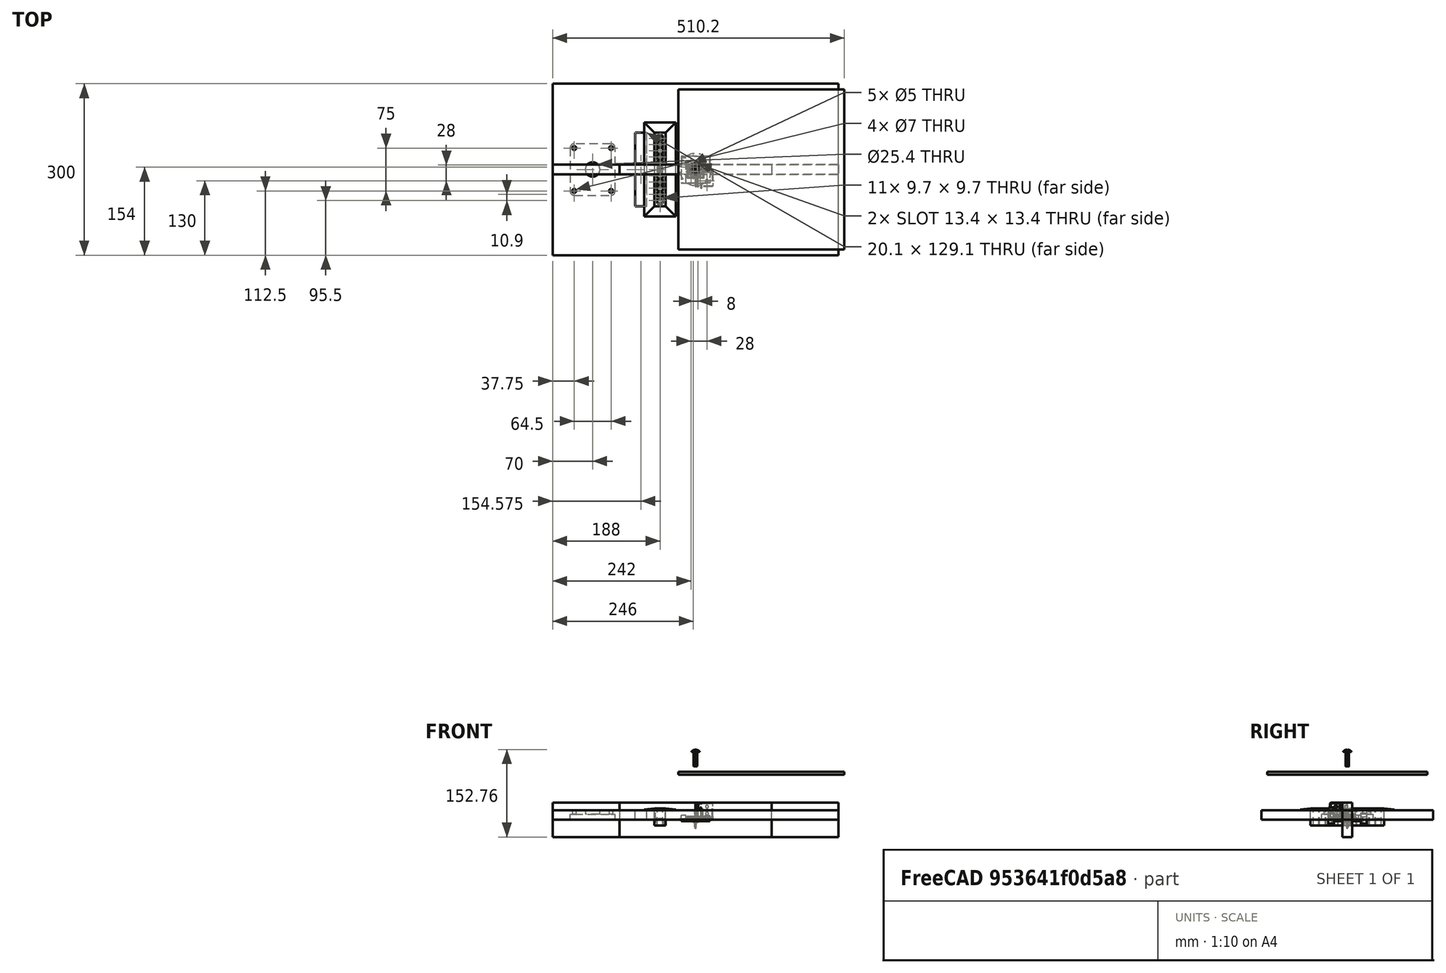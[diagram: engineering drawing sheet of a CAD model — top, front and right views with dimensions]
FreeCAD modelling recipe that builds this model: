
FCSTD DOCUMENT  (FreeCAD 1.0R39109 (Git))
Label: BoxV2
License: All rights reserved
LicenseURL: https://en.wikipedia.org/wiki/All_rights_reserved
objects: TechDraw::DrawViewDimension×86, App::Link×72, Part::Feature×47, App::DocumentObjectGroupPython×30, TechDraw::DrawProjGroupItem×23, Sketcher::SketchObject×22, TechDraw::DrawViewBalloon×18, PartDesign::Pad×15, PartDesign::Body×14, App::FeaturePython×9, TechDraw::DrawSVGTemplate×8, TechDraw::DrawPage×8, TechDraw::DrawProjGroup×7, Spreadsheet::Sheet×5, PartDesign::Pocket×5, TechDraw::DrawViewAnnotation×4, Part::FeaturePython×4, App::DocumentObjectGroup×4, PartDesign::LinearPattern×3, PartDesign::Mirrored×3, +15 more types
note: 352 computed .brp shape members not serialized (recipe doc carries the construction recipe); baked Part::Feature solids carry a one-line shape summary decoded from their .brp
EXTERNAL_REF file=../../V1/Projects/Box.FCStd obj=Body002

FEATURE [Sketcher::SketchObject] Sketch
  ArcFitTolerance = 1e-06
  AttachmentSupport = -> [XY_Plane]
  FullyConstrained = true
  MakeInternals = false
  MapMode = 5
  sketch-geometry (4):
    g0: LineSegment StartX=0 StartY=0 StartZ=0 EndX=30 EndY=0 EndZ=0
    g1: LineSegment StartX=30 StartY=0 StartZ=0 EndX=30 EndY=-30 EndZ=0
    g2: LineSegment StartX=30 StartY=-30 StartZ=0 EndX=0 EndY=-30 EndZ=0
    g3: LineSegment StartX=0 StartY=-30 StartZ=0 EndX=0 EndY=0 EndZ=0
  constraints (11):
    c: Coincident(g0,g1)
    c: Coincident(g1,g2)
    c: Coincident(g2,g3)
    c: Coincident(g3,g0)
    c: Horizontal(g0)
    c: Horizontal(g2)
    c: Vertical(g1)
    c: Vertical(g3)
    c: Distance(g1,g3) = 30
    c: Coincident(g0,g-1)
    c: DistanceY(g1,g1) = 30
FEATURE [PartDesign::Pad] Pad
  Direction = (0,0,1)
  Length = 30
  Length2 = 10
  Profile = -> Sketch
  ReferenceAxis = -> Sketch [N_Axis]
  Refine = true
  Suppressed = false
  Type = 0
FEATURE [PartDesign::Thickness] Thickness
  Base = -> Pad [Face2,Face3,Face6]
  BaseFeature = -> Pad
  Intersection = false
  Join = 0
  Mode = 0
  Refine = true
  Reversed = true
  SupportTransform = false
  Suppressed = false
  Value = 4
FEATURE [Spreadsheet::Sheet] Spreadsheet  label="LHProperties"
  cells = A1='screw_diameter; B1(screw_diameter)=5; D1='clearance; E1(clearance)=0.2; A2='bracket_dim; B2(bracket_dim)=30; A3='led_amount; B3(led_amount)=11; A4='led_dim; B4(led_dim)=9.7; A5='led_array_spacing; B5(led_array_spacing)=1.2; A6='led_array_housing_spacing; B6(led_array_housing_spacing)=5; A7='led_housing_base_length; B7(led_housing_base_length)==led_amount * led_dim + (led_amount - 1) * led_array_spacing + 2 * led_array_housing_spacing; C7='calculated; A8='led_housing_base_width; B8(led_housing_base_width)==2 * led_array_housing_spacing + led_dim; C8='calculated; A9='thickness_box_cover; B9(thickness_box_cover)==<<BXProperties>>.box_cover_thickness; C9='calculated; A10='led_housing_latch_offset_ratio; B10(led_housing_latch_offset_ratio)=4.5; A11='led_housing_latch_center_offset; B11(led_housing_latch_center_offset)==led_housing_base_length / led_housing_latch_offset_ratio; C11='calculated; A12='led_housing_latch_width; B12(led_housing_latch_width)=8; A13='led_housing_latch_thickness; B13(led_housing_latch_thickness)=1.2; A14='led_housing_height; B14(led_housing_height)==thickness_box_cover + 10 + cover_height; C14='calculated; A15='thickness_housing_shelf; B15(thickness_housing_shelf)=1.2; A16='led_housing_shelf_protrusion; B16(led_housing_shelf_protrusion)==(housing_hole_width - led_housing_base_width) / 2 - clearance / 2; C16='calculated; A17='housing_hole_width; B17(housing_hole_width)=21; A18='latch_length; B18(latch_length)=22; A19='cover_width; B19(cover_width)=55; A20='cover_height; B20(cover_height)=3
FEATURE [Sketcher::SketchObject] Sketch001
  ArcFitTolerance = 1e-06
  AttachmentOffset = pos=(0,2,0) rot=(0,0,1;0rad)
  AttachmentSupport = -> [YZ_Plane]
  FullyConstrained = true
  MakeInternals = false
  MapMode = 5
  Placement = pos=(0,0,2) rot=(0.57735,0.57735,0.57735;2.0944rad)
  expr: Constraints[1] = <<LHProperties>>.screw_diameter
  sketch-geometry (8):
    g0: Circle CenterX=-20 CenterY=21 CenterZ=0 NormalX=0 NormalY=0 NormalZ=1 AngleXU=0 Radius=2.5
    g1: Circle CenterX=-20 CenterY=9 CenterZ=0 NormalX=0 NormalY=0 NormalZ=1 AngleXU=0 Radius=2.5
    g2: LineSegment [constr] StartX=0 StartY=0 StartZ=0 EndX=0 EndY=30 EndZ=0
    g3: LineSegment [constr] StartX=0 StartY=30 StartZ=0 EndX=-30 EndY=30 EndZ=0
    g4: LineSegment [constr] StartX=-30 StartY=30 StartZ=0 EndX=-30 EndY=0 EndZ=0
    g5: LineSegment [constr] StartX=-30 StartY=0 StartZ=0 EndX=0 EndY=0 EndZ=0
    g6: LineSegment [constr] StartX=-20 StartY=21 StartZ=0 EndX=-20 EndY=30 EndZ=0
    g7: LineSegment [constr] StartX=-20 StartY=9 StartZ=0 EndX=-20 EndY=0 EndZ=0
  constraints (23):
    c: Equal(g1,g0)
    c: Diameter(g0) = 5
    c: Vertical(g0,g1)
    c: DistanceX(g1) = -20
    c: Coincident(g2,g3)
    c: Coincident(g3,g4)
    c: Coincident(g4,g5)
    c: Coincident(g5,g2)
    c: Vertical(g2)
    c: Vertical(g4)
    c: Horizontal(g3)
    c: Horizontal(g5)
    c: Coincident(g2,g-1)
    c: DistanceX(g3,g3) = 30
    c: DistanceY(g4,g4) = 30
    c: Coincident(g6,g0)
    c: PointOnObject(g6,g3)
    c: Vertical(g6)
    c: Coincident(g7,g1)
    c: PointOnObject(g7,g5)
    c: Vertical(g7)
    c: Equal(g7,g6)
    c: DistanceY(g1,g0) = 12
FEATURE [PartDesign::Pocket] Pocket
  BaseFeature = -> Thickness
  Direction = (-1,0,0)
  Length = 10
  Length2 = 5
  Midplane = true
  Profile = -> Sketch001
  ReferenceAxis = -> Sketch001 [N_Axis]
  Refine = true
  Suppressed = false
  Type = 0
FEATURE [PartDesign::PolarPattern] PolarPattern
  Angle = 90
  Axis = -> Sketch001 [V_Axis]
  BaseFeature = -> Pocket
  Mode = 0
  Occurrences = 2
  Offset = 120
  Originals = -> [Pocket]
  Refine = true
  Suppressed = false
  TransformMode = 0
FEATURE [PartDesign::SubtractiveCylinder] Cylinder
  Angle = 360
  AttacherType = Attacher::AttachEngine3D
  AttachmentOffset = pos=(20,-20,0) rot=(0,0,1;0rad)
  AttachmentSupport = -> [XY_Plane]
  BaseFeature = -> PolarPattern
  FirstAngle = 0
  Height = 10
  MapMode = 5
  Placement = pos=(20,-20,0) rot=(0,0,1;0rad)
  Radius = 2.5
  Refine = true
  SecondAngle = 0
  Suppressed = false
  expr: Radius = <<LHProperties>>.screw_diameter / 2
FEATURE [PartDesign::Chamfer] Chamfer
  Angle = 45
  Base = -> Cylinder [Edge35]
  BaseFeature = -> Cylinder
  ChamferType = 0
  FlipDirection = false
  Placement = pos=(20,-20,0) rot=(0,0,1;0rad)
  Refine = true
  Size = 8
  Size2 = 1
  SupportTransform = false
  Suppressed = false
  UseAllEdges = false
FEATURE [PartDesign::Chamfer] Chamfer001
  Angle = 45
  Base = -> Chamfer [Edge1,Edge2,Edge3,Edge4,Edge6,Edge8,Edge9,Edge10,Edge13,Edge14,Edge15,Edge16,Edge19,Edge20,Edge23,Edge24,Edge27,Edge30,Edge34,Edge35,Edge37,Edge38,Edge39]
  BaseFeature = -> Chamfer
  ChamferType = 0
  FlipDirection = false
  Placement = pos=(20,-20,0) rot=(0,0,1;0rad)
  Refine = true
  Size = 1
  Size2 = 1
  SupportTransform = false
  Suppressed = false
  UseAllEdges = false
FEATURE [PartDesign::Body] Body  label="Bracket"
  AllowCompound = false
  Group = -> [Sketch,Pad,Thickness,Sketch001,Pocket,PolarPattern,Cylinder,Chamfer,Chamfer001]
  Origin = -> Origin
  Tip = -> Chamfer001
FEATURE [Sketcher::SketchObject] Sketch002
  ArcFitTolerance = 1e-06
  AttachmentSupport = -> [XY_Plane002]
  FullyConstrained = true
  MakeInternals = false
  MapMode = 5
  expr: Constraints[10] = <<LHProperties>>.led_housing_base_length
  expr: Constraints[9] = <<LHProperties>>.led_housing_base_width
  sketch-geometry (6):
    g0: LineSegment StartX=-9.85 StartY=64.35 StartZ=0 EndX=-9.85 EndY=-64.35 EndZ=0
    g1: LineSegment StartX=-9.85 StartY=-64.35 StartZ=0 EndX=9.85 EndY=-64.35 EndZ=0
    g2: LineSegment StartX=9.85 StartY=-64.35 StartZ=0 EndX=9.85 EndY=64.35 EndZ=0
    g3: LineSegment StartX=9.85 StartY=64.35 StartZ=0 EndX=-9.85 EndY=64.35 EndZ=0
    g4: GeomPoint [constr] X=0 Y=0 Z=0
    g5: GeomPoint [constr] X=0 Y=0 Z=0
  constraints (13):
    c: Coincident(g0,g1)
    c: Coincident(g1,g2)
    c: Coincident(g2,g3)
    c: Coincident(g3,g0)
    c: Vertical(g0)
    c: Vertical(g2)
    c: Horizontal(g1)
    c: Horizontal(g3)
    c: Symmetric(g2,g0,g-1)
    c: DistanceX(g3,g3) = 19.7
    c: DistanceY(g2,g2) = 128.7
    c: Coincident(g4,g-1)
    c: Coincident(g5,g4)
FEATURE [PartDesign::Pad] Pad001
  Direction = (0,0,1)
  Length = 30
  Length2 = 10
  Profile = -> Sketch002
  ReferenceAxis = -> Sketch002 [N_Axis]
  Refine = true
  Suppressed = false
  Type = 0
  expr: Length = <<LHProperties>>.led_housing_height
FEATURE [PartDesign::SubtractiveBox] Box
  AttacherType = Attacher::AttachEngine3D
  AttachmentOffset = pos=(-4.85,49.65,0) rot=(0,0,1;0rad)
  AttachmentSupport = -> [XY_Plane002]
  BaseFeature = -> Pad001
  Height = 30
  Length = 9.7
  MapMode = 5
  Placement = pos=(-4.85,49.65,0) rot=(0,0,1;0rad)
  Refine = true
  Suppressed = false
  Width = 9.7
  expr: .AttachmentOffset.Base.x = -<<LHProperties>>.led_dim / 2
  expr: .AttachmentOffset.Base.y = -<<LHProperties>>.led_dim + <<LHProperties>>.led_housing_base_length / 2 - <<LHProperties>>.led_array_housing_spacing
  expr: Length = <<LHProperties>>.led_dim
  expr: Width = <<LHProperties>>.led_dim
FEATURE [PartDesign::LinearPattern] LinearPattern
  BaseFeature = -> Box
  Direction = -> Y_Axis002
  Length = 109
  Mode = 1
  Occurrences = 11
  Offset = 10.9
  Originals = -> [Box]
  Placement = pos=(-4.85,49.65,0) rot=(0,0,1;0rad)
  Refine = true
  Reversed = true
  Suppressed = false
  TransformMode = 0
  expr: Occurrences = <<LHProperties>>.led_amount
  expr: Offset = <<LHProperties>>.led_array_spacing + <<LHProperties>>.led_dim
FEATURE [Sketcher::SketchObject] Sketch003
  ArcFitTolerance = 1e-06
  AttachmentOffset = pos=(0,0,28.6) rot=(0,0,1;0rad)
  AttachmentSupport = -> [XZ_Plane002]
  ExternalGeometry = -> [LinearPattern]
  FullyConstrained = true
  MakeInternals = false
  MapMode = 5
  Placement = pos=(0,-28.6,6.4e-15) rot=(1,0,0;1.5708rad)
  expr: .AttachmentOffset.Base.z = <<LHProperties>>.led_housing_latch_center_offset
  expr: Constraints[13] = <<LHProperties>>.led_array_spacing
  expr: Constraints[14] = <<LHProperties>>.led_housing_latch_thickness + <<LHProperties>>.clearance
  expr: Constraints[17] = <<LHProperties>>.latch_length
  sketch-geometry (6):
    g0: LineSegment StartX=9.85 StartY=0 StartZ=0 EndX=9.85 EndY=22 EndZ=0
    g1: LineSegment StartX=9.85 StartY=22 StartZ=0 EndX=8.45 EndY=22 EndZ=0
    g2: LineSegment StartX=8.45 StartY=22 StartZ=0 EndX=8.45 EndY=15 EndZ=0
    g3: LineSegment StartX=8.45 StartY=15 StartZ=0 EndX=6.05 EndY=3 EndZ=0
    g4: LineSegment StartX=6.05 StartY=3 StartZ=0 EndX=6.05 EndY=0 EndZ=0
    g5: LineSegment StartX=6.05 StartY=0 StartZ=0 EndX=9.85 EndY=0 EndZ=0
  constraints (18):
    c: PointOnObject(g0,g-1)
    c: Vertical(g0)
    c: PointOnObject(g0,g-4)
    c: Coincident(g1,g0)
    c: Horizontal(g1)
    c: Coincident(g1,g2)
    c: Vertical(g2)
    c: Coincident(g2,g3)
    c: Coincident(g3,g4)
    c: Vertical(g4)
    c: Coincident(g4,g5)
    c: Coincident(g5,g0)
    c: Horizontal(g5)
    c: DistanceX(g-3,g4) = 1.2
    c: DistanceX(g1,g1) = 1.4
    c: DistanceY(g2,g-4) = 15
    c: DistanceY(g4,g3) = 3
    c: DistanceY(g0,g0) = 22
FEATURE [PartDesign::Pocket] Pocket001
  BaseFeature = -> LinearPattern
  Direction = (0,1,-2e-16)
  Length = 10
  Length2 = 5
  Midplane = true
  Placement = pos=(-4.85,49.65,0) rot=(0,0,1;0rad)
  Profile = -> Sketch003
  ReferenceAxis = -> Sketch003 [N_Axis]
  Refine = true
  Suppressed = false
  Type = 0
  expr: Length = <<LHProperties>>.led_housing_latch_width + 2
FEATURE [PartDesign::Mirrored] Mirrored
  MirrorPlane = -> Sketch003 [V_Axis]
  Placement = pos=(-4.85,49.65,0) rot=(0,0,1;0rad)
  Refine = true
  Suppressed = false
  TransformMode = 0
FEATURE [PartDesign::LinearPattern] LinearPattern001
  Direction = -> Sketch003 [N_Axis]
  Length = 57.2
  Mode = 1
  Occurrences = 2
  Offset = 57.2
  Placement = pos=(-4.85,49.65,0) rot=(0,0,1;0rad)
  Refine = true
  Reversed = true
  Suppressed = false
  TransformMode = 0
  expr: Offset = <<LHProperties>>.led_housing_latch_center_offset * 2
FEATURE [PartDesign::MultiTransform] MultiTransform
  BaseFeature = -> Pocket001
  Originals = -> [Pocket001]
  Placement = pos=(-4.85,49.65,0) rot=(0,0,1;0rad)
  Refine = true
  Suppressed = false
  TransformMode = 0
  Transformations = -> [Mirrored,LinearPattern001]
FEATURE [Sketcher::SketchObject] Sketch004
  ArcFitTolerance = 1e-06
  AttachmentSupport = -> [XZ_Plane003]
  FullyConstrained = true
  MakeInternals = false
  MapMode = 5
  Placement = pos=(0,0,0) rot=(1,0,0;1.5708rad)
  expr: Constraints[10] = <<LHProperties>>.latch_length - <<LHProperties>>.clearance
  expr: Constraints[13] = <<LHProperties>>.led_housing_height
  expr: Constraints[14] = <<LHProperties>>.thickness_box_cover + <<LHProperties>>.clearance + <<LHProperties>>.cover_height
  expr: Constraints[8] = <<LHProperties>>.led_housing_latch_thickness
  sketch-geometry (15):
    g0: LineSegment StartX=0.5 StartY=0 StartZ=0 EndX=1 EndY=0 EndZ=0
    g1: LineSegment StartX=1.49592 StartY=0.43623 StartZ=0 EndX=2.62751 EndY=9.23623 EndZ=0
    g2: LineSegment StartX=2.13159 StartY=9.8 StartZ=0 EndX=1.2 EndY=9.8 EndZ=0
    g3: LineSegment StartX=1.2 StartY=9.8 StartZ=0 EndX=1.2 EndY=21.8 EndZ=0
    g4: LineSegment StartX=1.2 StartY=21.8 StartZ=0 EndX=0.5 EndY=21.8 EndZ=0
    g5: LineSegment StartX=0 StartY=21.3 StartZ=0 EndX=0 EndY=0.5 EndZ=0
    g6: LineSegment [constr] StartX=0 StartY=0 StartZ=0 EndX=0 EndY=30 EndZ=0
    g7: ArcOfCircle CenterX=2.13159 CenterY=9.3 CenterZ=0 NormalX=0 NormalY=0 NormalZ=1 AngleXU=0 Radius=0.5 StartAngle=6.1553 EndAngle=7.85398
    g8: GeomPoint [constr] X=2.7 Y=9.8 Z=0
    g9: ArcOfCircle CenterX=1 CenterY=0.5 CenterZ=0 NormalX=0 NormalY=0 NormalZ=1 AngleXU=0 Radius=0.5 StartAngle=4.71239 EndAngle=6.1553
    g10: GeomPoint [constr] X=1.43982 Y=0 Z=0
    g11: ArcOfCircle CenterX=0.5 CenterY=0.5 CenterZ=0 NormalX=0 NormalY=0 NormalZ=1 AngleXU=0 Radius=0.5 StartAngle=3.14159 EndAngle=4.71239
    g12: GeomPoint [constr] X=0 Y=0 Z=0
    g13: ArcOfCircle CenterX=0.5 CenterY=21.3 CenterZ=0 NormalX=0 NormalY=0 NormalZ=1 AngleXU=0 Radius=0.5 StartAngle=1.5708 EndAngle=3.14159
    g14: GeomPoint [constr] X=0 Y=21.8 Z=0
  constraints (36):
    c: Coincident(g-1,g12)
    c: PointOnObject(g10,g-1)
    c: Horizontal(g2)
    c: Coincident(g2,g3)
    c: Vertical(g3)
    c: Coincident(g3,g4)
    c: PointOnObject(g14,g-2)
    c: Horizontal(g4)
    c: DistanceX(g14,g4) = 1.2
    c: DistanceX(g2,g8) = 1.5
    c: DistanceY(g12,g14) = 21.8
    c: Coincident(g6,g12)
    c: PointOnObject(g6,g-2)
    c: DistanceY(g6,g6) = 30
    c: DistanceY(g2,g6) = 20.2
    c: PointOnObject(g8,g1)
    c: PointOnObject(g8,g2)
    c: Tangent(g1,g7) = -1.5708
    c: Tangent(g2,g7) = -1.5708
    c: PointOnObject(g10,g0)
    c: PointOnObject(g10,g1)
    c: Tangent(g0,g9) = -1.5708
    c: Tangent(g1,g9) = -1.5708
    c: PointOnObject(g12,g0)
    c: PointOnObject(g12,g5)
    c: Tangent(g0,g11) = -1.5708
    c: Tangent(g5,g11) = -1.5708
    c: Equal(g7,g9)
    c: Radius(g7) = 0.5
    c: Radius(g11) = 0.5
    c: DistanceX(g0,g0) = 0.5
    c: PointOnObject(g14,g4)
    c: PointOnObject(g14,g5)
    c: Tangent(g4,g13) = -1.5708
    c: Tangent(g5,g13) = -1.5708
    c: Equal(g13,g7)
FEATURE [PartDesign::Pad] Pad002
  Direction = (0,-1,2e-16)
  Length = 8
  Length2 = 10
  Midplane = true
  Placement = pos=(0,0,0) rot=(1,0,0;1.5708rad)
  Profile = -> Sketch004
  ReferenceAxis = -> Sketch004 [N_Axis]
  Refine = true
  Suppressed = false
  Type = 0
  expr: Length = <<LHProperties>>.led_housing_latch_width
FEATURE [PartDesign::Body] Body002  label="Latch"
  AllowCompound = false
  Group = -> [Sketch004,Pad002]
  Origin = -> Origin003
  Placement = pos=(8.6,-28.5,0) rot=(0,0,1;0rad)
  Tip = -> Pad002
FEATURE [Sketcher::SketchObject] Sketch005
  ArcFitTolerance = 1e-06
  AttachmentSupport = -> [XZ_Plane002]
  FullyConstrained = true
  MakeInternals = false
  MapMode = 5
  Placement = pos=(0,0,0) rot=(1,0,0;1.5708rad)
  expr: Constraints[15] = <<LHProperties>>.cover_width / 2
  expr: Constraints[16] = <<LHProperties>>.cover_height
  expr: Constraints[2] = <<LHProperties>>.led_housing_height
  expr: Constraints[5] = <<LHProperties>>.led_housing_base_width / 2
  sketch-geometry (6):
    g0: LineSegment [constr] StartX=0 StartY=0 StartZ=0 EndX=0 EndY=30 EndZ=0
    g1: LineSegment [constr] StartX=0 StartY=30 StartZ=0 EndX=9.85 EndY=30 EndZ=0
    g2: LineSegment StartX=9.85 StartY=30 StartZ=0 EndX=27.5 EndY=28 EndZ=0
    g3: LineSegment StartX=27.5 StartY=28 StartZ=0 EndX=27.5 EndY=27 EndZ=0
    g4: LineSegment StartX=27.5 StartY=27 StartZ=0 EndX=9.85 EndY=27 EndZ=0
    g5: LineSegment StartX=9.85 StartY=27 StartZ=0 EndX=9.85 EndY=30 EndZ=0
  constraints (17):
    c: Coincident(g0,g-1)
    c: PointOnObject(g0,g-2)
    c: DistanceY(g0,g0) = 30
    c: Coincident(g1,g0)
    c: Horizontal(g1)
    c: DistanceX(g1,g1) = 9.85
    c: Coincident(g2,g1)
    c: Coincident(g3,g2)
    c: Coincident(g4,g3)
    c: Horizontal(g4)
    c: Vertical(g4,g1)
    c: Coincident(g5,g4)
    c: Coincident(g5,g1)
    c: Vertical(g3)
    c: DistanceY(g3,g3) = 1
    c: DistanceX(g0,g2) = 27.5
    c: DistanceY(g4,g0) = 3
FEATURE [PartDesign::AdditivePipe] AdditivePipe
  AuxilleryCurvelinear = true
  AuxillerySpineTangent = false
  BaseFeature = -> MultiTransform
  Binormal = (0,0,0)
  Mode = 0
  Placement = pos=(-4.85,49.65,0) rot=(0,0,1;0rad)
  Profile = -> Sketch005
  Refine = true
  Spine = -> MultiTransform [Edge95,Edge93,Edge11,Edge94]
  SpineTangent = false
  Suppressed = false
  Transformation = 0
  Transition = 1
FEATURE [PartDesign::Body] Body001  label="LED_Housing"
  AllowCompound = false
  Group = -> [Sketch002,Pad001,Box,LinearPattern,Sketch003,Pocket001,MultiTransform,Mirrored,LinearPattern001,Sketch005,AdditivePipe]
  Origin = -> Origin002
  Placement = pos=(-62,0,-10) rot=(0,0,1;0rad)
  Tip = -> AdditivePipe
FEATURE [Sketcher::SketchObject] Sketch006
  ArcFitTolerance = 1e-06
  AttachmentSupport = -> [XY_Plane004]
  FullyConstrained = true
  MakeInternals = false
  MapMode = 5
  expr: Constraints[17] = <<BXProperties>>.box_width
  expr: Constraints[18] = <<BXProperties>>.box_length
  expr: Constraints[27] = <<BXProperties>>.foam_edge_margin
  expr: Constraints[28] = <<BXProperties>>.foam_edge_margin
  expr: Constraints[29] = <<BXProperties>>.foam_width
  expr: Constraints[32] = <<LHProperties>>.led_housing_base_width + <<LHProperties>>.clearance * 2
  expr: Constraints[33] = <<LHProperties>>.led_housing_base_length + <<LHProperties>>.clearance * 2
  expr: Constraints[46] = <<BXProperties>>.joystick_true_width
  expr: Constraints[47] = <<BXProperties>>.joystick_true_length
  expr: Constraints[55] = <<BXProperties>>.joystick_bolt_hole
  sketch-geometry (29):
    g0: LineSegment StartX=-250 StartY=150 StartZ=0 EndX=-250 EndY=-150 EndZ=0
    g1: LineSegment StartX=-250 StartY=-150 StartZ=0 EndX=250 EndY=-150 EndZ=0
    g2: LineSegment StartX=250 StartY=-150 StartZ=0 EndX=250 EndY=150 EndZ=0
    g3: LineSegment StartX=250 StartY=150 StartZ=0 EndX=-250 EndY=150 EndZ=0
    g4: LineSegment StartX=-105.475 StartY=64.55 StartZ=0 EndX=-105.475 EndY=-64.55 EndZ=0
    g5: LineSegment StartX=-105.475 StartY=-64.55 StartZ=0 EndX=-85.375 EndY=-64.55 EndZ=0
    g6: LineSegment StartX=-85.375 StartY=-64.55 StartZ=0 EndX=-85.375 EndY=64.55 EndZ=0
    g7: LineSegment StartX=-85.375 StartY=64.55 StartZ=0 EndX=-105.475 EndY=64.55 EndZ=0
    g8: LineSegment [constr] StartX=-50 StartY=-140 StartZ=0 EndX=240 EndY=-140 EndZ=0
    g9: LineSegment [constr] StartX=240 StartY=-140 StartZ=0 EndX=240 EndY=140 EndZ=0
    g10: LineSegment [constr] StartX=240 StartY=140 StartZ=0 EndX=-50 EndY=140 EndZ=0
    g11: LineSegment [constr] StartX=-50 StartY=140 StartZ=0 EndX=-50 EndY=-140 EndZ=0
    g12: LineSegment [constr] StartX=-85.375 StartY=6.1e-15 StartZ=0 EndX=-50 EndY=-3e-15 EndZ=0
    g13: LineSegment [constr] StartX=-219.15 StartY=45.15 StartZ=0 EndX=-219.15 EndY=-45.15 EndZ=0
    g14: LineSegment [constr] StartX=-219.15 StartY=-45.15 StartZ=0 EndX=-140.85 EndY=-45.15 EndZ=0
    g15: LineSegment [constr] StartX=-140.85 StartY=-45.15 StartZ=0 EndX=-140.85 EndY=45.15 EndZ=0
    g16: LineSegment [constr] StartX=-140.85 StartY=45.15 StartZ=0 EndX=-219.15 EndY=45.15 EndZ=0
    g17: GeomPoint [constr] X=-180 Y=0 Z=0
    g18: LineSegment [constr] StartX=-140.85 StartY=-6.3e-15 StartZ=0 EndX=-105.475 EndY=-6.2e-15 EndZ=0
    g19: Circle CenterX=-180 CenterY=0 CenterZ=0 NormalX=0 NormalY=0 NormalZ=1 AngleXU=0 Radius=12.7
    g20: Circle CenterX=-212.25 CenterY=37.5 CenterZ=0 NormalX=0 NormalY=0 NormalZ=1 AngleXU=0 Radius=3.5
    g21: Circle CenterX=-147.75 CenterY=37.5 CenterZ=0 NormalX=0 NormalY=0 NormalZ=1 AngleXU=0 Radius=3.5
    g22: Circle CenterX=-147.75 CenterY=-37.5 CenterZ=0 NormalX=0 NormalY=0 NormalZ=1 AngleXU=0 Radius=3.5
    g23: Circle CenterX=-212.25 CenterY=-37.5 CenterZ=0 NormalX=0 NormalY=0 NormalZ=1 AngleXU=0 Radius=3.5
    g24: LineSegment [constr] StartX=-212.25 StartY=37.5 StartZ=0 EndX=-212.25 EndY=-37.5 EndZ=0
    g25: LineSegment [constr] StartX=-212.25 StartY=-37.5 StartZ=0 EndX=-147.75 EndY=-37.5 EndZ=0
    g26: LineSegment [constr] StartX=-147.75 StartY=-37.5 StartZ=0 EndX=-147.75 EndY=37.5 EndZ=0
    g27: LineSegment [constr] StartX=-147.75 StartY=37.5 StartZ=0 EndX=-212.25 EndY=37.5 EndZ=0
    g28: LineSegment [constr] StartX=-180 StartY=37.5 StartZ=0 EndX=-180 EndY=-37.5 EndZ=0
  constraints (73):
    c: Coincident(g0,g1)
    c: Coincident(g1,g2)
    c: Coincident(g2,g3)
    c: Coincident(g3,g0)
    c: Vertical(g0)
    c: Vertical(g2)
    c: Horizontal(g1)
    c: Horizontal(g3)
    c: Symmetric(g1,g0,g-1)
    c: Coincident(g4,g5)
    c: Coincident(g5,g6)
    c: Coincident(g6,g7)
    c: Coincident(g7,g4)
    c: Vertical(g4)
    c: Horizontal(g5)
    c: Horizontal(g7)
    c: Symmetric(g6,g5,g-1)
    c: DistanceX(g3,g3) = 500
    c: DistanceY(g2,g2) = 300
    c: Coincident(g8,g9)
    c: Coincident(g9,g10)
    c: Coincident(g10,g11)
    c: Coincident(g11,g8)
    c: Horizontal(g8)
    c: Horizontal(g10)
    c: Vertical(g11)
    c: Symmetric(g9,g8,g-1)
    c: DistanceX(g9,g2) = 10
    c: DistanceY(g9,g2) = 10
    c: DistanceX(g10,g10) = 290
    c: Symmetric(g6,g6,g12)
    c: Symmetric(g11,g11,g12)
    c: DistanceX(g7,g7) = 20.1
    c: DistanceY(g6,g6) = 129.1
    c: Coincident(g13,g14)
    c: Coincident(g14,g15)
    c: Coincident(g15,g16)
    c: Coincident(g16,g13)
    c: Vertical(g13)
    c: Vertical(g15)
    c: Horizontal(g14)
    c: Horizontal(g16)
    c: Symmetric(g13,g14,g17)
    c: Symmetric(g15,g15,g18)
    c: Symmetric(g4,g4,g18)
    c: Equal(g18,g12)
    c: DistanceX(g16,g16) = 78.3
    c: DistanceY(g15,g15) = 90.3
    c: DistanceX(g0,g17) = 70
    c: PointOnObject(g17,g-1)
    c: Coincident(g19,g17)
    c: Diameter(g19) = 25.4
    c: Equal(g23,g22)
    c: Equal(g22,g21)
    c: Equal(g21,g20)
    c: Diameter(g20) = 7
    c: Coincident(g24,g25)
    c: Coincident(g25,g26)
    c: Coincident(g26,g27)
    c: Coincident(g27,g24)
    c: Vertical(g26)
    c: Coincident(g24,g20)
    c: Coincident(g25,g22)
    c: Coincident(g24,g23)
    c: Coincident(g21,g26)
    c: Horizontal(g27)
    c: Horizontal(g25)
    c: DistanceX(g21,g15) = 6.9
    c: DistanceY(g21,g15) = 7.65
    c: Symmetric(g20,g23,g-1)
    c: Symmetric(g27,g27,g28)
    c: Symmetric(g25,g25,g28)
    c: PointOnObject(g17,g28)
FEATURE [Spreadsheet::Sheet] Spreadsheet001  label="BXProperties"
  cells = A1='box_width; B1(box_width)=500; A2='box_length; B2(box_length)=300; A3='box_cover_thickness; B3(box_cover_thickness)=17; A4='wall_thickness; B4(wall_thickness)=17; A5='joystick_hole_width; B5(joystick_hole_width)=70; A6='joystick_hole_length; B6(joystick_hole_length)=60; A7='joystick_edge_ratio; B7(joystick_edge_ratio)=0.07; A8='joystick_edge_margin; B8(joystick_edge_margin)==box_width * joystick_edge_ratio; C8='calculated; A9='foam_edge_margin; B9(foam_edge_margin)=10; A10='foam_box_ratio; B10(foam_box_ratio)=0.58; A11='foam_width; B11(foam_width)==box_width * foam_box_ratio; C11='calculated; A12='foam_length; B12(foam_length)==box_length - foam_edge_margin * 2; C12='calculated; A13='joystick_true_width; B13(joystick_true_width)=78.3; A14='joystick_true_length; B14(joystick_true_length)=90.3; A15='wall_height; B15(wall_height)=60; A16='joystick_hole; B16(joystick_hole)=25.4; A17='joystick_fillet_radius; B17(joystick_fillet_radius)=7; A18='joystick_bolt_hole; B18(joystick_bolt_hole)=7
FEATURE [PartDesign::Pad] Pad003
  Direction = (0,0,1)
  Length = 17
  Length2 = 10
  Profile = -> Sketch006
  ReferenceAxis = -> Sketch006 [N_Axis]
  Refine = true
  Suppressed = false
  Type = 0
  expr: Length = <<BXProperties>>.box_cover_thickness
FEATURE [Sketcher::SketchObject] Sketch007
  ArcFitTolerance = 1e-06
  AttachmentSupport = -> [XZ_Plane005]
  FullyConstrained = true
  MakeInternals = false
  MapMode = 5
  Placement = pos=(0,0,0) rot=(1,0,0;1.5708rad)
  expr: Constraints[10] = <<BXProperties>>.box_width
  expr: Constraints[11] = <<BXProperties>>.wall_height
  sketch-geometry (5):
    g0: LineSegment StartX=-250 StartY=-30 StartZ=0 EndX=250 EndY=-30 EndZ=0
    g1: LineSegment StartX=250 StartY=-30 StartZ=0 EndX=250 EndY=30 EndZ=0
    g2: LineSegment StartX=250 StartY=30 StartZ=0 EndX=-250 EndY=30 EndZ=0
    g3: LineSegment StartX=-250 StartY=30 StartZ=0 EndX=-250 EndY=-30 EndZ=0
    g4: GeomPoint [constr] X=0 Y=0 Z=0
  constraints (12):
    c: Coincident(g0,g1)
    c: Coincident(g1,g2)
    c: Coincident(g2,g3)
    c: Coincident(g3,g0)
    c: Horizontal(g0)
    c: Horizontal(g2)
    c: Vertical(g1)
    c: Vertical(g3)
    c: Symmetric(g2,g0,g4)
    c: Coincident(g4,g-1)
    c: DistanceX(g2,g2) = 500
    c: DistanceY(g1,g1) = 60
FEATURE [PartDesign::Pad] Pad004
  Direction = (0,-1,2e-16)
  Length = 17
  Length2 = 10
  Midplane = true
  Placement = pos=(0,0,0) rot=(1,0,0;1.5708rad)
  Profile = -> Sketch007
  ReferenceAxis = -> Sketch007 [N_Axis]
  Refine = true
  Suppressed = false
  Type = 0
  expr: Length = <<BXProperties>>.wall_thickness
FEATURE [PartDesign::Body] Body004  label="Wall_Long"
  AllowCompound = false
  Group = -> [Sketch007,Pad004]
  Origin = -> Origin005
  Tip = -> Pad004
FEATURE [Sketcher::SketchObject] Sketch008
  ArcFitTolerance = 1e-06
  AttachmentSupport = -> [XZ_Plane006]
  FullyConstrained = true
  MakeInternals = false
  MapMode = 5
  Placement = pos=(0,0,0) rot=(1,0,0;1.5708rad)
  expr: Constraints[10] = <<BXProperties>>.box_length - <<BXProperties>>.wall_thickness * 2
  expr: Constraints[11] = <<BXProperties>>.wall_height
  sketch-geometry (5):
    g0: LineSegment StartX=-133 StartY=-30 StartZ=0 EndX=133 EndY=-30 EndZ=0
    g1: LineSegment StartX=133 StartY=-30 StartZ=0 EndX=133 EndY=30 EndZ=0
    g2: LineSegment StartX=133 StartY=30 StartZ=0 EndX=-133 EndY=30 EndZ=0
    g3: LineSegment StartX=-133 StartY=30 StartZ=0 EndX=-133 EndY=-30 EndZ=0
    g4: GeomPoint [constr] X=0 Y=0 Z=0
  constraints (12):
    c: Coincident(g0,g1)
    c: Coincident(g1,g2)
    c: Coincident(g2,g3)
    c: Coincident(g3,g0)
    c: Horizontal(g0)
    c: Horizontal(g2)
    c: Vertical(g1)
    c: Vertical(g3)
    c: Symmetric(g2,g0,g4)
    c: Coincident(g4,g-1)
    c: DistanceX(g2,g2) = 266
    c: DistanceY(g1,g1) = 60
FEATURE [PartDesign::Pad] Pad005
  Direction = (0,-1,2e-16)
  Length = 17
  Length2 = 10
  Midplane = true
  Placement = pos=(0,0,0) rot=(1,0,0;1.5708rad)
  Profile = -> Sketch008
  ReferenceAxis = -> Sketch008 [N_Axis]
  Refine = true
  Suppressed = false
  Type = 0
  expr: Length = <<BXProperties>>.wall_thickness
FEATURE [PartDesign::Body] Body005  label="Wall_Short"
  AllowCompound = false
  Group = -> [Sketch008,Pad005]
  Origin = -> Origin006
  Tip = -> Pad005
FEATURE [TechDraw::DrawSVGTemplate] Template
  EditableTexts = AuthorName=Alex Anastasakis,CheckDate=2024-11-29,CreationDate=2024-11-26,DrawingNumber=3,FC-Scale=1 : 4,FC-Title=Cover,SheetNumber=1 / 1,+2 more (map truncated)
  Height = 297
  Orientation = 1
  Template = <userpath>/AppData/Local/Programs/FreeCAD 1.0/data/Mod/TechDraw/Templates/A3_Landscape_TD.svg
  Width = 420
FEATURE [Sketcher::SketchObject] Sketch009
  ArcFitTolerance = 1e-06
  AttachmentSupport = -> [XY_Plane004]
  FullyConstrained = true
  MakeInternals = false
  MapMode = 5
  expr: Constraints[17] = Sketch006.Constraints[17]
  expr: Constraints[18] = Sketch006.Constraints[18]
  expr: Constraints[27] = Sketch006.Constraints[27]
  expr: Constraints[28] = Sketch006.Constraints[28]
  expr: Constraints[29] = Sketch006.Constraints[29]
  expr: Constraints[32] = Sketch006.Constraints[32]
  expr: Constraints[33] = Sketch006.Constraints[33]
  expr: Constraints[44] = Sketch006.Constraints[46]
  expr: Constraints[45] = Sketch006.Constraints[47]
  expr: Constraints[46] = Sketch006.Constraints[48]
  expr: Constraints[49] = <<BXProperties>>.joystick_hole
  expr: Constraints[69] = <<BXProperties>>.joystick_fillet_radius
  sketch-geometry (29):
    g0: LineSegment [constr] StartX=-250 StartY=150 StartZ=0 EndX=-250 EndY=-150 EndZ=0
    g1: LineSegment [constr] StartX=-250 StartY=-150 StartZ=0 EndX=250 EndY=-150 EndZ=0
    g2: LineSegment [constr] StartX=250 StartY=-150 StartZ=0 EndX=250 EndY=150 EndZ=0
    g3: LineSegment [constr] StartX=250 StartY=150 StartZ=0 EndX=-250 EndY=150 EndZ=0
    g4: LineSegment [constr] StartX=-105.475 StartY=64.55 StartZ=0 EndX=-105.475 EndY=-64.55 EndZ=0
    g5: LineSegment [constr] StartX=-105.475 StartY=-64.55 StartZ=0 EndX=-85.375 EndY=-64.55 EndZ=0
    g6: LineSegment [constr] StartX=-85.375 StartY=-64.55 StartZ=0 EndX=-85.375 EndY=64.55 EndZ=0
    g7: LineSegment [constr] StartX=-85.375 StartY=64.55 StartZ=0 EndX=-105.475 EndY=64.55 EndZ=0
    g8: LineSegment [constr] StartX=-50 StartY=-140 StartZ=0 EndX=240 EndY=-140 EndZ=0
    g9: LineSegment [constr] StartX=240 StartY=-140 StartZ=0 EndX=240 EndY=140 EndZ=0
    g10: LineSegment [constr] StartX=240 StartY=140 StartZ=0 EndX=-50 EndY=140 EndZ=0
    g11: LineSegment [constr] StartX=-50 StartY=140 StartZ=0 EndX=-50 EndY=-140 EndZ=0
    g12: LineSegment [constr] StartX=-85.375 StartY=1.2e-15 StartZ=0 EndX=-50 EndY=-1.22e-14 EndZ=0
    g13: LineSegment StartX=-219.15 StartY=38.15 StartZ=0 EndX=-219.15 EndY=-38.15 EndZ=0
    g14: LineSegment StartX=-212.15 StartY=-45.15 StartZ=0 EndX=-147.85 EndY=-45.15 EndZ=0
    g15: LineSegment StartX=-140.85 StartY=-38.15 StartZ=0 EndX=-140.85 EndY=38.15 EndZ=0
    g16: LineSegment StartX=-147.85 StartY=45.15 StartZ=0 EndX=-212.15 EndY=45.15 EndZ=0
    g17: GeomPoint [constr] X=-180 Y=0 Z=0
    g18: LineSegment [constr] StartX=-219.15 StartY=45.15 StartZ=0 EndX=-140.85 EndY=-45.15 EndZ=0
    g19: LineSegment [constr] StartX=-140.85 StartY=-4.6e-15 StartZ=0 EndX=-105.475 EndY=5e-16 EndZ=0
    g20: Circle [constr] CenterX=-180 CenterY=0 CenterZ=0 NormalX=0 NormalY=0 NormalZ=1 AngleXU=0 Radius=12.7
    g21: ArcOfCircle CenterX=-147.85 CenterY=38.15 CenterZ=0 NormalX=0 NormalY=0 NormalZ=1 AngleXU=0 Radius=7 StartAngle=0 EndAngle=1.5708
    g22: GeomPoint [constr] X=-140.85 Y=45.15 Z=0
    g23: ArcOfCircle CenterX=-212.15 CenterY=38.15 CenterZ=0 NormalX=0 NormalY=0 NormalZ=1 AngleXU=0 Radius=7 StartAngle=1.5708 EndAngle=3.14159
    g24: GeomPoint [constr] X=-219.15 Y=45.15 Z=0
    g25: ArcOfCircle CenterX=-212.15 CenterY=-38.15 CenterZ=0 NormalX=0 NormalY=0 NormalZ=1 AngleXU=0 Radius=7 StartAngle=3.14159 EndAngle=4.71239
    g26: GeomPoint [constr] X=-219.15 Y=-45.15 Z=0
    g27: ArcOfCircle CenterX=-147.85 CenterY=-38.15 CenterZ=0 NormalX=0 NormalY=0 NormalZ=1 AngleXU=0 Radius=7 StartAngle=4.71239 EndAngle=6.28319
    g28: GeomPoint [constr] X=-140.85 Y=-45.15 Z=0
  constraints (70):
    c: Coincident(g0,g1)
    c: Coincident(g1,g2)
    c: Coincident(g2,g3)
    c: Coincident(g3,g0)
    c: Vertical(g0)
    c: Vertical(g2)
    c: Horizontal(g1)
    c: Horizontal(g3)
    c: Symmetric(g1,g0,g-1)
    c: Coincident(g4,g5)
    c: Coincident(g5,g6)
    c: Coincident(g6,g7)
    c: Coincident(g7,g4)
    c: Vertical(g4)
    c: Horizontal(g5)
    c: Horizontal(g7)
    c: Symmetric(g6,g5,g-1)
    c: DistanceX(g3,g3) = 500
    c: DistanceY(g2,g2) = 300
    c: Coincident(g8,g9)
    c: Coincident(g9,g10)
    c: Coincident(g10,g11)
    c: Coincident(g11,g8)
    c: Horizontal(g8)
    c: Horizontal(g10)
    c: Vertical(g11)
    c: Symmetric(g9,g8,g-1)
    c: DistanceX(g9,g2) = 10
    c: DistanceY(g9,g2) = 10
    c: DistanceX(g10,g10) = 290
    c: Symmetric(g6,g6,g12)
    c: Symmetric(g11,g11,g12)
    c: DistanceX(g7,g7) = 20.1
    c: DistanceY(g6,g6) = 129.1
    c: Vertical(g13)
    c: Vertical(g15)
    c: Horizontal(g14)
    c: Horizontal(g16)
    c: Coincident(g18,g24)
    c: Coincident(g18,g28)
    c: Symmetric(g18,g18,g17)
    c: Symmetric(g28,g22,g19)
    c: Symmetric(g4,g4,g19)
    c: Equal(g19,g12)
    c: DistanceX(g24,g22) = 78.3
    c: DistanceY(g28,g22) = 90.3
    c: DistanceX(g0,g17) = 70
    c: PointOnObject(g17,g-1)
    c: Coincident(g20,g17)
    c: Diameter(g20) = 25.4
    c: PointOnObject(g22,g15)
    c: PointOnObject(g22,g16)
    c: Tangent(g15,g21) = -1.5708
    c: Tangent(g16,g21) = -1.5708
    c: PointOnObject(g24,g16)
    c: PointOnObject(g24,g13)
    c: Tangent(g16,g23) = -1.5708
    c: Tangent(g13,g23) = -1.5708
    c: PointOnObject(g26,g14)
    c: PointOnObject(g26,g13)
    c: Tangent(g14,g25) = -1.5708
    c: Tangent(g13,g25) = -1.5708
    c: PointOnObject(g28,g14)
    c: PointOnObject(g28,g15)
    c: Tangent(g14,g27) = -1.5708
    c: Tangent(g15,g27) = -1.5708
    c: Equal(g27,g25)
    c: Equal(g27,g21)
    c: Equal(g21,g23)
    c: Radius(g27) = 7
FEATURE [PartDesign::Pocket] Pocket002
  BaseFeature = -> Pad003
  Direction = (0,0,-1)
  Length = 10
  Length2 = 5
  Profile = -> Sketch009
  ReferenceAxis = -> Sketch009 [N_Axis]
  Refine = true
  Reversed = true
  Suppressed = false
  Type = 0
FEATURE [PartDesign::Body] Body003  label="Box_Cover"
  AllowCompound = false
  Group = -> [Sketch006,Pad003,Sketch009,Pocket002]
  Origin = -> Origin004
  Tip = -> Pocket002
FEATURE [TechDraw::DrawProjGroupItem] View  label="Front"
  CoarseView = false
  Direction = (0,-1,0)
  Focus = 100
  HardHidden = true
  IsoCount = 0
  IsoHidden = false
  IsoVisible = false
  LockPosition = true
  Perspective = false
  Rotation = 0
  RotationVector = (1,0,0)
  Scale = 0.25
  ScaleType = 2
  ScrubCount = 1
  SeamHidden = false
  SeamVisible = false
  SmoothHidden = false
  SmoothVisible = true
  Source = -> [Body003]
  Type = 0
  X = 0
  XDirection = (1,0,0)
  Y = 0
FEATURE [TechDraw::DrawProjGroupItem] ProjItem001  label="FrontTopRight"
  CoarseView = false
  Direction = (0.57735,-0.57735,0.57735)
  Focus = 100
  HardHidden = false
  IsoCount = 0
  IsoHidden = false
  IsoVisible = false
  LockPosition = false
  Perspective = false
  Rotation = 0
  RotationVector = (1,0,0)
  ScaleType = 2
  ScrubCount = 1
  SeamHidden = false
  SeamVisible = false
  SmoothHidden = false
  SmoothVisible = true
  Source = -> [Body003]
  Type = 7
  X = 171.843
  XDirection = (0.707107,0.707107,0)
  Y = -22.4367
FEATURE [TechDraw::DrawViewDimension] Dimension002
  AngleOverride = false
  Arbitrary = false
  ArbitraryTolerances = false
  BoxCorners = (2) [(-50,-2.125,0),(50,2.125,0)]
  EqualTolerance = true
  ExtensionAngle = 0
  FormatSpec = %.2w
  FormatSpecOverTolerance = %+.2w
  FormatSpecUnderTolerance = %+.2w
  Inverted = false
  LineAngle = 0
  LockPosition = false
  MeasureType = 1
  OverTolerance = 0
  References2D = -> [View]
  Rotation = 0
  Scale = 0.25
  ScaleType = 0
  TheoreticalExact = false
  Type = 2
  UnderTolerance = 0
  X = -76.3815
  Y = -6.4878
FEATURE [Sketcher::SketchObject] Sketch010
  ArcFitTolerance = 1e-06
  AttachmentSupport = -> [XY_Plane008]
  FullyConstrained = true
  MakeInternals = false
  MapMode = 5
  expr: Constraints[10] = <<BXProperties>>.foam_width
  expr: Constraints[11] = <<BXProperties>>.foam_length
  sketch-geometry (5):
    g0: LineSegment StartX=-145 StartY=-140 StartZ=0 EndX=145 EndY=-140 EndZ=0
    g1: LineSegment StartX=145 StartY=-140 StartZ=0 EndX=145 EndY=140 EndZ=0
    g2: LineSegment StartX=145 StartY=140 StartZ=0 EndX=-145 EndY=140 EndZ=0
    g3: LineSegment StartX=-145 StartY=140 StartZ=0 EndX=-145 EndY=-140 EndZ=0
    g4: GeomPoint [constr] X=0 Y=0 Z=0
  constraints (12):
    c: Coincident(g0,g1)
    c: Coincident(g1,g2)
    c: Coincident(g2,g3)
    c: Coincident(g3,g0)
    c: Horizontal(g0)
    c: Horizontal(g2)
    c: Vertical(g1)
    c: Vertical(g3)
    c: Symmetric(g2,g0,g4)
    c: Coincident(g4,g-1)
    c: DistanceX(g2,g2) = 290
    c: DistanceY(g1,g1) = 280
FEATURE [PartDesign::Pad] Pad006
  Direction = (0,0,1)
  Length = 5
  Length2 = 10
  Profile = -> Sketch010
  ReferenceAxis = -> Sketch010 [N_Axis]
  Refine = true
  Suppressed = false
  Type = 0
FEATURE [PartDesign::Body] Body006  label="Foam_Pad"
  AllowCompound = false
  Group = -> [Sketch010,Pad006]
  Origin = -> Origin008
  Placement = pos=(115.2,0,79) rot=(0,0,1;0rad)
  Tip = -> Pad006
FEATURE [Sketcher::SketchObject] Sketch027
  ArcFitTolerance = 1e-06
  AttachmentSupport = -> [XY_Plane015]
  FullyConstrained = true
  MakeInternals = false
  MapMode = 5
  expr: Constraints[11] = <<CMProperties>>.cm_size
  sketch-geometry (5):
    g0: LineSegment StartX=-15 StartY=-15 StartZ=0 EndX=15 EndY=-15 EndZ=0
    g1: LineSegment StartX=15 StartY=-15 StartZ=0 EndX=15 EndY=15 EndZ=0
    g2: LineSegment StartX=15 StartY=15 StartZ=0 EndX=-15 EndY=15 EndZ=0
    g3: LineSegment StartX=-15 StartY=15 StartZ=0 EndX=-15 EndY=-15 EndZ=0
    g4: GeomPoint [constr] X=-1e-16 Y=0 Z=0
  constraints (12):
    c: Coincident(g0,g1)
    c: Coincident(g1,g2)
    c: Coincident(g2,g3)
    c: Coincident(g3,g0)
    c: Horizontal(g0)
    c: Horizontal(g2)
    c: Vertical(g1)
    c: Vertical(g3)
    c: Symmetric(g2,g0,g4)
    c: Coincident(g4,g-1)
    c: Equal(g2,g1)
    c: DistanceX(g2,g2) = 30
FEATURE [Spreadsheet::Sheet] Spreadsheet003  label="CMProperties"
  cells = A1='cm_size; B1(cm_size)=30; A2='cm_base_height; B2(cm_base_height)=1.2; A3='cm_height; B3(cm_height)==cm_track_size; A4='border_thickness; B4(border_thickness)=1.6; A5='cover_thickness; B5(cover_thickness)=1.2; A6='cm_cover_size; B6(cm_cover_size)==cm_size - border_thickness * 2 - 0.2 * 2; C6='calculated; A7='cm_track_size; B7(cm_track_size)=3.5
FEATURE [PartDesign::Pad] Pad013
  Direction = (0,0,1)
  Length = 4.7
  Length2 = 10
  Profile = -> Sketch027
  ReferenceAxis = -> Sketch027 [N_Axis]
  Refine = true
  Suppressed = false
  Type = 0
  expr: Length = <<CMProperties>>.cm_height + <<CMProperties>>.cm_base_height
FEATURE [Sketcher::SketchObject] Sketch028
  ArcFitTolerance = 1e-06
  AttachmentOffset = pos=(0,0,1.2) rot=(0,0,1;0rad)
  AttachmentSupport = -> [XY_Plane015]
  FullyConstrained = true
  MakeInternals = false
  MapMode = 5
  Placement = pos=(0,0,1.2) rot=(0,0,1;0rad)
  expr: .AttachmentOffset.Base.z = <<CMProperties>>.cm_base_height
  expr: Constraints[10] = <<CMProperties>>.cm_size / 2
  expr: Constraints[34] = <<CMProperties>>.cm_track_size
  expr: Constraints[9] = <<CMProperties>>.cm_size / 2
  sketch-geometry (19):
    g0: ArcOfCircle [constr] CenterX=-6 CenterY=6.01432 CenterZ=0 NormalX=0 NormalY=0 NormalZ=1 AngleXU=0 Radius=6.01432 StartAngle=4.71239 EndAngle=6.21417
    g1: ArcOfCircle [constr] CenterX=5.2375 CenterY=5.2375 CenterZ=0 NormalX=0 NormalY=0 NormalZ=1 AngleXU=0 Radius=5.25 StartAngle=4.78141 EndAngle=9.35576
    g2: LineSegment [constr] StartX=-6 StartY=0 StartZ=0 EndX=-15 EndY=0 EndZ=0
    g3: ArcOfCircle [constr] CenterX=6.01432 CenterY=-6 CenterZ=0 NormalX=0 NormalY=0 NormalZ=1 AngleXU=0 Radius=6.01432 StartAngle=1.63981 EndAngle=3.14159
    g4: LineSegment [constr] StartX=0 StartY=-6 StartZ=0 EndX=0 EndY=-15 EndZ=0
    g5: ArcOfCircle [constr] CenterX=-15 CenterY=0 CenterZ=0 NormalX=0 NormalY=0 NormalZ=-1 AngleXU=-3.14159 Radius=1.75 StartAngle=1.5708 EndAngle=4.71239
    g6: LineSegment StartX=-6 StartY=1.75 StartZ=0 EndX=-15 EndY=1.75 EndZ=0
    g7: ArcOfCircle CenterX=-6 CenterY=6.01432 CenterZ=0 NormalX=0 NormalY=0 NormalZ=1 AngleXU=0 Radius=4.26432 StartAngle=4.71239 EndAngle=6.21417
    g8: ArcOfCircle CenterX=5.2375 CenterY=5.2375 CenterZ=0 NormalX=0 NormalY=0 NormalZ=1 AngleXU=0 Radius=7 StartAngle=4.78141 EndAngle=9.35576
    g9: ArcOfCircle CenterX=6.01432 CenterY=-6 CenterZ=0 NormalX=0 NormalY=0 NormalZ=1 AngleXU=0 Radius=4.26432 StartAngle=1.63981 EndAngle=3.14159
    g10: LineSegment StartX=1.75 StartY=-6 StartZ=0 EndX=1.75 EndY=-15 EndZ=0
    g11: ArcOfCircle [constr] CenterX=0 CenterY=-15 CenterZ=0 NormalX=0 NormalY=0 NormalZ=-1 AngleXU=1.5708 Radius=1.75 StartAngle=1.5708 EndAngle=4.71239
    g12: LineSegment StartX=-1.75 StartY=-6 StartZ=0 EndX=-1.75 EndY=-15 EndZ=0
    g13: ArcOfCircle CenterX=6.01432 CenterY=-6 CenterZ=0 NormalX=0 NormalY=0 NormalZ=1 AngleXU=0 Radius=7.76432 StartAngle=1.63981 EndAngle=3.14159
    g14: ArcOfCircle CenterX=5.2375 CenterY=5.2375 CenterZ=0 NormalX=0 NormalY=0 NormalZ=1 AngleXU=0 Radius=3.5 StartAngle=4.78141 EndAngle=9.35576
    g15: ArcOfCircle CenterX=-6 CenterY=6.01432 CenterZ=0 NormalX=0 NormalY=0 NormalZ=1 AngleXU=0 Radius=7.76432 StartAngle=4.71239 EndAngle=6.21417
    g16: LineSegment StartX=-6 StartY=-1.75 StartZ=0 EndX=-15 EndY=-1.75 EndZ=0
    g17: LineSegment StartX=1.75 StartY=-15 StartZ=0 EndX=-1.75 EndY=-15 EndZ=0
    g18: LineSegment StartX=-15 StartY=1.75 StartZ=0 EndX=-15 EndY=-1.75 EndZ=0
  constraints (43):
    c: PointOnObject(g0,g-1)
    c: PointOnObject(g0,g-2)
    c: Tangent(g1,g0) = 1.5708
    c: PointOnObject(g2,g-1)
    c: Tangent(g2,g0) = 1.5708
    c: Vertical(g4)
    c: Tangent(g4,g3) = -1.5708
    c: Tangent(g3,g1) = 1.5708
    c: Vertical(g3,g-1)
    c: DistanceY(g4,g-1) = 15
    c: DistanceX(g2,g-1) = 15
    c: Tangent(g5,g6) = -1.5708
    c: Tangent(g5,g16) = 1.5708
    c: Tangent(g6,g7) = 1.5708
    c: Tangent(g7,g8) = 1.5708
    c: Tangent(g8,g9) = 1.5708
    c: Tangent(g9,g10) = -1.5708
    c: Tangent(g10,g11) = 1.5708
    c: Tangent(g11,g12) = -1.5708
    c: Tangent(g12,g13) = -1.5708
    c: Tangent(g13,g14) = 1.5708
    c: Tangent(g14,g15) = 1.5708
    c: Tangent(g15,g16) = 1.5708
    c: Coincident(g5,g2)
    c: Coincident(g1,g14)
    c: Coincident(g8,g1)
    c: Coincident(g0,g7)
    c: Coincident(g0,g15)
    c: Coincident(g3,g9)
    c: Coincident(g3,g13)
    c: Coincident(g11,g4)
    c: Horizontal(g10,g4)
    c: Horizontal(g11,g4)
    c: Vertical(g5,g2)
    c: DistanceY(g5,g5) = 3.5
    c: Equal(g6,g10)
    c: DistanceX(g0,g3) = 6
    c: Equal(g13,g15)
    c: Radius(g8) = 7
    c: Coincident(g17,g10)
    c: Coincident(g17,g11)
    c: Coincident(g18,g5)
    c: Coincident(g18,g5)
FEATURE [PartDesign::Pocket] Pocket011
  BaseFeature = -> Pad013
  Direction = (0,0,-1)
  Length = 5
  Length2 = 5
  Profile = -> Sketch028
  ReferenceAxis = -> Sketch028 [N_Axis]
  Refine = true
  Reversed = true
  Suppressed = false
  Type = 1
FEATURE [Sketcher::SketchObject] Sketch029
  ArcFitTolerance = 1e-06
  AttachmentOffset = pos=(0,0,4.7) rot=(0,0,1;0rad)
  AttachmentSupport = -> [XY_Plane015]
  FullyConstrained = true
  MakeInternals = false
  MapMode = 5
  Placement = pos=(0,0,4.7) rot=(0,0,1;0rad)
  expr: .AttachmentOffset.Base.z = <<CMProperties>>.cm_base_height + <<CMProperties>>.cm_height
  expr: Constraints[11] = Sketch027.Constraints[11]
  expr: Constraints[31] = Sketch028.Constraints[9]
  expr: Constraints[32] = Sketch028.Constraints[10]
  expr: Constraints[55] = <<CMProperties>>.cm_track_size
  sketch-geometry (41):
    g0: LineSegment [constr] StartX=-15 StartY=-15 StartZ=0 EndX=15 EndY=-15 EndZ=0
    g1: LineSegment [constr] StartX=15 StartY=-15 StartZ=0 EndX=15 EndY=15 EndZ=0
    g2: LineSegment [constr] StartX=15 StartY=15 StartZ=0 EndX=-15 EndY=15 EndZ=0
    g3: LineSegment [constr] StartX=-15 StartY=15 StartZ=0 EndX=-15 EndY=-15 EndZ=0
    g4: GeomPoint [constr] X=0 Y=0 Z=0
    g5: LineSegment StartX=15 StartY=-15 StartZ=0 EndX=15 EndY=15 EndZ=0
    g6: LineSegment StartX=15 StartY=15 StartZ=0 EndX=-15 EndY=15 EndZ=0
    g7: LineSegment StartX=13.4 StartY=-13.4 StartZ=0 EndX=13.4 EndY=13.4 EndZ=0
    g8: LineSegment StartX=13.4 StartY=13.4 StartZ=0 EndX=-13.4 EndY=13.4 EndZ=0
    g9: GeomPoint [constr] X=0 Y=0 Z=0
    g10: ArcOfCircle [constr] CenterX=-8 CenterY=8.06933 CenterZ=0 NormalX=0 NormalY=0 NormalZ=1 AngleXU=0 Radius=8.06933 StartAngle=4.71239 EndAngle=6.15201
    g11: ArcOfCircle [constr] CenterX=6.1963 CenterY=6.1963 CenterZ=0 NormalX=0 NormalY=0 NormalZ=1 AngleXU=0 Radius=6.25 StartAngle=4.84357 EndAngle=9.2936
    g12: LineSegment [constr] StartX=-8 StartY=0 StartZ=0 EndX=-15 EndY=0 EndZ=0
    g13: ArcOfCircle [constr] CenterX=8.06933 CenterY=-8 CenterZ=0 NormalX=0 NormalY=0 NormalZ=1 AngleXU=0 Radius=8.06933 StartAngle=1.70198 EndAngle=3.14159
    g14: LineSegment [constr] StartX=0 StartY=-8 StartZ=0 EndX=0 EndY=-15 EndZ=0
    g15: ArcOfCircle [constr] CenterX=-15 CenterY=0 CenterZ=0 NormalX=0 NormalY=0 NormalZ=-1 AngleXU=-3.14159 Radius=1.75 StartAngle=1.5708 EndAngle=4.71239
    g16: LineSegment [constr] StartX=-8 StartY=1.75 StartZ=0 EndX=-15 EndY=1.75 EndZ=0
    g17: ArcOfCircle [constr] CenterX=-8 CenterY=8.06933 CenterZ=0 NormalX=0 NormalY=0 NormalZ=1 AngleXU=0 Radius=6.31933 StartAngle=4.71239 EndAngle=6.15201
    g18: ArcOfCircle [constr] CenterX=6.1963 CenterY=6.1963 CenterZ=0 NormalX=0 NormalY=0 NormalZ=1 AngleXU=0 Radius=8 StartAngle=4.84357 EndAngle=9.2936
    g19: ArcOfCircle [constr] CenterX=8.06933 CenterY=-8 CenterZ=0 NormalX=0 NormalY=0 NormalZ=1 AngleXU=0 Radius=6.31933 StartAngle=1.70198 EndAngle=3.14159
    g20: LineSegment [constr] StartX=1.75 StartY=-8 StartZ=0 EndX=1.75 EndY=-15 EndZ=0
    g21: ArcOfCircle [constr] CenterX=0 CenterY=-15 CenterZ=0 NormalX=0 NormalY=0 NormalZ=-1 AngleXU=1.5708 Radius=1.75 StartAngle=1.5708 EndAngle=4.71239
    g22: LineSegment [constr] StartX=-1.75 StartY=-8 StartZ=0 EndX=-1.75 EndY=-15 EndZ=0
    g23: ArcOfCircle [constr] CenterX=8.06933 CenterY=-8 CenterZ=0 NormalX=0 NormalY=0 NormalZ=1 AngleXU=0 Radius=9.81933 StartAngle=1.70198 EndAngle=3.14159
    g24: ArcOfCircle [constr] CenterX=6.1963 CenterY=6.1963 CenterZ=0 NormalX=0 NormalY=0 NormalZ=1 AngleXU=0 Radius=4.5 StartAngle=4.84357 EndAngle=9.2936
    g25: ArcOfCircle [constr] CenterX=-8 CenterY=8.06933 CenterZ=0 NormalX=0 NormalY=0 NormalZ=1 AngleXU=0 Radius=9.81933 StartAngle=4.71239 EndAngle=6.15201
    g26: LineSegment [constr] StartX=-8 StartY=-1.75 StartZ=0 EndX=-15 EndY=-1.75 EndZ=0
    g27: LineSegment [constr] StartX=1.75 StartY=-15 StartZ=0 EndX=-1.75 EndY=-15 EndZ=0
    g28: LineSegment [constr] StartX=-15 StartY=1.75 StartZ=0 EndX=-15 EndY=-1.75 EndZ=0
    g29: LineSegment StartX=-15 StartY=1.75 StartZ=0 EndX=-13.4 EndY=1.75 EndZ=0
    g30: LineSegment StartX=13.4 StartY=-13.4 StartZ=0 EndX=1.75 EndY=-13.4 EndZ=0
    g31: LineSegment StartX=15 StartY=-15 StartZ=0 EndX=1.75 EndY=-15 EndZ=0
    g32: LineSegment StartX=-1.75 StartY=-15 StartZ=0 EndX=-15 EndY=-15 EndZ=0
    g33: LineSegment StartX=-15 StartY=-15 StartZ=0 EndX=-15 EndY=-1.75 EndZ=0
    g34: LineSegment StartX=-15 StartY=1.75 StartZ=0 EndX=-15 EndY=15 EndZ=0
    g35: LineSegment StartX=-13.4 StartY=13.4 StartZ=0 EndX=-13.4 EndY=1.75 EndZ=0
    g36: LineSegment StartX=-1.75 StartY=-13.4 StartZ=0 EndX=-13.4 EndY=-13.4 EndZ=0
    g37: LineSegment StartX=-13.4 StartY=-13.4 StartZ=0 EndX=-13.4 EndY=-1.75 EndZ=0
    g38: LineSegment StartX=-1.75 StartY=-13.4 StartZ=0 EndX=-1.75 EndY=-15 EndZ=0
    g39: LineSegment StartX=1.75 StartY=-15 StartZ=0 EndX=1.75 EndY=-13.4 EndZ=0
    g40: LineSegment StartX=-13.4 StartY=-1.75 StartZ=0 EndX=-15 EndY=-1.75 EndZ=0
  constraints (99):
    c: Coincident(g0,g1)
    c: Coincident(g1,g2)
    c: Coincident(g2,g3)
    c: Coincident(g3,g0)
    c: Horizontal(g0)
    c: Horizontal(g2)
    c: Vertical(g1)
    c: Vertical(g3)
    c: Symmetric(g2,g0,g4)
    c: Coincident(g4,g-1)
    c: Equal(g2,g1)
    c: DistanceX(g2,g2) = 30
    c: Coincident(g5,g6)
    c: Vertical(g5)
    c: Horizontal(g6)
    c: Coincident(g7,g8)
    c: Vertical(g7)
    c: Horizontal(g8)
    c: Symmetric(g7,g8,g9)
    c: Coincident(g9,g4)
    c: Equal(g8,g7)
    c: DistanceX(g7,g1) = 1.6
    c: PointOnObject(g10,g-1)
    c: PointOnObject(g10,g-2)
    c: Tangent(g11,g10) = 1.5708
    c: PointOnObject(g12,g-1)
    c: Tangent(g12,g10) = 1.5708
    c: Vertical(g14)
    c: Tangent(g14,g13) = -1.5708
    c: Tangent(g13,g11) = 1.5708
    c: Vertical(g13,g-1)
    c: DistanceY(g14,g-1) = 15
    c: DistanceX(g12,g-1) = 15
    c: Tangent(g15,g16) = -1.5708
    c: Tangent(g15,g26) = 1.5708
    c: Tangent(g16,g17) = 1.5708
    c: Tangent(g17,g18) = 1.5708
    c: Tangent(g18,g19) = 1.5708
    c: Tangent(g19,g20) = -1.5708
    c: Tangent(g20,g21) = 1.5708
    c: Tangent(g21,g22) = -1.5708
    c: Tangent(g22,g23) = -1.5708
    c: Tangent(g23,g24) = 1.5708
    c: Tangent(g24,g25) = 1.5708
    c: Tangent(g25,g26) = 1.5708
    c: Coincident(g15,g12)
    c: Coincident(g11,g24)
    c: Coincident(g18,g11)
    c: Coincident(g10,g17)
    c: Coincident(g10,g25)
    c: Coincident(g13,g19)
    c: Coincident(g13,g23)
    c: Coincident(g21,g14)
    c: Horizontal(g21,g14)
    c: Vertical(g15,g12) = 5
    c: DistanceY(g15,g15) = 3.5
    c: Equal(g16,g20) = 8
    c: DistanceX(g10,g13) = 8
    c: Equal(g23,g25) = 8
    c: Radius(g18) = 8
    c: Coincident(g27,g20)
    c: Coincident(g27,g21)
    c: Coincident(g28,g15)
    c: Coincident(g28,g15)
    c: Coincident(g29,g15)
    c: PointOnObject(g29,g16)
    c: Coincident(g30,g7)
    c: PointOnObject(g30,g20)
    c: Horizontal(g30)
    c: Coincident(g31,g5)
    c: Coincident(g31,g20)
    c: Horizontal(g31)
    c: Coincident(g32,g21)
    c: Coincident(g32,g0)
    c: Coincident(g33,g0)
    c: Coincident(g33,g15)
    c: Coincident(g34,g15)
    c: Coincident(g34,g6)
    c: Vertical(g34)
    c: Coincident(g35,g8)
    c: Coincident(g35,g29)
    c: Vertical(g35)
    c: PointOnObject(g36,g22)
    c: Horizontal(g36)
    c: Coincident(g37,g36)
    c: PointOnObject(g37,g26)
    c: Vertical(g37)
    c: Vertical(g37,g29)
    c: Horizontal(g36,g30)
    c: Coincident(g38,g36)
    c: Coincident(g38,g21)
    c: Coincident(g39,g30)
    c: Vertical(g39)
    c: Tangent(g39,g21)
    c: Coincident(g40,g37)
    c: Coincident(g40,g15)
    c: Equal(g5,g6)
    c: Equal(g6,g2)
    c: PointOnObject(g39,g31)
FEATURE [PartDesign::Pad] Pad014
  BaseFeature = -> Pocket011
  Direction = (0,0,1)
  Length = 1.2
  Length2 = 10
  Profile = -> Sketch029
  ReferenceAxis = -> Sketch029 [N_Axis]
  Refine = true
  Suppressed = false
  Type = 0
  expr: Length = <<CMProperties>>.cover_thickness
FEATURE [Sketcher::SketchObject] Sketch030
  ArcFitTolerance = 1e-06
  AttachmentSupport = -> [XY_Plane016]
  FullyConstrained = true
  MakeInternals = false
  MapMode = 5
  expr: Constraints[11] = <<CMProperties>>.cm_cover_size
  expr: Constraints[14] = <<LHProperties>>.screw_diameter
  expr: Constraints[71] = <<LHProperties>>.screw_diameter
  sketch-geometry (29):
    g0: LineSegment StartX=-13.2 StartY=-13.2 StartZ=0 EndX=13.2 EndY=-13.2 EndZ=0
    g1: LineSegment StartX=13.2 StartY=-13.2 StartZ=0 EndX=13.2 EndY=13.2 EndZ=0
    g2: LineSegment StartX=13.2 StartY=13.2 StartZ=0 EndX=-13.2 EndY=13.2 EndZ=0
    g3: LineSegment StartX=-13.2 StartY=13.2 StartZ=0 EndX=-13.2 EndY=-13.2 EndZ=0
    g4: GeomPoint [constr] X=0 Y=0 Z=0
    g5: Circle CenterX=-8 CenterY=-8 CenterZ=0 NormalX=0 NormalY=0 NormalZ=1 AngleXU=0 Radius=2.5
    g6: ArcOfCircle CenterX=-9.2 CenterY=6.8 CenterZ=0 NormalX=0 NormalY=0 NormalZ=1 AngleXU=0 Radius=1.5 StartAngle=2.35619 EndAngle=5.49779
    g7: ArcOfCircle CenterX=-6.8 CenterY=9.2 CenterZ=0 NormalX=0 NormalY=0 NormalZ=1 AngleXU=0 Radius=1.5 StartAngle=5.49779 EndAngle=8.63938
    g8: LineSegment StartX=-10.2607 StartY=7.86066 StartZ=0 EndX=-7.86066 EndY=10.2607 EndZ=0
    g9: LineSegment StartX=-8.13934 StartY=5.73934 StartZ=0 EndX=-5.73934 EndY=8.13934 EndZ=0
    g10: ArcOfCircle CenterX=-9.2 CenterY=-1.2 CenterZ=0 NormalX=0 NormalY=0 NormalZ=1 AngleXU=0 Radius=1.5 StartAngle=2.35619 EndAngle=5.49779
    g11: ArcOfCircle CenterX=1.2 CenterY=9.2 CenterZ=0 NormalX=0 NormalY=0 NormalZ=1 AngleXU=0 Radius=1.5 StartAngle=5.49779 EndAngle=8.63938
    g12: LineSegment StartX=-10.2607 StartY=-0.13934 StartZ=0 EndX=0.13934 EndY=10.2607 EndZ=0
    g13: LineSegment StartX=-8.13934 StartY=-2.26066 StartZ=0 EndX=2.26066 EndY=8.13934 EndZ=0
    g14: ArcOfCircle [constr] CenterX=-9.2 CenterY=-9.2 CenterZ=0 NormalX=0 NormalY=0 NormalZ=1 AngleXU=0 Radius=1.5 StartAngle=2.35619 EndAngle=5.49779
    g15: ArcOfCircle CenterX=9.2 CenterY=9.2 CenterZ=0 NormalX=0 NormalY=0 NormalZ=1 AngleXU=0 Radius=1.5 StartAngle=5.49779 EndAngle=8.63938
    g16: LineSegment [constr] StartX=-10.2607 StartY=-8.13934 StartZ=0 EndX=8.13934 EndY=10.2607 EndZ=0
    g17: LineSegment [constr] StartX=-8.13934 StartY=-10.2607 StartZ=0 EndX=10.2607 EndY=8.13934 EndZ=0
    g18: ArcOfCircle CenterX=-1.2 CenterY=-9.2 CenterZ=0 NormalX=0 NormalY=0 NormalZ=1 AngleXU=0 Radius=1.5 StartAngle=2.35619 EndAngle=5.49779
    g19: ArcOfCircle CenterX=9.2 CenterY=1.2 CenterZ=0 NormalX=0 NormalY=0 NormalZ=1 AngleXU=0 Radius=1.5 StartAngle=5.49779 EndAngle=8.63938
    g20: LineSegment StartX=-2.26066 StartY=-8.13934 StartZ=0 EndX=8.13934 EndY=2.26066 EndZ=0
    g21: LineSegment StartX=-0.13934 StartY=-10.2607 StartZ=0 EndX=10.2607 EndY=0.13934 EndZ=0
    g22: ArcOfCircle CenterX=6.8 CenterY=-9.2 CenterZ=0 NormalX=0 NormalY=0 NormalZ=1 AngleXU=0 Radius=1.5 StartAngle=2.35619 EndAngle=5.49779
    g23: ArcOfCircle CenterX=9.2 CenterY=-6.8 CenterZ=0 NormalX=0 NormalY=0 NormalZ=1 AngleXU=0 Radius=1.5 StartAngle=5.49779 EndAngle=8.63938
    g24: LineSegment StartX=5.73934 StartY=-8.13934 StartZ=0 EndX=8.13934 EndY=-5.73934 EndZ=0
    g25: LineSegment StartX=7.86066 StartY=-10.2607 StartZ=0 EndX=10.2607 EndY=-7.86066 EndZ=0
    g26: LineSegment StartX=8.13934 StartY=10.2607 StartZ=0 EndX=-5.68798 EndY=-3.56666 EndZ=0
    g27: LineSegment StartX=10.2607 StartY=8.13934 StartZ=0 EndX=-3.56666 EndY=-5.68798 EndZ=0
    g28: ArcOfCircle CenterX=-8 CenterY=-8 CenterZ=0 NormalX=0 NormalY=0 NormalZ=1 AngleXU=0 Radius=5 StartAngle=0.480706 EndAngle=1.09009
  constraints (72):
    c: Coincident(g0,g1)
    c: Coincident(g1,g2)
    c: Coincident(g2,g3)
    c: Coincident(g3,g0)
    c: Horizontal(g0)
    c: Horizontal(g2)
    c: Vertical(g1)
    c: Vertical(g3)
    c: Symmetric(g2,g0,g4)
    c: Coincident(g4,g-1)
    c: Equal(g2,g1)
    c: DistanceX(g2,g2) = 26.4
    c: DistanceX(g5,g4) = 8
    c: DistanceY(g5,g4) = 8
    c: Diameter(g5) = 5
    c: Tangent(g6,g8) = 1.5708
    c: Tangent(g6,g9) = -1.5708
    c: Tangent(g7,g8) = 1.5708
    c: Tangent(g7,g9) = -1.5708
    c: Equal(g6,g7)
    c: Tangent(g10,g12) = 1.5708
    c: Tangent(g10,g13) = -1.5708
    c: Tangent(g11,g12) = 1.5708
    c: Tangent(g11,g13) = -1.5708
    c: Equal(g10,g11)
    c: Tangent(g14,g16) = 1.5708
    c: Tangent(g14,g17) = -1.5708
    c: Tangent(g15,g16) = 1.5708
    c: Tangent(g15,g17) = -1.5708
    c: Equal(g14,g15)
    c: Tangent(g18,g20) = 1.5708
    c: Tangent(g18,g21) = -1.5708
    c: Tangent(g19,g20) = 1.5708
    c: Tangent(g19,g21) = -1.5708
    c: Equal(g18,g19)
    c: Tangent(g22,g24) = 1.5708
    c: Tangent(g22,g25) = -1.5708
    c: Tangent(g23,g24) = 1.5708
    c: Tangent(g23,g25) = -1.5708
    c: Equal(g22,g23)
    c: Symmetric(g15,g14,g4)
    c: Distance(g15,g15) = 3
    c: Equal(g19,g23)
    c: Equal(g23,g11)
    c: Equal(g11,g7)
    c: Equal(g7,g15)
    c: Horizontal(g15,g11)
    c: Horizontal(g11,g7)
    c: Horizontal(g14,g18)
    c: Horizontal(g14,g22)
    c: Vertical(g14,g10)
    c: Vertical(g14,g6)
    c: Vertical(g15,g19)
    c: Vertical(g15,g23)
    c: Parallel(g9,g13)
    c: Parallel(g13,g17)
    c: Parallel(g17,g21)
    c: Parallel(g21,g25)
    c: DistanceX(g11,g15) = 8
    c: DistanceX(g7,g11) = 8
    c: DistanceY(g19,g15) = 8
    c: DistanceY(g23,g19) = 8
    c: Angle(g-1,g17) = 0.785398
    c: DistanceX(g15,g1) = 4
    c: Coincident(g26,g15)
    c: PointOnObject(g26,g16)
    c: Coincident(g27,g15)
    c: PointOnObject(g27,g17)
    c: Coincident(g28,g5)
    c: Coincident(g28,g27)
    c: Coincident(g28,g26)
    c: Radius(g28) = 5
FEATURE [PartDesign::Pad] Pad015
  Direction = (0,0,1)
  Length = 1.2
  Length2 = 10
  Profile = -> Sketch030
  ReferenceAxis = -> Sketch030 [N_Axis]
  Refine = true
  Suppressed = false
  Type = 0
  expr: Length = <<CMProperties>>.cover_thickness
FEATURE [PartDesign::Body] Body014  label="Cable_Management_Cover"
  AllowCompound = false
  Group = -> [Sketch030,Pad015]
  Origin = -> Origin016
  Tip = -> Pad015
FEATURE [Sketcher::SketchObject] Sketch031
  ArcFitTolerance = 1e-06
  AttachmentSupport = -> [XY_Plane015]
  FullyConstrained = true
  MakeInternals = false
  MapMode = 5
  expr: Constraints[0] = <<LHProperties>>.screw_diameter
  sketch-geometry (1):
    g0: Circle CenterX=-8 CenterY=-8 CenterZ=0 NormalX=0 NormalY=0 NormalZ=1 AngleXU=0 Radius=2.5
  constraints (3):
    c: Diameter(g0) = 5
    c: DistanceX(g0,g-1) = 8
    c: DistanceY(g0,g-1) = 8
FEATURE [PartDesign::Pocket] Pocket012
  BaseFeature = -> Pad014
  Direction = (0,0,-1)
  Length = 5
  Length2 = 5
  Profile = -> Sketch031
  ReferenceAxis = -> Sketch031 [N_Axis]
  Refine = true
  Reversed = true
  Suppressed = false
  Type = 1
FEATURE [PartDesign::Mirrored] Mirrored004
  BaseFeature = -> Pocket012
  MirrorPlane = -> Sketch031 [V_Axis]
  Originals = -> [Pocket012]
  Refine = true
  Suppressed = false
  TransformMode = 0
FEATURE [PartDesign::Mirrored] Mirrored005
  BaseFeature = -> Mirrored004
  MirrorPlane = -> Sketch031 [H_Axis]
  Originals = -> [Pocket012]
  Refine = true
  Suppressed = false
  TransformMode = 0
FEATURE [PartDesign::Body] Body013  label="Cable_Management"
  AllowCompound = false
  Group = -> [Sketch027,Pad013,Sketch028,Pocket011,Sketch029,Pad014,Sketch031,Pocket012,Mirrored004,Mirrored005]
  Origin = -> Origin015
  Tip = -> Mirrored005
FEATURE [TechDraw::DrawProjGroupItem] ProjItem002  label="Bottom"
  CoarseView = false
  Direction = (0,0,-1)
  Focus = 100
  HardHidden = true
  IsoCount = 0
  IsoHidden = false
  IsoVisible = false
  LockPosition = false
  Perspective = false
  Rotation = 0
  RotationVector = (1,0,0)
  ScaleType = 2
  ScrubCount = 1
  SeamHidden = false
  SeamVisible = false
  SmoothHidden = false
  SmoothVisible = true
  Source = -> [Body003]
  Type = 5
  X = 0
  XDirection = (1,0,0)
  Y = -87.3238
FEATURE [TechDraw::DrawProjGroup] ProjGroup
  Anchor = -> View
  AutoDistribute = false
  LockPosition = false
  ProjectionType = 1
  Rotation = 0
  Scale = 0.25
  ScaleType = 0
  Source = -> [Body003]
  Views = -> [View,ProjItem001,ProjItem002]
  X = 141.211
  Y = 227.575
  spacingX = 15
  spacingY = 15
FEATURE [TechDraw::DrawViewDimension] Dimension003
  AngleOverride = false
  Arbitrary = false
  ArbitraryTolerances = false
  BoxCorners = (2) [(-62.5,-37.5,0),(62.5,37.5,0)]
  EqualTolerance = true
  ExtensionAngle = 0
  FormatSpec = %.2w
  FormatSpecOverTolerance = %+.2w
  FormatSpecUnderTolerance = %+.2w
  Inverted = false
  LineAngle = 0
  LockPosition = false
  MeasureType = 1
  OverTolerance = 0
  References2D = -> [ProjItem002]
  Rotation = 0
  Scale = 0.25
  ScaleType = 0
  TheoreticalExact = false
  Type = 1
  UnderTolerance = 0
  X = 0
  Y = 55.4871
FEATURE [TechDraw::DrawViewDimension] Dimension006
  AngleOverride = false
  Arbitrary = false
  ArbitraryTolerances = false
  BoxCorners = (2) [(-62.5,-37.5,0),(62.5,37.5,0)]
  EqualTolerance = true
  ExtensionAngle = 0
  FormatSpec = %.2w
  FormatSpecOverTolerance = %+.2w
  FormatSpecUnderTolerance = %+.2w
  Inverted = false
  LineAngle = 0
  LockPosition = false
  MeasureType = 1
  OverTolerance = 0
  References2D = -> [ProjItem002]
  Rotation = 0
  Scale = 0.25
  ScaleType = 0
  TheoreticalExact = false
  Type = 0
  UnderTolerance = 0
  X = -74.912
  Y = 0
FEATURE [TechDraw::DrawViewDimension] Dimension
  AngleOverride = false
  Arbitrary = false
  ArbitraryTolerances = false
  BoxCorners = (2) [(-62.5,-37.5,0),(62.5,37.5,0)]
  EqualTolerance = true
  ExtensionAngle = 0
  FormatSpec = %.2w
  FormatSpecOverTolerance = %+.2w
  FormatSpecUnderTolerance = %+.2w
  Inverted = false
  LineAngle = 0
  LockPosition = false
  MeasureType = 1
  OverTolerance = 0
  References2D = -> [ProjItem002]
  Rotation = 0
  Scale = 0.25
  ScaleType = 0
  TheoreticalExact = false
  Type = 2
  UnderTolerance = 0
  X = -91.4016
  Y = 0
FEATURE [TechDraw::DrawViewDimension] Dimension008
  AngleOverride = false
  Arbitrary = false
  ArbitraryTolerances = false
  BoxCorners = (2) [(-62.5,-37.5,0),(62.5,37.5,0)]
  EqualTolerance = true
  ExtensionAngle = 0
  FormatSpec = %.2w
  FormatSpecOverTolerance = %+.2w
  FormatSpecUnderTolerance = %+.2w
  Inverted = false
  LineAngle = 0
  LockPosition = false
  MeasureType = 1
  OverTolerance = 0
  References2D = -> [ProjItem002]
  Rotation = 0
  Scale = 0.25
  ScaleType = 0
  TheoreticalExact = false
  Type = 2
  UnderTolerance = 0
  X = 70.8339
  Y = 0
FEATURE [TechDraw::DrawViewDimension] Dimension009
  AngleOverride = false
  Arbitrary = false
  ArbitraryTolerances = false
  BoxCorners = (2) [(-62.5,-37.5,0),(62.5,37.5,0)]
  EqualTolerance = true
  ExtensionAngle = 0
  FormatSpec = ⌀%.2w
  FormatSpecOverTolerance = %+.2w
  FormatSpecUnderTolerance = %+.2w
  Inverted = false
  LineAngle = 0
  LockPosition = false
  MeasureType = 1
  OverTolerance = 0
  References2D = -> [ProjItem002]
  Rotation = 0
  Scale = 0.25
  ScaleType = 0
  TheoreticalExact = false
  Type = 5
  UnderTolerance = 0
  X = -70.0867
  Y = 20.1439
FEATURE [TechDraw::DrawViewDimension] Dimension010
  AngleOverride = false
  Arbitrary = false
  ArbitraryTolerances = false
  BoxCorners = (2) [(-62.5,-37.5,0),(62.5,37.5,0)]
  EqualTolerance = true
  ExtensionAngle = 0
  FormatSpec = ⌀%.2w
  FormatSpecOverTolerance = %+.2w
  FormatSpecUnderTolerance = %+.2w
  Inverted = false
  LineAngle = 0
  LockPosition = false
  MeasureType = 1
  OverTolerance = 0
  References2D = -> [ProjItem002]
  Rotation = 0
  Scale = 0.25
  ScaleType = 0
  TheoreticalExact = false
  Type = 5
  UnderTolerance = 0
  X = 8.42521
  Y = 42.7303
FEATURE [TechDraw::DrawViewDimension] Dimension011
  AngleOverride = false
  Arbitrary = false
  ArbitraryTolerances = false
  BoxCorners = (2) [(-62.5,-37.5,0),(62.5,37.5,0)]
  EqualTolerance = true
  ExtensionAngle = 0
  FormatSpec = %.2w
  FormatSpecOverTolerance = %+.2w
  FormatSpecUnderTolerance = %+.2w
  Inverted = false
  LineAngle = 0
  LockPosition = false
  MeasureType = 1
  OverTolerance = 0
  References2D = -> [ProjItem002]
  Rotation = 0
  Scale = 0.25
  ScaleType = 0
  TheoreticalExact = false
  Type = 1
  UnderTolerance = 0
  X = -45
  Y = 46.1385
FEATURE [TechDraw::DrawViewDimension] Dimension012
  AngleOverride = false
  Arbitrary = false
  ArbitraryTolerances = false
  BoxCorners = (2) [(-62.5,-37.5,0),(62.5,37.5,0)]
  EqualTolerance = true
  ExtensionAngle = 0
  FormatSpec = R%.2w
  FormatSpecOverTolerance = %+.2w
  FormatSpecUnderTolerance = %+.2w
  Inverted = false
  LineAngle = 0
  LockPosition = false
  MeasureType = 1
  OverTolerance = 0
  References2D = -> [ProjItem002]
  Rotation = 0
  Scale = 0.25
  ScaleType = 0
  TheoreticalExact = false
  Type = 4
  UnderTolerance = 0
  X = -72.72
  Y = -16.0202
FEATURE [TechDraw::DrawViewDimension] Dimension013
  AngleOverride = false
  Arbitrary = false
  ArbitraryTolerances = false
  BoxCorners = (2) [(-62.5,-2.125,-1e-07),(62.5,2.125,1e-07)]
  EqualTolerance = true
  ExtensionAngle = 0
  FormatSpec = %.2w
  FormatSpecOverTolerance = %+.2w
  FormatSpecUnderTolerance = %+.2w
  Inverted = false
  LineAngle = 0
  LockPosition = false
  MeasureType = 1
  OverTolerance = 0
  References2D = -> [View]
  Rotation = 0
  Scale = 0.25
  ScaleType = 0
  TheoreticalExact = false
  Type = 0
  UnderTolerance = 0
  X = -61.7213
  Y = -11.2784
FEATURE [TechDraw::DrawViewDimension] Dimension014
  AngleOverride = false
  Arbitrary = false
  ArbitraryTolerances = false
  BoxCorners = (2) [(-62.5,-37.5,0),(62.5,37.5,0)]
  EqualTolerance = true
  ExtensionAngle = 0
  FormatSpec = %.2w
  FormatSpecOverTolerance = %+.2w
  FormatSpecUnderTolerance = %+.2w
  Inverted = false
  LineAngle = 0
  LockPosition = false
  MeasureType = 1
  OverTolerance = 0
  References2D = -> [ProjItem002]
  Rotation = 0
  Scale = 0.25
  ScaleType = 0
  TheoreticalExact = false
  Type = 0
  UnderTolerance = 0
  X = -53.75
  Y = -45.5778
FEATURE [TechDraw::DrawViewDimension] Dimension015
  AngleOverride = false
  Arbitrary = false
  ArbitraryTolerances = false
  BoxCorners = (2) [(-62.5,-37.5,0),(62.5,37.5,0)]
  EqualTolerance = true
  ExtensionAngle = 0
  FormatSpec = %.2w
  FormatSpecOverTolerance = %+.2w
  FormatSpecUnderTolerance = %+.2w
  Inverted = false
  LineAngle = 0
  LockPosition = false
  MeasureType = 1
  OverTolerance = 0
  References2D = -> [ProjItem002]
  Rotation = 0
  Scale = 0.25
  ScaleType = 0
  TheoreticalExact = false
  Type = 0
  UnderTolerance = 0
  X = -34.4281
  Y = -45.5778
FEATURE [TechDraw::DrawViewDimension] Dimension016
  AngleOverride = false
  Arbitrary = false
  ArbitraryTolerances = false
  BoxCorners = (2) [(-62.5,-37.5,0),(62.5,37.5,0)]
  EqualTolerance = true
  ExtensionAngle = 0
  FormatSpec = %.2w
  FormatSpecOverTolerance = %+.2w
  FormatSpecUnderTolerance = %+.2w
  Inverted = false
  LineAngle = 0
  LockPosition = false
  MeasureType = 1
  OverTolerance = 0
  References2D = -> [ProjItem002]
  Rotation = 0
  Scale = 0.25
  ScaleType = 0
  TheoreticalExact = false
  Type = 1
  UnderTolerance = 0
  X = -12.8962
  Y = 46.1385
FEATURE [TechDraw::DrawViewAnnotation] Annotation
  Font = osifont
  LineSpace = 100
  LockPosition = false
  MaxWidth = -1
  Rotation = 0
  Scale = 0.25
  ScaleType = 0
  Text = Changes: | - The joystick's mounting was moved to the bottom |   of the cover, becasue this is how the're meant to be mounted | - The box was made larger due to user feedback stating that | the previous, smaller design made them afraid of missing the strike | face and/or hitting themselves.
  TextSize = 4
  TextStyle = 0
  X = 126.954
  Y = 48.9197
FEATURE [TechDraw::DrawPage] Page  label="Box_Cover_Drawing"
  KeepUpdated = true
  NextBalloonIndex = 1
  ProjectionType = 1
  Scale = 0.25
  Template = -> Template
  Views = -> [ProjGroup,Dimension002,Dimension003,Dimension006,Dimension,Dimension008,Dimension009,Dimension010,Dimension011,Dimension012,Dimension013,Dimension014,Dimension015,Dimension016,Annotation]
FEATURE [TechDraw::DrawSVGTemplate] Template001
  EditableTexts = AuthorName=Alex Anastasakis,CheckDate=2024-11-29,CreationDate=2024-11-26,DrawingNumber=16,FC-Scale=2 : 1,FC-Title=Bracket,SheetNumber=1 / 1,+3 more (map truncated)
  Height = 297
  Orientation = 1
  Template = C:/Program Files/FreeCAD 1.0/data/Mod/TechDraw/Templates/A3_Landscape_TD.svg
  Width = 420
FEATURE [TechDraw::DrawProjGroupItem] View001  label="Front001"
  CoarseView = false
  Direction = (0,-1,0)
  Focus = 100
  HardHidden = true
  IsoCount = 0
  IsoHidden = false
  IsoVisible = false
  LockPosition = true
  Perspective = false
  Rotation = 0
  RotationVector = (1,0,0)
  Scale = 2
  ScaleType = 2
  ScrubCount = 1
  SeamHidden = false
  SeamVisible = false
  SmoothHidden = false
  SmoothVisible = true
  Source = -> [Body]
  Type = 0
  X = 0
  XDirection = (1,0,0)
  Y = 0
FEATURE [TechDraw::DrawProjGroupItem] ProjItem  label="Top"
  CoarseView = false
  Direction = (0,0,1)
  Focus = 100
  HardHidden = true
  IsoCount = 0
  IsoHidden = false
  IsoVisible = false
  LockPosition = false
  Perspective = false
  Rotation = 0
  RotationVector = (1,0,0)
  Scale = 2
  ScaleType = 0
  ScrubCount = 1
  SeamHidden = false
  SeamVisible = false
  SmoothHidden = false
  SmoothVisible = true
  Source = -> [Body]
  Type = 4
  X = 0
  XDirection = (1,0,0)
  Y = 98.0345
FEATURE [TechDraw::DrawProjGroupItem] ProjItem003  label="FrontTopRight001"
  CoarseView = false
  Direction = (0.57735,-0.57735,0.57735)
  Focus = 100
  HardHidden = false
  IsoCount = 0
  IsoHidden = false
  IsoVisible = false
  LockPosition = false
  Perspective = false
  Rotation = 0
  RotationVector = (1,0,0)
  Scale = 2
  ScaleType = 0
  ScrubCount = 1
  SeamHidden = false
  SeamVisible = false
  SmoothHidden = false
  SmoothVisible = true
  Source = -> [Body]
  Type = 7
  X = 142.766
  XDirection = (0.707107,0.707107,0)
  Y = 92.6775
FEATURE [TechDraw::DrawProjGroup] ProjGroup001
  Anchor = -> View001
  AutoDistribute = false
  LockPosition = false
  ProjectionType = 1
  Rotation = 0
  Scale = 2
  ScaleType = 0
  Source = -> [Body]
  Views = -> [View001,ProjItem,ProjItem003]
  X = 148.08
  Y = 118.356
  spacingX = 15
  spacingY = 15
FEATURE [TechDraw::DrawViewDimension] Dimension018
  AngleOverride = false
  Arbitrary = false
  ArbitraryTolerances = false
  BoxCorners = (2) [(-30,-30,0),(30,30,0)]
  EqualTolerance = true
  ExtensionAngle = 0
  FormatSpec = %.2w
  FormatSpecOverTolerance = %+.2w
  FormatSpecUnderTolerance = %+.2w
  Inverted = false
  LineAngle = 0
  LockPosition = false
  MeasureType = 1
  OverTolerance = 0
  References2D = -> [View001]
  Rotation = 0
  Scale = 2
  ScaleType = 0
  TheoreticalExact = false
  Type = 2
  UnderTolerance = 0
  X = -45.9718
  Y = 0
FEATURE [TechDraw::DrawViewDimension] Dimension019
  AngleOverride = false
  Arbitrary = false
  ArbitraryTolerances = false
  BoxCorners = (2) [(-30,-30,0),(30,30,0)]
  EqualTolerance = true
  ExtensionAngle = 0
  FormatSpec = ⌀%.2w
  FormatSpecOverTolerance = %+.2w
  FormatSpecUnderTolerance = %+.2w
  Inverted = false
  LineAngle = 0
  LockPosition = false
  MeasureType = 1
  OverTolerance = 0
  References2D = -> [View001]
  Rotation = 0
  Scale = 2
  ScaleType = 0
  TheoreticalExact = false
  Type = 5
  UnderTolerance = 0
  X = 38.8422
  Y = -14.0191
FEATURE [TechDraw::DrawViewDimension] Dimension021
  AngleOverride = false
  Arbitrary = false
  ArbitraryTolerances = false
  BoxCorners = (2) [(-30,-30,0),(30,30,0)]
  EqualTolerance = true
  ExtensionAngle = 0
  FormatSpec = %.2w
  FormatSpecOverTolerance = %+.2w
  FormatSpecUnderTolerance = %+.2w
  Inverted = false
  LineAngle = 0
  LockPosition = false
  MeasureType = 1
  OverTolerance = 0
  References2D = -> [View001]
  Rotation = 0
  Scale = 2
  ScaleType = 0
  TheoreticalExact = false
  Type = 2
  UnderTolerance = 0
  X = 36.7444
  Y = 23
FEATURE [TechDraw::DrawViewDimension] Dimension022
  AngleOverride = false
  Arbitrary = false
  ArbitraryTolerances = false
  BoxCorners = (2) [(-30,-30,0),(30,30,0)]
  EqualTolerance = true
  ExtensionAngle = 0
  FormatSpec = %.2w
  FormatSpecOverTolerance = %+.2w
  FormatSpecUnderTolerance = %+.2w
  Inverted = false
  LineAngle = 0
  LockPosition = false
  MeasureType = 1
  OverTolerance = 0
  References2D = -> [View001]
  Rotation = 0
  Scale = 2
  ScaleType = 0
  TheoreticalExact = false
  Type = 1
  UnderTolerance = 0
  X = 20
  Y = 40.8906
FEATURE [TechDraw::DrawViewDimension] Dimension023
  AngleOverride = false
  Arbitrary = false
  ArbitraryTolerances = false
  BoxCorners = (2) [(-30,-30,0),(30,30,0)]
  EqualTolerance = true
  ExtensionAngle = 0
  FormatSpec = ⌀%.2w
  FormatSpecOverTolerance = %+.2w
  FormatSpecUnderTolerance = %+.2w
  Inverted = false
  LineAngle = 0
  LockPosition = false
  MeasureType = 1
  OverTolerance = 0
  References2D = -> [ProjItem]
  Rotation = 0
  Scale = 2
  ScaleType = 0
  TheoreticalExact = false
  Type = 5
  UnderTolerance = 0
  X = 42.1363
  Y = 9.98831
FEATURE [TechDraw::DrawViewDimension] Dimension024
  AngleOverride = false
  Arbitrary = false
  ArbitraryTolerances = false
  BoxCorners = (2) [(-30,-30,0),(30,30,0)]
  EqualTolerance = true
  ExtensionAngle = 0
  FormatSpec = %.2w
  FormatSpecOverTolerance = %+.2w
  FormatSpecUnderTolerance = %+.2w
  Inverted = false
  LineAngle = 0
  LockPosition = false
  MeasureType = 1
  OverTolerance = 0
  References2D = -> [ProjItem]
  Rotation = 0
  Scale = 2
  ScaleType = 0
  TheoreticalExact = false
  Type = 2
  UnderTolerance = 0
  X = 40.742
  Y = 26
FEATURE [TechDraw::DrawViewDimension] Dimension025
  AngleOverride = false
  Arbitrary = false
  ArbitraryTolerances = false
  BoxCorners = (2) [(-30,-30,0),(30,30,0)]
  EqualTolerance = true
  ExtensionAngle = 0
  FormatSpec = %.2w
  FormatSpecOverTolerance = %+.2w
  FormatSpecUnderTolerance = %+.2w
  Inverted = false
  LineAngle = 0
  LockPosition = false
  MeasureType = 1
  OverTolerance = 0
  References2D = -> [ProjItem]
  Rotation = 0
  Scale = 2
  ScaleType = 0
  TheoreticalExact = false
  Type = 1
  UnderTolerance = 0
  X = -26
  Y = -36.7876
FEATURE [TechDraw::DrawViewDimension] Dimension026
  AngleOverride = false
  Arbitrary = false
  ArbitraryTolerances = false
  BoxCorners = (2) [(-30,-30,0),(30,30,0)]
  EqualTolerance = true
  ExtensionAngle = 0
  FormatSpec = %.2w
  FormatSpecOverTolerance = %+.2w
  FormatSpecUnderTolerance = %+.2w
  Inverted = false
  LineAngle = 0
  LockPosition = false
  MeasureType = 1
  OverTolerance = 0
  References2D = -> [View001]
  Rotation = 0
  Scale = 2
  ScaleType = 0
  TheoreticalExact = false
  Type = 2
  UnderTolerance = 0
  X = 36.7444
  Y = -26
FEATURE [TechDraw::DrawViewDimension] Dimension028
  AngleOverride = false
  Arbitrary = false
  ArbitraryTolerances = false
  BoxCorners = (2) [(-30,-30,0),(30,30,0)]
  EqualTolerance = true
  ExtensionAngle = 0
  FormatSpec = %.2w
  FormatSpecOverTolerance = %+.2w
  FormatSpecUnderTolerance = %+.2w
  Inverted = false
  LineAngle = 0
  LockPosition = false
  MeasureType = 1
  OverTolerance = 0
  References2D = -> [ProjItem]
  Rotation = 0
  Scale = 2
  ScaleType = 0
  TheoreticalExact = false
  Type = 2
  UnderTolerance = 0
  X = -57.0616
  Y = 0
FEATURE [TechDraw::DrawViewDimension] Dimension029
  AngleOverride = false
  Arbitrary = false
  ArbitraryTolerances = false
  BoxCorners = (2) [(-30,-30,0),(30,30,0)]
  EqualTolerance = true
  ExtensionAngle = 0
  FormatSpec = %.2w
  FormatSpecOverTolerance = %+.2w
  FormatSpecUnderTolerance = %+.2w
  Inverted = false
  LineAngle = 0
  LockPosition = false
  MeasureType = 1
  OverTolerance = 0
  References2D = -> [ProjItem]
  Rotation = 0
  Scale = 2
  ScaleType = 0
  TheoreticalExact = false
  Type = 1
  UnderTolerance = 0
  X = 0
  Y = 52.0352
FEATURE [TechDraw::DrawViewDimension] Dimension030
  AngleOverride = false
  Arbitrary = false
  ArbitraryTolerances = false
  BoxCorners = (2) [(-30,-30,0),(30,30,0)]
  EqualTolerance = true
  ExtensionAngle = 0
  FormatSpec = %.2w
  FormatSpecOverTolerance = %+.2w
  FormatSpecUnderTolerance = %+.2w
  Inverted = false
  LineAngle = 0
  LockPosition = false
  MeasureType = 1
  OverTolerance = 0
  References2D = -> [View001]
  Rotation = 0
  Scale = 2
  ScaleType = 0
  TheoreticalExact = false
  Type = 0
  UnderTolerance = 0
  X = 36.7444
  Y = 4
FEATURE [TechDraw::DrawViewDimension] Dimension031
  AngleOverride = false
  Arbitrary = false
  ArbitraryTolerances = false
  BoxCorners = (2) [(-30,-30,0),(30,30,0)]
  EqualTolerance = true
  ExtensionAngle = 0
  FormatSpec = ⌀%.2w
  FormatSpecOverTolerance = %+.2w
  FormatSpecUnderTolerance = %+.2w
  Inverted = false
  LineAngle = 0
  LockPosition = false
  MeasureType = 1
  OverTolerance = 0
  References2D = -> [View001]
  Rotation = 0
  Scale = 2
  ScaleType = 0
  TheoreticalExact = false
  Type = 5
  UnderTolerance = 0
  X = 1.47224
  Y = 36.2878
FEATURE [TechDraw::DrawViewAnnotation] Annotation001
  Font = osifont
  LineSpace = 100
  LockPosition = false
  MaxWidth = -1
  Rotation = 0
  Scale = 2
  ScaleType = 0
  Text = All chamfers are 1 mm X 45 deg
  TextSize = 4
  TextStyle = 0
  X = 274.735
  Y = 127.356
FEATURE [TechDraw::DrawViewDimension] Dimension032
  AngleOverride = false
  Arbitrary = false
  ArbitraryTolerances = false
  BoxCorners = (2) [(-30,-30,0),(30,30,0)]
  EqualTolerance = true
  ExtensionAngle = 0
  FormatSpec = %.2w
  FormatSpecOverTolerance = %+.2w
  FormatSpecUnderTolerance = %+.2w
  Inverted = false
  LineAngle = 0
  LockPosition = false
  MeasureType = 1
  OverTolerance = 0
  References2D = -> [ProjItem]
  Rotation = 0
  Scale = 2
  ScaleType = 0
  TheoreticalExact = false
  Type = 6
  UnderTolerance = 0
  X = -9.07405
  Y = 42.347
FEATURE [TechDraw::DrawViewDimension] Dimension033
  AngleOverride = false
  Arbitrary = false
  ArbitraryTolerances = false
  BoxCorners = (2) [(-30,-30,0),(30,30,0)]
  EqualTolerance = true
  ExtensionAngle = 0
  FormatSpec = %.2w
  FormatSpecOverTolerance = %+.2w
  FormatSpecUnderTolerance = %+.2w
  Inverted = false
  LineAngle = 0
  LockPosition = false
  MeasureType = 1
  OverTolerance = 0
  References2D = -> [ProjItem]
  Rotation = 0
  Scale = 2
  ScaleType = 0
  TheoreticalExact = false
  Type = 0
  UnderTolerance = 0
  X = -38.9454
  Y = 4.05457
FEATURE [TechDraw::DrawViewDimension] Dimension034
  AngleOverride = false
  Arbitrary = false
  ArbitraryTolerances = false
  BoxCorners = (2) [(-30,-30,0),(30,30,0)]
  EqualTolerance = true
  ExtensionAngle = 0
  FormatSpec = %.2w
  FormatSpecOverTolerance = %+.2w
  FormatSpecUnderTolerance = %+.2w
  Inverted = false
  LineAngle = 0
  LockPosition = false
  MeasureType = 1
  OverTolerance = 0
  References2D = -> [ProjItem]
  Rotation = 0
  Scale = 2
  ScaleType = 0
  TheoreticalExact = false
  Type = 0
  UnderTolerance = 0
  X = 20
  Y = -36.7876
FEATURE [TechDraw::DrawViewDimension] Dimension035
  AngleOverride = false
  Arbitrary = false
  ArbitraryTolerances = false
  BoxCorners = (2) [(-30,-30,0),(30,30,0)]
  EqualTolerance = true
  ExtensionAngle = 0
  FormatSpec = %.2w
  FormatSpecOverTolerance = %+.2w
  FormatSpecUnderTolerance = %+.2w
  Inverted = false
  LineAngle = 0
  LockPosition = false
  MeasureType = 1
  OverTolerance = 0
  References2D = -> [ProjItem]
  Rotation = 0
  Scale = 2
  ScaleType = 0
  TheoreticalExact = false
  Type = 0
  UnderTolerance = 0
  X = 38.3023
  Y = -20
FEATURE [TechDraw::DrawSVGTemplate] Template002
  EditableTexts = AuthorName=AUTHOR NAME,CheckDate=2024-11-29,CreationDate=2024-11-26,DrawingNumber=NUMBER,FC-Scale=1 : 1,FC-Title=LED Housing,SheetNumber=1 / 1,+3 more (map truncated)
  Height = 297
  Orientation = 1
  Template = C:/Program Files/FreeCAD 1.0/data/Mod/TechDraw/Templates/A3_Landscape_TD.svg
  Width = 420
FEATURE [TechDraw::DrawProjGroupItem] View002  label="Front002"
  CoarseView = false
  Direction = (0,-1,0)
  Focus = 100
  HardHidden = true
  IsoCount = 0
  IsoHidden = false
  IsoVisible = false
  LockPosition = true
  Perspective = false
  Rotation = 0
  RotationVector = (1,0,0)
  ScaleType = 2
  ScrubCount = 1
  SeamHidden = false
  SeamVisible = false
  SmoothHidden = false
  SmoothVisible = true
  Source = -> [Body001]
  Type = 0
  X = 0
  XDirection = (1,0,0)
  Y = 0
FEATURE [TechDraw::DrawProjGroupItem] ProjItem005  label="FrontTopRight002"
  CoarseView = false
  Direction = (0.57735,-0.57735,0.57735)
  Focus = 100
  HardHidden = false
  IsoCount = 0
  IsoHidden = false
  IsoVisible = false
  LockPosition = false
  Perspective = false
  Rotation = 0
  RotationVector = (1,0,0)
  ScaleType = 0
  ScrubCount = 1
  SeamHidden = false
  SeamVisible = false
  SmoothHidden = false
  SmoothVisible = true
  Source = -> [Body001]
  Type = 7
  X = 224.191
  XDirection = (0.707107,0.707107,0)
  Y = -114.97
FEATURE [TechDraw::DrawProjGroupItem] ProjItem006  label="Right"
  CoarseView = false
  Direction = (1,-1e-16,0)
  Focus = 100
  HardHidden = true
  IsoCount = 0
  IsoHidden = false
  IsoVisible = false
  LockPosition = false
  Perspective = false
  Rotation = 0
  RotationVector = (1,0,0)
  ScaleType = 0
  ScrubCount = 1
  SeamHidden = false
  SeamVisible = false
  SmoothHidden = false
  SmoothVisible = true
  Source = -> [Body001]
  Type = 2
  X = 149.461
  XDirection = (1e-16,1,0)
  Y = 0
FEATURE [TechDraw::DrawProjGroupItem] ProjItem007  label="Bottom001"
  CoarseView = false
  Direction = (0,0,-1)
  Focus = 100
  HardHidden = true
  IsoCount = 0
  IsoHidden = false
  IsoVisible = false
  LockPosition = false
  Perspective = false
  Rotation = 0
  RotationVector = (1,0,0)
  ScaleType = 0
  ScrubCount = 1
  SeamHidden = false
  SeamVisible = false
  SmoothHidden = false
  SmoothVisible = true
  Source = -> [Body001]
  Type = 5
  X = 0
  XDirection = (1,0,0)
  Y = -132.319
FEATURE [TechDraw::DrawProjGroup] ProjGroup002
  Anchor = -> View002
  AutoDistribute = false
  LockPosition = false
  ProjectionType = 1
  Rotation = 0
  ScaleType = 0
  Source = -> [Body001]
  Views = -> [View002,ProjItem005,ProjItem006,ProjItem007]
  X = 105.391
  Y = 244.152
  spacingX = 15
  spacingY = 15
FEATURE [TechDraw::DrawViewDimension] Dimension037
  AngleOverride = false
  Arbitrary = false
  ArbitraryTolerances = false
  BoxCorners = (2) [(-27.5,-82,0),(27.5,82,0)]
  EqualTolerance = true
  ExtensionAngle = 0
  FormatSpec = %.2w
  FormatSpecOverTolerance = %+.2w
  FormatSpecUnderTolerance = %+.2w
  Inverted = false
  LineAngle = 0
  LockPosition = false
  MeasureType = 1
  OverTolerance = 0
  References2D = -> [ProjItem007]
  Rotation = 0
  ScaleType = 0
  TheoreticalExact = false
  Type = 2
  UnderTolerance = 0
  X = -44.0471
  Y = 0
FEATURE [TechDraw::DrawViewDimension] Dimension038
  AngleOverride = false
  Arbitrary = false
  ArbitraryTolerances = false
  BoxCorners = (2) [(-27.5,-82,0),(27.5,82,0)]
  EqualTolerance = true
  ExtensionAngle = 0
  FormatSpec = %.2w
  FormatSpecOverTolerance = %+.2w
  FormatSpecUnderTolerance = %+.2w
  Inverted = false
  LineAngle = 0
  LockPosition = false
  MeasureType = 1
  OverTolerance = 0
  References2D = -> [ProjItem007]
  Rotation = 0
  ScaleType = 0
  TheoreticalExact = false
  Type = 2
  UnderTolerance = 0
  X = 34.3761
  Y = 54.5
FEATURE [TechDraw::DrawViewDimension] Dimension039
  AngleOverride = false
  Arbitrary = false
  ArbitraryTolerances = false
  BoxCorners = (2) [(-27.5,-82,0),(27.5,82,0)]
  EqualTolerance = true
  ExtensionAngle = 0
  FormatSpec = %.2w
  FormatSpecOverTolerance = %+.2w
  FormatSpecUnderTolerance = %+.2w
  Inverted = false
  LineAngle = 0
  LockPosition = false
  MeasureType = 1
  OverTolerance = 0
  References2D = -> [ProjItem007]
  Rotation = 0
  ScaleType = 0
  TheoreticalExact = false
  Type = 1
  UnderTolerance = 0
  X = 0
  Y = 91.678
FEATURE [TechDraw::DrawViewDimension] Dimension041
  AngleOverride = false
  Arbitrary = false
  ArbitraryTolerances = false
  BoxCorners = (2) [(-27.5,-82,0),(27.5,82,0)]
  EqualTolerance = true
  ExtensionAngle = 0
  FormatSpec = %.2w
  FormatSpecOverTolerance = %+.2w
  FormatSpecUnderTolerance = %+.2w
  Inverted = false
  LineAngle = 0
  LockPosition = false
  MeasureType = 1
  OverTolerance = 0
  References2D = -> [ProjItem007]
  Rotation = 0
  ScaleType = 0
  TheoreticalExact = false
  Type = 2
  UnderTolerance = 0
  X = 34.3761
  Y = 69.9495
FEATURE [TechDraw::DrawViewDimension] Dimension042
  AngleOverride = false
  Arbitrary = false
  ArbitraryTolerances = false
  BoxCorners = (2) [(-27.5,-82,0),(27.5,82,0)]
  EqualTolerance = true
  ExtensionAngle = 0
  FormatSpec = %.2w
  FormatSpecOverTolerance = %+.2w
  FormatSpecUnderTolerance = %+.2w
  Inverted = false
  LineAngle = 0
  LockPosition = false
  MeasureType = 1
  OverTolerance = 0
  References2D = -> [ProjItem007]
  Rotation = 0
  ScaleType = 0
  TheoreticalExact = false
  Type = 1
  UnderTolerance = 0
  X = 14.1071
  Y = 91.678
FEATURE [TechDraw::DrawViewDimension] Dimension044
  AngleOverride = false
  Arbitrary = false
  ArbitraryTolerances = false
  BoxCorners = (2) [(-27.5,-82,0),(27.5,82,0)]
  EqualTolerance = true
  ExtensionAngle = 0
  FormatSpec = %.2w
  FormatSpecOverTolerance = %+.2w
  FormatSpecUnderTolerance = %+.2w
  Inverted = false
  LineAngle = 0
  LockPosition = false
  MeasureType = 1
  OverTolerance = 0
  References2D = -> [ProjItem007]
  Rotation = 0
  ScaleType = 0
  TheoreticalExact = false
  Type = 0
  UnderTolerance = 0
  X = 17.3738
  Y = -85.4539
FEATURE [TechDraw::DrawViewDimension] Dimension045
  AngleOverride = false
  Arbitrary = false
  ArbitraryTolerances = false
  BoxCorners = (2) [(-27.5,-82,0),(27.5,82,0)]
  EqualTolerance = true
  ExtensionAngle = 0
  FormatSpec = %.2w
  FormatSpecOverTolerance = %+.2w
  FormatSpecUnderTolerance = %+.2w
  Inverted = false
  LineAngle = 0
  LockPosition = false
  MeasureType = 1
  OverTolerance = 0
  References2D = -> [ProjItem007]
  Rotation = 0
  ScaleType = 0
  TheoreticalExact = false
  Type = 0
  UnderTolerance = 0
  X = 17.593
  Y = -92.4539
FEATURE [TechDraw::DrawViewDimension] Dimension048
  AngleOverride = false
  Arbitrary = false
  ArbitraryTolerances = false
  BoxCorners = (2) [(-82,-15,0),(82,15,0)]
  EqualTolerance = true
  ExtensionAngle = 0
  FormatSpec = %.2w
  FormatSpecOverTolerance = %+.2w
  FormatSpecUnderTolerance = %+.2w
  Inverted = false
  LineAngle = 0
  LockPosition = false
  MeasureType = 1
  OverTolerance = 0
  References2D = -> [ProjItem006]
  Rotation = 0
  ScaleType = 0
  TheoreticalExact = false
  Type = 1
  UnderTolerance = 0
  X = -28.6
  Y = -23.2807
FEATURE [TechDraw::DrawViewDimension] Dimension049
  AngleOverride = false
  Arbitrary = false
  ArbitraryTolerances = false
  BoxCorners = (2) [(-82,-15,0),(82,15,0)]
  EqualTolerance = true
  ExtensionAngle = 0
  FormatSpec = %.2w
  FormatSpecOverTolerance = %+.2w
  FormatSpecUnderTolerance = %+.2w
  Inverted = false
  LineAngle = 0
  LockPosition = false
  MeasureType = 1
  OverTolerance = 0
  References2D = -> [ProjItem006]
  Rotation = 0
  ScaleType = 0
  TheoreticalExact = false
  Type = 0
  UnderTolerance = 0
  X = -40.6021
  Y = -26.8949
FEATURE [TechDraw::DrawViewDimension] Dimension050
  AngleOverride = false
  Arbitrary = false
  ArbitraryTolerances = false
  BoxCorners = (2) [(-82,-15,0),(82,15,0)]
  EqualTolerance = true
  ExtensionAngle = 0
  FormatSpec = %.2w
  FormatSpecOverTolerance = %+.2w
  FormatSpecUnderTolerance = %+.2w
  Inverted = false
  LineAngle = 0
  LockPosition = false
  MeasureType = 1
  OverTolerance = 0
  References2D = -> [ProjItem006]
  Rotation = 0
  ScaleType = 0
  TheoreticalExact = false
  Type = 0
  UnderTolerance = 0
  X = -47.6021
  Y = -26.8949
FEATURE [TechDraw::DrawViewDimension] Dimension051
  AngleOverride = false
  Arbitrary = false
  ArbitraryTolerances = false
  BoxCorners = (2) [(-82,-15,0),(82,15,0)]
  EqualTolerance = true
  ExtensionAngle = 0
  FormatSpec = %.2w
  FormatSpecOverTolerance = %+.2w
  FormatSpecUnderTolerance = %+.2w
  Inverted = false
  LineAngle = 0
  LockPosition = false
  MeasureType = 1
  OverTolerance = 0
  References2D = -> [ProjItem006]
  Rotation = 0
  ScaleType = 0
  TheoreticalExact = false
  Type = 0
  UnderTolerance = 0
  X = -54.6021
  Y = -26.7886
FEATURE [TechDraw::DrawViewDimension] Dimension052
  AngleOverride = false
  Arbitrary = false
  ArbitraryTolerances = false
  BoxCorners = (2) [(-27.5,-15,0),(27.5,15,0)]
  EqualTolerance = true
  ExtensionAngle = 0
  FormatSpec = %.2w
  FormatSpecOverTolerance = %+.2w
  FormatSpecUnderTolerance = %+.2w
  Inverted = false
  LineAngle = 0
  LockPosition = false
  MeasureType = 1
  OverTolerance = 0
  References2D = -> [View002]
  Rotation = 0
  ScaleType = 0
  TheoreticalExact = false
  Type = 1
  UnderTolerance = 0
  X = 0
  Y = -23.5042
FEATURE [TechDraw::DrawViewDimension] Dimension053
  AngleOverride = false
  Arbitrary = false
  ArbitraryTolerances = false
  BoxCorners = (2) [(-27.5,-15,0),(27.5,15,0)]
  EqualTolerance = true
  ExtensionAngle = 0
  FormatSpec = %.2w
  FormatSpecOverTolerance = %+.2w
  FormatSpecUnderTolerance = %+.2w
  Inverted = false
  LineAngle = 0
  LockPosition = false
  MeasureType = 1
  OverTolerance = 0
  References2D = -> [View002]
  Rotation = 0
  ScaleType = 0
  TheoreticalExact = false
  Type = 2
  UnderTolerance = 0
  X = 19.0941
  Y = -1.5
FEATURE [TechDraw::DrawViewDimension] Dimension054
  AngleOverride = false
  Arbitrary = false
  ArbitraryTolerances = false
  BoxCorners = (2) [(-27.5,-15,0),(27.5,15,0)]
  EqualTolerance = true
  ExtensionAngle = 0
  FormatSpec = %.2w
  FormatSpecOverTolerance = %+.2w
  FormatSpecUnderTolerance = %+.2w
  Inverted = false
  LineAngle = 0
  LockPosition = false
  MeasureType = 1
  OverTolerance = 0
  References2D = -> [View002]
  Rotation = 0
  ScaleType = 0
  TheoreticalExact = false
  Type = 1
  UnderTolerance = 0
  X = 0
  Y = 29.8724
FEATURE [TechDraw::DrawViewDimension] Dimension055
  AngleOverride = false
  Arbitrary = false
  ArbitraryTolerances = false
  BoxCorners = (2) [(-27.5,-15,0),(27.5,15,0)]
  EqualTolerance = true
  ExtensionAngle = 0
  FormatSpec = %.2w
  FormatSpecOverTolerance = %+.2w
  FormatSpecUnderTolerance = %+.2w
  Inverted = false
  LineAngle = 0
  LockPosition = false
  MeasureType = 1
  OverTolerance = 0
  References2D = -> [View002]
  Rotation = 0
  ScaleType = 0
  TheoreticalExact = false
  Type = 1
  UnderTolerance = 0
  X = 0
  Y = 22.8724
FEATURE [TechDraw::DrawViewDimension] Dimension056
  AngleOverride = false
  Arbitrary = false
  ArbitraryTolerances = false
  BoxCorners = (2) [(-27.5,-15,0),(27.5,15,0)]
  EqualTolerance = true
  ExtensionAngle = 0
  FormatSpec = %.2w
  FormatSpecOverTolerance = %+.2w
  FormatSpecUnderTolerance = %+.2w
  Inverted = false
  LineAngle = 0
  LockPosition = false
  MeasureType = 1
  OverTolerance = 0
  References2D = -> [View002]
  Rotation = 0
  ScaleType = 0
  TheoreticalExact = false
  Type = 0
  UnderTolerance = 0
  X = -34.2369
  Y = 6.12343
FEATURE [TechDraw::DrawViewDimension] Dimension057
  AngleOverride = false
  Arbitrary = false
  ArbitraryTolerances = false
  BoxCorners = (2) [(-27.5,-15,0),(27.5,15,0)]
  EqualTolerance = true
  ExtensionAngle = 0
  FormatSpec = %.2w
  FormatSpecOverTolerance = %+.2w
  FormatSpecUnderTolerance = %+.2w
  Inverted = false
  LineAngle = 0
  LockPosition = false
  MeasureType = 1
  OverTolerance = 0
  References2D = -> [View002]
  Rotation = 0
  ScaleType = 0
  TheoreticalExact = false
  Type = 2
  UnderTolerance = 0
  X = 33.551
  Y = 8.53954
FEATURE [TechDraw::DrawViewDimension] Dimension058
  AngleOverride = false
  Arbitrary = false
  ArbitraryTolerances = false
  BoxCorners = (2) [(-27.5,-82,0),(27.5,82,0)]
  EqualTolerance = true
  ExtensionAngle = 0
  FormatSpec = %.2w
  FormatSpecOverTolerance = %+.2w
  FormatSpecUnderTolerance = %+.2w
  Inverted = false
  LineAngle = 0
  LockPosition = false
  MeasureType = 1
  OverTolerance = 0
  References2D = -> [ProjItem007]
  Rotation = 0
  ScaleType = 0
  TheoreticalExact = false
  Type = 0
  UnderTolerance = 0
  X = 44.4291
  Y = 41.4549
FEATURE [TechDraw::DrawViewDimension] Dimension059
  AngleOverride = false
  Arbitrary = false
  ArbitraryTolerances = false
  BoxCorners = (2) [(-82,-15,0),(82,15,0)]
  EqualTolerance = true
  ExtensionAngle = 0
  FormatSpec = %.2w
  FormatSpecOverTolerance = %+.2w
  FormatSpecUnderTolerance = %+.2w
  Inverted = false
  LineAngle = 0
  LockPosition = false
  MeasureType = 1
  OverTolerance = 0
  References2D = -> [ProjItem006]
  Rotation = 0
  ScaleType = 0
  TheoreticalExact = false
  Type = 1
  UnderTolerance = 0
  X = 0
  Y = -32.2503
FEATURE [TechDraw::DrawViewDimension] Dimension060
  AngleOverride = false
  Arbitrary = false
  ArbitraryTolerances = false
  BoxCorners = (2) [(-82,-15,0),(82,15,0)]
  EqualTolerance = true
  ExtensionAngle = 0
  FormatSpec = %.2w
  FormatSpecOverTolerance = %+.2w
  FormatSpecUnderTolerance = %+.2w
  Inverted = false
  LineAngle = 0
  LockPosition = false
  MeasureType = 1
  OverTolerance = 0
  References2D = -> [ProjItem006]
  Rotation = 0
  ScaleType = 0
  TheoreticalExact = false
  Type = 1
  UnderTolerance = 0
  X = 0
  Y = 26.882
FEATURE [TechDraw::DrawViewAnnotation] Annotation002
  Font = osifont
  LineSpace = 100
  LockPosition = false
  MaxWidth = -1
  Rotation = 0
  Scale = 2
  ScaleType = 0
  Text = Changes: | Simple redesign. Minor adjustments of measurements
  TextSize = 4
  TextStyle = 0
  X = 126.965
  Y = 51.269
FEATURE [TechDraw::DrawPage] Page001  label="Bracket_Drawing"
  KeepUpdated = true
  NextBalloonIndex = 1
  ProjectionType = 1
  Scale = 2
  Template = -> Template001
  Views = -> [ProjGroup001,Dimension018,Dimension019,Dimension021,Dimension022,Dimension023,Dimension024,Dimension025,Dimension026,Dimension028,Dimension029,Dimension030,Dimension031,Annotation001,Dimension032,Dimension033,Dimension034,Dimension035,Annotation002]
FEATURE [TechDraw::DrawViewAnnotation] Annotation003
  Font = osifont
  LineSpace = 100
  LockPosition = false
  MaxWidth = -1
  Rotation = 0
  ScaleType = 0
  Text = Changes: | Removed the latches because  | it wouldn't print properly, and simple | redesign with small adjustments to values.
  TextSize = 4
  TextStyle = 0
  X = 203.38
  Y = 98.0412
FEATURE [TechDraw::DrawPage] Page002  label="LED_Housing_Drawing"
  KeepUpdated = true
  NextBalloonIndex = 1
  ProjectionType = 1
  Template = -> Template002
  Views = -> [ProjGroup002,Dimension037,Dimension038,Dimension039,Dimension041,Dimension042,Dimension044,Dimension045,Dimension048,Dimension049,Dimension050,Dimension051,Dimension052,Dimension053,Dimension054,Dimension055,Dimension056,Dimension057,Dimension058,Dimension059,Dimension060,Annotation003]
FEATURE [TechDraw::DrawSVGTemplate] Template003
  EditableTexts = CreationDate=2 : 1,Designed_by_Name=Alex Anastasakis,Drawing_number=Drawing number,FC-Date=2024-11-26,FC-SC=4 : 1,FC-SH=1 / 1,FC-Title=Latch,+3 more (map truncated)
  Height = 210
  Orientation = 1
  Template = C:/Program Files/FreeCAD 1.0/data/Mod/TechDraw/Templates/A4_Landscape_TD.svg
  Width = 297
FEATURE [TechDraw::DrawProjGroupItem] View004  label="Front003"
  CoarseView = false
  Direction = (0,-1,0)
  Focus = 100
  HardHidden = true
  IsoCount = 0
  IsoHidden = false
  IsoVisible = false
  LockPosition = true
  Perspective = false
  Rotation = 0
  RotationVector = (1,0,0)
  Scale = 4
  ScaleType = 2
  ScrubCount = 1
  SeamHidden = false
  SeamVisible = false
  SmoothHidden = false
  SmoothVisible = true
  Source = -> [Body002]
  Type = 0
  X = 0
  XDirection = (1,0,0)
  Y = 0
FEATURE [TechDraw::DrawProjGroupItem] ProjItem011  label="Right001"
  CoarseView = false
  Direction = (1,-1e-16,0)
  Focus = 100
  HardHidden = true
  IsoCount = 0
  IsoHidden = false
  IsoVisible = false
  LockPosition = false
  Perspective = false
  Rotation = 0
  RotationVector = (1,0,0)
  ScaleType = 2
  ScrubCount = 1
  SeamHidden = false
  SeamVisible = false
  SmoothHidden = false
  SmoothVisible = true
  Source = -> [Body002]
  Type = 2
  X = 63.3033
  XDirection = (1e-16,1,0)
  Y = 0
FEATURE [TechDraw::DrawProjGroupItem] ProjItem012  label="FrontTopRight003"
  CoarseView = false
  Direction = (0.57735,-0.57735,0.57735)
  Focus = 100
  HardHidden = false
  IsoCount = 0
  IsoHidden = false
  IsoVisible = false
  LockPosition = false
  Perspective = false
  Rotation = 0
  RotationVector = (1,0,0)
  ScaleType = 2
  ScrubCount = 1
  SeamHidden = false
  SeamVisible = false
  SmoothHidden = false
  SmoothVisible = true
  Source = -> [Body002]
  Type = 7
  X = 136.574
  XDirection = (0.707107,0.707107,0)
  Y = 23.6198
FEATURE [TechDraw::DrawProjGroup] ProjGroup003
  Anchor = -> View004
  AutoDistribute = false
  LockPosition = false
  ProjectionType = 1
  Rotation = 0
  Scale = 4
  ScaleType = 0
  Source = -> [Body002]
  Views = -> [View004,ProjItem011,ProjItem012]
  X = 96.2991
  Y = 117.661
  spacingX = 15
  spacingY = 15
FEATURE [TechDraw::DrawViewDimension] Dimension061
  AngleOverride = false
  Arbitrary = false
  ArbitraryTolerances = false
  BoxCorners = (2) [(-5.26318,-43.6,0),(5.26318,43.6,0)]
  EqualTolerance = true
  ExtensionAngle = 0
  FormatSpec = %.2w
  FormatSpecOverTolerance = %+.2w
  FormatSpecUnderTolerance = %+.2w
  Inverted = false
  LineAngle = 0
  LockPosition = false
  MeasureType = 1
  OverTolerance = 0
  References2D = -> [View004]
  Rotation = 0
  Scale = 4
  ScaleType = 0
  TheoreticalExact = false
  Type = 1
  UnderTolerance = 0
  X = -2.86318
  Y = 49.9982
FEATURE [TechDraw::DrawViewDimension] Dimension065
  AngleOverride = false
  Arbitrary = false
  ArbitraryTolerances = false
  BoxCorners = (2) [(-5.26318,-43.6,0),(5.26318,43.6,0)]
  EqualTolerance = true
  ExtensionAngle = 0
  FormatSpec = %.2w
  FormatSpecOverTolerance = %+.2w
  FormatSpecUnderTolerance = %+.2w
  Inverted = false
  LineAngle = 0
  LockPosition = false
  MeasureType = 1
  OverTolerance = 0
  References2D = -> [View004]
  Rotation = 0
  Scale = 4
  ScaleType = 0
  TheoreticalExact = false
  Type = 0
  UnderTolerance = 0
  X = 7.49395
  Y = -48.5091
FEATURE [TechDraw::DrawViewDimension] Dimension066
  AngleOverride = false
  Arbitrary = false
  ArbitraryTolerances = false
  BoxCorners = (2) [(-16,-43.6,-1e-07),(16,43.6,1e-07)]
  EqualTolerance = true
  ExtensionAngle = 0
  FormatSpec = %.2w
  FormatSpecOverTolerance = %+.2w
  FormatSpecUnderTolerance = %+.2w
  Inverted = false
  LineAngle = 0
  LockPosition = false
  MeasureType = 1
  OverTolerance = 0
  References2D = -> [ProjItem011]
  Rotation = 0
  Scale = 4
  ScaleType = 0
  TheoreticalExact = false
  Type = 1
  UnderTolerance = 0
  X = 0
  Y = 51.3064
FEATURE [TechDraw::DrawViewDimension] Dimension067
  AngleOverride = false
  Arbitrary = false
  ArbitraryTolerances = false
  BoxCorners = (2) [(-16,-43.6,-1e-07),(16,43.6,1e-07)]
  EqualTolerance = true
  ExtensionAngle = 0
  FormatSpec = %.2w
  FormatSpecOverTolerance = %+.2w
  FormatSpecUnderTolerance = %+.2w
  Inverted = false
  LineAngle = 0
  LockPosition = false
  MeasureType = 1
  OverTolerance = 0
  References2D = -> [ProjItem011]
  Rotation = 0
  Scale = 4
  ScaleType = 0
  TheoreticalExact = false
  Type = 2
  UnderTolerance = 0
  X = -30.8417
  Y = 0
FEATURE [TechDraw::DrawViewDimension] Dimension068
  AngleOverride = false
  Arbitrary = false
  ArbitraryTolerances = false
  BoxCorners = (2) [(-16,-43.6,-1e-07),(16,43.6,1e-07)]
  EqualTolerance = true
  ExtensionAngle = 0
  FormatSpec = %.2w
  FormatSpecOverTolerance = %+.2w
  FormatSpecUnderTolerance = %+.2w
  Inverted = false
  LineAngle = 0
  LockPosition = false
  MeasureType = 1
  OverTolerance = 0
  References2D = -> [ProjItem011]
  Rotation = 0
  Scale = 4
  ScaleType = 0
  TheoreticalExact = false
  Type = 2
  UnderTolerance = 0
  X = -23.8417
  Y = 19.6
FEATURE [TechDraw::DrawViewDimension] Dimension069
  AngleOverride = false
  Arbitrary = false
  ArbitraryTolerances = false
  BoxCorners = (2) [(-5.26318,-43.6,0),(5.26318,43.6,0)]
  EqualTolerance = true
  ExtensionAngle = 0
  FormatSpec = %.2w
  FormatSpecOverTolerance = %+.2w
  FormatSpecUnderTolerance = %+.2w
  Inverted = false
  LineAngle = 0
  LockPosition = false
  MeasureType = 1
  OverTolerance = 0
  References2D = -> [View004]
  Rotation = 0
  Scale = 4
  ScaleType = 0
  TheoreticalExact = false
  Type = 0
  UnderTolerance = 0
  X = 13.6167
  Y = 2.26741
FEATURE [TechDraw::DrawSVGTemplate] Template004
  EditableTexts = AuthorName=Alex Anastasakis,CreationDate=2 : 1,Designed_by_Name=Alex Anastasakis,Drawing_number=Drawing number,FC-Date=2024-11-26,FC-SC=2 : 1,+6 more (map truncated)
  Height = 210
  Orientation = 1
  Template = C:/Program Files/FreeCAD 1.0/data/Mod/TechDraw/Templates/A4_Landscape_TD.svg
  Width = 297
FEATURE [TechDraw::DrawProjGroupItem] View005  label="Front004"
  CoarseView = false
  Direction = (0,-1,0)
  Focus = 100
  HardHidden = true
  IsoCount = 0
  IsoHidden = false
  IsoVisible = false
  LockPosition = true
  Perspective = false
  Rotation = 0
  RotationVector = (1,0,0)
  Scale = 2
  ScaleType = 2
  ScrubCount = 1
  SeamHidden = false
  SeamVisible = false
  SmoothHidden = false
  SmoothVisible = true
  Source = -> [Body013]
  Type = 0
  X = 0
  XDirection = (1,0,0)
  Y = 0
FEATURE [TechDraw::DrawProjGroupItem] ProjItem013  label="Top001"
  CoarseView = false
  Direction = (0,0,1)
  Focus = 100
  HardHidden = true
  IsoCount = 0
  IsoHidden = false
  IsoVisible = false
  LockPosition = false
  Perspective = false
  Rotation = 0
  RotationVector = (1,0,0)
  Scale = 2
  ScaleType = 0
  ScrubCount = 1
  SeamHidden = false
  SeamVisible = false
  SmoothHidden = false
  SmoothVisible = true
  Source = -> [Body013]
  Type = 4
  X = 0
  XDirection = (1,0,0)
  Y = 83.7291
FEATURE [TechDraw::DrawProjGroupItem] ProjItem014  label="FrontTopRight004"
  CoarseView = false
  Direction = (0.57735,-0.57735,0.57735)
  Focus = 100
  HardHidden = false
  IsoCount = 0
  IsoHidden = false
  IsoVisible = false
  LockPosition = false
  Perspective = false
  Rotation = 0
  RotationVector = (1,0,0)
  Scale = 2
  ScaleType = 0
  ScrubCount = 1
  SeamHidden = false
  SeamVisible = false
  SmoothHidden = false
  SmoothVisible = true
  Source = -> [Body013]
  Type = 7
  X = 113.853
  XDirection = (0.707107,0.707107,0)
  Y = 82.9065
FEATURE [TechDraw::DrawProjGroup] ProjGroup004
  Anchor = -> View005
  AutoDistribute = false
  LockPosition = false
  ProjectionType = 1
  Rotation = 0
  Scale = 2
  ScaleType = 0
  Source = -> [Body013]
  Views = -> [View005,ProjItem013,ProjItem014]
  X = 97.0488
  Y = 52.794
  spacingX = 15
  spacingY = 15
FEATURE [TechDraw::DrawViewDimension] Dimension070
  AngleOverride = false
  Arbitrary = false
  ArbitraryTolerances = false
  BoxCorners = (2) [(-30,-30,0),(30,30,0)]
  EqualTolerance = true
  ExtensionAngle = 0
  FormatSpec = %.2w
  FormatSpecOverTolerance = %+.2w
  FormatSpecUnderTolerance = %+.2w
  Inverted = false
  LineAngle = 0
  LockPosition = false
  MeasureType = 1
  OverTolerance = 0
  References2D = -> [ProjItem013]
  Rotation = 0
  Scale = 2
  ScaleType = 0
  TheoreticalExact = false
  Type = 1
  UnderTolerance = 0
  X = 0
  Y = 50.724
FEATURE [TechDraw::DrawViewDimension] Dimension071
  AngleOverride = false
  Arbitrary = false
  ArbitraryTolerances = false
  BoxCorners = (2) [(-30,-30,0),(30,30,0)]
  EqualTolerance = true
  ExtensionAngle = 0
  FormatSpec = %.2w
  FormatSpecOverTolerance = %+.2w
  FormatSpecUnderTolerance = %+.2w
  Inverted = false
  LineAngle = 0
  LockPosition = false
  MeasureType = 1
  OverTolerance = 0
  References2D = -> [ProjItem013]
  Rotation = 0
  Scale = 2
  ScaleType = 0
  TheoreticalExact = false
  Type = 2
  UnderTolerance = 0
  X = 44.8824
  Y = 0
FEATURE [TechDraw::DrawViewDimension] Dimension072
  AngleOverride = false
  Arbitrary = false
  ArbitraryTolerances = false
  BoxCorners = (2) [(-30,-30,0),(30,30,0)]
  EqualTolerance = true
  ExtensionAngle = 0
  FormatSpec = R%.2w
  FormatSpecOverTolerance = %+.2w
  FormatSpecUnderTolerance = %+.2w
  Inverted = false
  LineAngle = 0
  LockPosition = false
  MeasureType = 1
  OverTolerance = 0
  References2D = -> [ProjItem013]
  Rotation = 0
  Scale = 2
  ScaleType = 0
  TheoreticalExact = false
  Type = 4
  UnderTolerance = 0
  X = -1.35497
  Y = 36.9182
FEATURE [TechDraw::DrawViewDimension] Dimension073
  AngleOverride = false
  Arbitrary = false
  ArbitraryTolerances = false
  BoxCorners = (2) [(-30,-30,0),(30,30,0)]
  EqualTolerance = true
  ExtensionAngle = 0
  FormatSpec = R%.2w
  FormatSpecOverTolerance = %+.2w
  FormatSpecUnderTolerance = %+.2w
  Inverted = false
  LineAngle = 0
  LockPosition = false
  MeasureType = 1
  OverTolerance = 0
  References2D = -> [ProjItem013]
  Rotation = 0
  Scale = 2
  ScaleType = 0
  TheoreticalExact = false
  Type = 4
  UnderTolerance = 0
  X = 23.1023
  Y = 36.8365
FEATURE [TechDraw::DrawViewDimension] Dimension078
  AngleOverride = false
  Arbitrary = false
  ArbitraryTolerances = false
  BoxCorners = (2) [(-30,-30,0),(30,30,0)]
  EqualTolerance = true
  ExtensionAngle = 0
  FormatSpec = %.2w
  FormatSpecOverTolerance = %+.2w
  FormatSpecUnderTolerance = %+.2w
  Inverted = false
  LineAngle = 0
  LockPosition = false
  MeasureType = 1
  OverTolerance = 0
  References2D = -> [ProjItem013]
  Rotation = 0
  Scale = 2
  ScaleType = 0
  TheoreticalExact = false
  Type = 0
  UnderTolerance = 0
  X = -37.4197
  Y = -10.0479
FEATURE [TechDraw::DrawViewDimension] Dimension080
  AngleOverride = false
  Arbitrary = false
  ArbitraryTolerances = false
  BoxCorners = (2) [(-30,-30,0),(30,30,0)]
  EqualTolerance = true
  ExtensionAngle = 0
  FormatSpec = %.2w
  FormatSpecOverTolerance = %+.2w
  FormatSpecUnderTolerance = %+.2w
  Inverted = false
  LineAngle = 0
  LockPosition = false
  MeasureType = 1
  OverTolerance = 0
  References2D = -> [ProjItem013]
  Rotation = 0
  Scale = 2
  ScaleType = 0
  TheoreticalExact = false
  Type = 2
  UnderTolerance = 0
  X = -44.4197
  Y = -35.8344
FEATURE [TechDraw::DrawViewDimension] Dimension082
  AngleOverride = false
  Arbitrary = false
  ArbitraryTolerances = false
  BoxCorners = (2) [(-30,-30,0),(30,30,0)]
  EqualTolerance = true
  ExtensionAngle = 0
  FormatSpec = %.2w
  FormatSpecOverTolerance = %+.2w
  FormatSpecUnderTolerance = %+.2w
  Inverted = false
  LineAngle = 0
  LockPosition = false
  MeasureType = 1
  OverTolerance = 0
  References2D = -> [ProjItem013]
  Rotation = 0
  Scale = 2
  ScaleType = 0
  TheoreticalExact = false
  Type = 0
  UnderTolerance = 0
  X = -23
  Y = -43.8014
FEATURE [TechDraw::DrawViewDimension] Dimension083
  AngleOverride = false
  Arbitrary = false
  ArbitraryTolerances = false
  BoxCorners = (2) [(-30,-30,0),(30,30,0)]
  EqualTolerance = true
  ExtensionAngle = 0
  FormatSpec = %.2w
  FormatSpecOverTolerance = %+.2w
  FormatSpecUnderTolerance = %+.2w
  Inverted = false
  LineAngle = 0
  LockPosition = false
  MeasureType = 1
  OverTolerance = 0
  References2D = -> [ProjItem013]
  Rotation = 0
  Scale = 2
  ScaleType = 0
  TheoreticalExact = false
  Type = 0
  UnderTolerance = 0
  X = -49.804
  Y = -23
FEATURE [TechDraw::DrawViewDimension] Dimension084
  AngleOverride = false
  Arbitrary = false
  ArbitraryTolerances = false
  BoxCorners = (2) [(-30,-30,0),(30,30,0)]
  EqualTolerance = true
  ExtensionAngle = 0
  FormatSpec = ⌀%.2w
  FormatSpecOverTolerance = %+.2w
  FormatSpecUnderTolerance = %+.2w
  Inverted = false
  LineAngle = 0
  LockPosition = false
  MeasureType = 1
  OverTolerance = 0
  References2D = -> [ProjItem013]
  Rotation = 0
  Scale = 2
  ScaleType = 0
  TheoreticalExact = false
  Type = 5
  UnderTolerance = 0
  X = 0.589568
  Y = -37.6167
FEATURE [TechDraw::DrawViewDimension] Dimension087
  AngleOverride = false
  Arbitrary = false
  ArbitraryTolerances = false
  BoxCorners = (2) [(-30,-5.9,-1e-07),(30,5.9,1e-07)]
  EqualTolerance = true
  ExtensionAngle = 0
  FormatSpec = %.2w
  FormatSpecOverTolerance = %+.2w
  FormatSpecUnderTolerance = %+.2w
  Inverted = false
  LineAngle = 0
  LockPosition = false
  MeasureType = 1
  OverTolerance = 0
  References2D = -> [View005]
  Rotation = 0
  Scale = 2
  ScaleType = 0
  TheoreticalExact = false
  Type = 2
  UnderTolerance = 0
  X = -44.1557
  Y = 0
FEATURE [TechDraw::DrawViewDimension] Dimension090
  AngleOverride = false
  Arbitrary = false
  ArbitraryTolerances = false
  BoxCorners = (2) [(-30,-5.9,-1e-07),(30,5.9,1e-07)]
  EqualTolerance = true
  ExtensionAngle = 0
  FormatSpec = %.2w
  FormatSpecOverTolerance = %+.2w
  FormatSpecUnderTolerance = %+.2w
  Inverted = false
  LineAngle = 0
  LockPosition = false
  MeasureType = 1
  OverTolerance = 0
  References2D = -> [View005]
  Rotation = 0
  Scale = 2
  ScaleType = 0
  TheoreticalExact = false
  Type = 2
  UnderTolerance = 0
  X = 35.5248
  Y = 0
FEATURE [TechDraw::DrawViewDimension] Dimension091
  AngleOverride = false
  Arbitrary = false
  ArbitraryTolerances = false
  BoxCorners = (2) [(-30,-5.9,-1e-07),(30,5.9,1e-07)]
  EqualTolerance = true
  ExtensionAngle = 0
  FormatSpec = %.2w
  FormatSpecOverTolerance = %+.2w
  FormatSpecUnderTolerance = %+.2w
  Inverted = false
  LineAngle = 0
  LockPosition = false
  MeasureType = 1
  OverTolerance = 0
  References2D = -> [View005]
  Rotation = 0
  Scale = 2
  ScaleType = 0
  TheoreticalExact = false
  Type = 1
  UnderTolerance = 0
  X = 0
  Y = 13.1067
FEATURE [TechDraw::DrawViewDimension] Dimension092
  AngleOverride = false
  Arbitrary = false
  ArbitraryTolerances = false
  BoxCorners = (2) [(-30,-5.9,-1e-07),(30,5.9,1e-07)]
  EqualTolerance = true
  ExtensionAngle = 0
  FormatSpec = %.2w
  FormatSpecOverTolerance = %+.2w
  FormatSpecUnderTolerance = %+.2w
  Inverted = false
  LineAngle = 0
  LockPosition = false
  MeasureType = 1
  OverTolerance = 0
  References2D = -> [View005]
  Rotation = 0
  Scale = 2
  ScaleType = 0
  TheoreticalExact = false
  Type = 2
  UnderTolerance = 0
  X = -37.1557
  Y = -10.6609
FEATURE [TechDraw::DrawViewDimension] Dimension093
  AngleOverride = false
  Arbitrary = false
  ArbitraryTolerances = false
  BoxCorners = (2) [(-30,-30,0),(30,30,0)]
  EqualTolerance = true
  ExtensionAngle = 0
  FormatSpec = %.2w
  FormatSpecOverTolerance = %+.2w
  FormatSpecUnderTolerance = %+.2w
  Inverted = false
  LineAngle = 0
  LockPosition = false
  MeasureType = 1
  OverTolerance = 0
  References2D = -> [ProjItem013]
  Rotation = 0
  Scale = 2
  ScaleType = 0
  TheoreticalExact = false
  Type = 0
  UnderTolerance = 0
  X = -51.4197
  Y = -15
FEATURE [TechDraw::DrawSVGTemplate] Template005
  EditableTexts = Designed_by_Name=Alex Anastasakis,Drawing_number=Drawing number,FC-Date=2024-11-26,FC-SC=3 : 1,FC-SH=1 / 1,FC-Title=Cable Lock Lid,+3 more (map truncated)
  Height = 210
  Orientation = 1
  Template = C:/Program Files/FreeCAD 1.0/data/Mod/TechDraw/Templates/A4_Landscape_TD.svg
  Width = 297
FEATURE [TechDraw::DrawProjGroupItem] View006  label="Front005"
  CoarseView = false
  Direction = (0,-1,0)
  Focus = 100
  HardHidden = true
  IsoCount = 0
  IsoHidden = false
  IsoVisible = false
  LockPosition = true
  Perspective = false
  Rotation = 0
  RotationVector = (1,0,0)
  Scale = 3
  ScaleType = 2
  ScrubCount = 1
  SeamHidden = false
  SeamVisible = false
  SmoothHidden = false
  SmoothVisible = true
  Source = -> [Body014]
  Type = 0
  X = 0
  XDirection = (1,0,0)
  Y = 0
FEATURE [TechDraw::DrawProjGroupItem] ProjItem015  label="Top002"
  CoarseView = false
  Direction = (0,0,1)
  Focus = 100
  HardHidden = true
  IsoCount = 0
  IsoHidden = false
  IsoVisible = false
  LockPosition = false
  Perspective = false
  Rotation = 0
  RotationVector = (1,0,0)
  Scale = 3
  ScaleType = 0
  ScrubCount = 1
  SeamHidden = false
  SeamVisible = false
  SmoothHidden = false
  SmoothVisible = true
  Source = -> [Body014]
  Type = 4
  X = 0
  XDirection = (1,0,0)
  Y = 75.7792
FEATURE [TechDraw::DrawProjGroupItem] ProjItem016  label="FrontTopRight005"
  CoarseView = false
  Direction = (0.57735,-0.57735,0.57735)
  Focus = 100
  HardHidden = false
  IsoCount = 0
  IsoHidden = false
  IsoVisible = false
  LockPosition = false
  Perspective = false
  Rotation = 0
  RotationVector = (1,0,0)
  Scale = 3
  ScaleType = 0
  ScrubCount = 1
  SeamHidden = false
  SeamVisible = false
  SmoothHidden = false
  SmoothVisible = true
  Source = -> [Body014]
  Type = 7
  X = 128.391
  XDirection = (0.707107,0.707107,0)
  Y = 92.4685
FEATURE [TechDraw::DrawProjGroup] ProjGroup005
  Anchor = -> View006
  AutoDistribute = false
  LockPosition = false
  ProjectionType = 1
  Rotation = 0
  Scale = 3
  ScaleType = 0
  Source = -> [Body014]
  Views = -> [View006,ProjItem015,ProjItem016]
  X = 92.5371
  Y = 52.8184
  spacingX = 15
  spacingY = 15
FEATURE [TechDraw::DrawViewDimension] Dimension094
  AngleOverride = false
  Arbitrary = false
  ArbitraryTolerances = false
  BoxCorners = (2) [(-39.6,-1.8,0),(39.6,1.8,0)]
  EqualTolerance = true
  ExtensionAngle = 0
  FormatSpec = %.2w
  FormatSpecOverTolerance = %+.2w
  FormatSpecUnderTolerance = %+.2w
  Inverted = false
  LineAngle = 0
  LockPosition = false
  MeasureType = 1
  OverTolerance = 0
  References2D = -> [View006]
  Rotation = 0
  Scale = 3
  ScaleType = 0
  TheoreticalExact = false
  Type = 2
  UnderTolerance = 0
  X = -52.3806
  Y = -5.40391
FEATURE [TechDraw::DrawViewDimension] Dimension095
  AngleOverride = false
  Arbitrary = false
  ArbitraryTolerances = false
  BoxCorners = (2) [(-39.6,-39.6,0),(39.6,39.6,0)]
  EqualTolerance = true
  ExtensionAngle = 0
  FormatSpec = %.2w
  FormatSpecOverTolerance = %+.2w
  FormatSpecUnderTolerance = %+.2w
  Inverted = false
  LineAngle = 0
  LockPosition = false
  MeasureType = 1
  OverTolerance = 0
  References2D = -> [ProjItem015]
  Rotation = 0
  Scale = 3
  ScaleType = 0
  TheoreticalExact = false
  Type = 2
  UnderTolerance = 0
  X = -56.1134
  Y = 0
FEATURE [TechDraw::DrawViewDimension] Dimension096
  AngleOverride = false
  Arbitrary = false
  ArbitraryTolerances = false
  BoxCorners = (2) [(-39.6,-39.6,0),(39.6,39.6,0)]
  EqualTolerance = true
  ExtensionAngle = 0
  FormatSpec = %.2w
  FormatSpecOverTolerance = %+.2w
  FormatSpecUnderTolerance = %+.2w
  Inverted = false
  LineAngle = 0
  LockPosition = false
  MeasureType = 1
  OverTolerance = 0
  References2D = -> [ProjItem015]
  Rotation = 0
  Scale = 3
  ScaleType = 0
  TheoreticalExact = false
  Type = 1
  UnderTolerance = 0
  X = 0
  Y = -47.964
FEATURE [TechDraw::DrawViewDimension] Dimension098
  AngleOverride = false
  Arbitrary = false
  ArbitraryTolerances = false
  BoxCorners = (2) [(-39.6,-39.6,0),(39.6,39.6,0)]
  EqualTolerance = true
  ExtensionAngle = 0
  FormatSpec = R%.2w
  FormatSpecOverTolerance = %+.2w
  FormatSpecUnderTolerance = %+.2w
  Inverted = false
  LineAngle = 0
  LockPosition = false
  MeasureType = 1
  OverTolerance = 0
  References2D = -> [ProjItem015]
  Rotation = 0
  Scale = 3
  ScaleType = 0
  TheoreticalExact = false
  Type = 4
  UnderTolerance = 0
  X = 44.7394
  Y = 23.0806
FEATURE [TechDraw::DrawViewDimension] Dimension099
  AngleOverride = false
  Arbitrary = false
  ArbitraryTolerances = false
  BoxCorners = (2) [(-39.6,-39.6,0),(39.6,39.6,0)]
  EqualTolerance = true
  ExtensionAngle = 0
  FormatSpec = R%.2w
  FormatSpecOverTolerance = %+.2w
  FormatSpecUnderTolerance = %+.2w
  Inverted = false
  LineAngle = 0
  LockPosition = false
  MeasureType = 1
  OverTolerance = 0
  References2D = -> [ProjItem015]
  Rotation = 0
  Scale = 3
  ScaleType = 0
  TheoreticalExact = false
  Type = 4
  UnderTolerance = 0
  X = 23.7665
  Y = 49.9581
FEATURE [TechDraw::DrawViewDimension] Dimension100
  AngleOverride = false
  Arbitrary = false
  ArbitraryTolerances = false
  BoxCorners = (2) [(-39.6,-39.6,0),(39.6,39.6,0)]
  EqualTolerance = true
  ExtensionAngle = 0
  FormatSpec = %.2w
  FormatSpecOverTolerance = %+.2w
  FormatSpecUnderTolerance = %+.2w
  Inverted = false
  LineAngle = 0
  LockPosition = false
  MeasureType = 1
  OverTolerance = 0
  References2D = -> [ProjItem015]
  Rotation = 0
  Scale = 3
  ScaleType = 0
  TheoreticalExact = false
  Type = 0
  UnderTolerance = 0
  X = 48.6166
  Y = 48.6166
FEATURE [TechDraw::DrawViewDimension] Dimension101
  AngleOverride = false
  Arbitrary = false
  ArbitraryTolerances = false
  BoxCorners = (2) [(-39.6,-39.6,0),(39.6,39.6,0)]
  EqualTolerance = true
  ExtensionAngle = 0
  FormatSpec = ⌀%.2w
  FormatSpecOverTolerance = %+.2w
  FormatSpecUnderTolerance = %+.2w
  Inverted = false
  LineAngle = 0
  LockPosition = false
  MeasureType = 1
  OverTolerance = 0
  References2D = -> [ProjItem015]
  Rotation = 0
  Scale = 3
  ScaleType = 0
  TheoreticalExact = false
  Type = 5
  UnderTolerance = 0
  X = -45.7348
  Y = -5.58759
FEATURE [TechDraw::DrawViewDimension] Dimension104
  AngleOverride = false
  Arbitrary = false
  ArbitraryTolerances = false
  BoxCorners = (2) [(-39.6,-39.6,0),(39.6,39.6,0)]
  EqualTolerance = true
  ExtensionAngle = 0
  FormatSpec = %.2w
  FormatSpecOverTolerance = %+.2w
  FormatSpecUnderTolerance = %+.2w
  Inverted = false
  LineAngle = 0
  LockPosition = false
  MeasureType = 1
  OverTolerance = 0
  References2D = -> [ProjItem015]
  Rotation = 0
  Scale = 3
  ScaleType = 0
  TheoreticalExact = false
  Type = 0
  UnderTolerance = 0
  X = 33.6
  Y = 52.7842
FEATURE [TechDraw::DrawViewDimension] Dimension105
  AngleOverride = false
  Arbitrary = false
  ArbitraryTolerances = false
  BoxCorners = (2) [(-39.6,-39.6,0),(39.6,39.6,0)]
  EqualTolerance = true
  ExtensionAngle = 0
  FormatSpec = %.2w
  FormatSpecOverTolerance = %+.2w
  FormatSpecUnderTolerance = %+.2w
  Inverted = false
  LineAngle = 0
  LockPosition = false
  MeasureType = 1
  OverTolerance = 0
  References2D = -> [ProjItem015]
  Rotation = 0
  Scale = 3
  ScaleType = 0
  TheoreticalExact = false
  Type = 0
  UnderTolerance = 0
  X = 47.2063
  Y = 33.6
FEATURE [TechDraw::DrawViewDimension] Dimension106
  AngleOverride = false
  Arbitrary = false
  ArbitraryTolerances = false
  BoxCorners = (2) [(-39.6,-39.6,0),(39.6,39.6,0)]
  EqualTolerance = true
  ExtensionAngle = 0
  FormatSpec = %.2w
  FormatSpecOverTolerance = %+.2w
  FormatSpecUnderTolerance = %+.2w
  Inverted = false
  LineAngle = 0
  LockPosition = false
  MeasureType = 1
  OverTolerance = 0
  References2D = -> [ProjItem015]
  Rotation = 0
  Scale = 3
  ScaleType = 0
  TheoreticalExact = false
  Type = 0
  UnderTolerance = 0
  X = -31.8
  Y = -43.6073
FEATURE [TechDraw::DrawViewDimension] Dimension107
  AngleOverride = false
  Arbitrary = false
  ArbitraryTolerances = false
  BoxCorners = (2) [(-39.6,-39.6,0),(39.6,39.6,0)]
  EqualTolerance = true
  ExtensionAngle = 0
  FormatSpec = %.2w
  FormatSpecOverTolerance = %+.2w
  FormatSpecUnderTolerance = %+.2w
  Inverted = false
  LineAngle = 0
  LockPosition = false
  MeasureType = 1
  OverTolerance = 0
  References2D = -> [ProjItem015]
  Rotation = 0
  Scale = 3
  ScaleType = 0
  TheoreticalExact = false
  Type = 0
  UnderTolerance = 0
  X = -46.2627
  Y = -31.8
FEATURE [TechDraw::DrawViewDimension] Dimension108
  AngleOverride = false
  Arbitrary = false
  ArbitraryTolerances = false
  BoxCorners = (2) [(-39.6,-39.6,0),(39.6,39.6,0)]
  EqualTolerance = true
  ExtensionAngle = 0
  FormatSpec = %.2w
  FormatSpecOverTolerance = %+.2w
  FormatSpecUnderTolerance = %+.2w
  Inverted = false
  LineAngle = 0
  LockPosition = false
  MeasureType = 1
  OverTolerance = 0
  References2D = -> [ProjItem015]
  Rotation = 0
  Scale = 3
  ScaleType = 0
  TheoreticalExact = false
  Type = 0
  UnderTolerance = 0
  X = -33.6
  Y = 50.4089
FEATURE [TechDraw::DrawViewDimension] Dimension109
  AngleOverride = false
  Arbitrary = false
  ArbitraryTolerances = false
  BoxCorners = (2) [(-39.6,-39.6,0),(39.6,39.6,0)]
  EqualTolerance = true
  ExtensionAngle = 0
  FormatSpec = %.2w
  FormatSpecOverTolerance = %+.2w
  FormatSpecUnderTolerance = %+.2w
  Inverted = false
  LineAngle = 0
  LockPosition = false
  MeasureType = 1
  OverTolerance = 0
  References2D = -> [ProjItem015]
  Rotation = 0
  Scale = 3
  ScaleType = 0
  TheoreticalExact = false
  Type = 0
  UnderTolerance = 0
  X = 47.2063
  Y = -33.6
FEATURE [TechDraw::DrawPage] Page005  label="Cable_Lock_Lid_Drawing"
  KeepUpdated = true
  NextBalloonIndex = 1
  ProjectionType = 1
  Scale = 3
  Template = -> Template005
  Views = -> [ProjGroup005,Dimension094,Dimension095,Dimension096,Dimension098,Dimension099,Dimension100,Dimension101,Dimension104,Dimension105,Dimension106,Dimension107,Dimension108,Dimension109]
FEATURE [TechDraw::DrawViewDimension] Dimension110
  AngleOverride = false
  Arbitrary = false
  ArbitraryTolerances = false
  BoxCorners = (2) [(-30,-30,0),(30,30,0)]
  EqualTolerance = true
  ExtensionAngle = 0
  FormatSpec = %.2w
  FormatSpecOverTolerance = %+.2w
  FormatSpecUnderTolerance = %+.2w
  Inverted = false
  LineAngle = 0
  LockPosition = false
  MeasureType = 1
  OverTolerance = 0
  References2D = -> [ProjItem013]
  Rotation = 0
  Scale = 2
  ScaleType = 0
  TheoreticalExact = false
  Type = 0
  UnderTolerance = 0
  X = -21
  Y = 43.724
FEATURE [TechDraw::DrawViewDimension] Dimension111
  AngleOverride = false
  Arbitrary = false
  ArbitraryTolerances = false
  BoxCorners = (2) [(-30,-30,0),(30,30,0)]
  EqualTolerance = true
  ExtensionAngle = 0
  FormatSpec = %.1w
  FormatSpecOverTolerance = %+.2w
  FormatSpecUnderTolerance = %+.2w
  Inverted = false
  LineAngle = 0
  LockPosition = false
  MeasureType = 1
  OverTolerance = 0
  References2D = -> [ProjItem013]
  Rotation = 0
  Scale = 2
  ScaleType = 0
  TheoreticalExact = false
  Type = 0
  UnderTolerance = 0
  X = -44.4197
  Y = 21.0143
FEATURE [TechDraw::DrawViewDimension] Dimension081
  AngleOverride = false
  Arbitrary = false
  ArbitraryTolerances = false
  BoxCorners = (2) [(-30,-30,0),(30,30,0)]
  EqualTolerance = true
  ExtensionAngle = 0
  FormatSpec = %.2w
  FormatSpecOverTolerance = %+.2w
  FormatSpecUnderTolerance = %+.2w
  Inverted = false
  LineAngle = 0
  LockPosition = false
  MeasureType = 1
  OverTolerance = 0
  References2D = -> [ProjItem013]
  Rotation = 0
  Scale = 2
  ScaleType = 0
  TheoreticalExact = false
  Type = 1
  UnderTolerance = 0
  X = -22.1992
  Y = -36.8014
FEATURE [TechDraw::DrawPage] Page004  label="Cable_Lock_Drawing"
  KeepUpdated = true
  NextBalloonIndex = 1
  ProjectionType = 1
  Scale = 2
  Template = -> Template004
  Views = -> [ProjGroup004,Dimension070,Dimension071,Dimension072,Dimension073,Dimension078,Dimension080,Dimension081,Dimension082,Dimension083,Dimension084,Dimension087,Dimension090,Dimension091,Dimension092,Dimension093,Dimension110,Dimension111]
FEATURE [TechDraw::DrawViewDimension] Dimension112
  AngleOverride = false
  Arbitrary = false
  ArbitraryTolerances = false
  BoxCorners = (2) [(-5.26318,-43.6,0),(5.26318,43.6,0)]
  EqualTolerance = true
  ExtensionAngle = 0
  FormatSpec = 4× R%.2w
  FormatSpecOverTolerance = %+.2w
  FormatSpecUnderTolerance = %+.2w
  Inverted = false
  LineAngle = 0
  LockPosition = false
  MeasureType = 1
  OverTolerance = 0
  References2D = -> [View004]
  Rotation = 0
  Scale = 4
  ScaleType = 0
  TheoreticalExact = false
  Type = 4
  UnderTolerance = 0
  X = 23.0402
  Y = -12.0045
FEATURE [TechDraw::DrawPage] Page003  label="Latch_Drawing"
  KeepUpdated = true
  NextBalloonIndex = 1
  ProjectionType = 1
  Scale = 4
  Template = -> Template003
  Views = -> [ProjGroup003,Dimension061,Dimension065,Dimension066,Dimension067,Dimension068,Dimension069,Dimension112]
FEATURE [PartDesign::AdditiveCylinder] Cylinder003
  Angle = 360
  AttacherType = Attacher::AttachEngine3D
  AttachmentOffset = pos=(0,54.5,0) rot=(0,0,1;0rad)
  AttachmentSupport = -> [XY_Plane021]
  FirstAngle = 0
  Height = 1.2
  MapMode = 5
  Placement = pos=(0,54.5,0) rot=(0,0,1;0rad)
  Radius = 4.85
  Refine = true
  SecondAngle = 0
  Suppressed = false
  expr: .AttachmentOffset.Base.y = -<<LHProperties>>.led_dim / 2 + <<LHProperties>>.led_housing_base_length / 2 - <<LHProperties>>.led_array_housing_spacing
FEATURE [Sketcher::SketchObject] Sketch037
  ArcFitTolerance = 1e-06
  AttachmentSupport = -> [XY_Plane021]
  ExternalGeometry = -> [Cylinder003]
  FullyConstrained = true
  MakeInternals = false
  MapMode = 5
  sketch-geometry (13):
    g0: LineSegment StartX=-4 StartY=54.5 StartZ=0 EndX=-4 EndY=-54.5 EndZ=0
    g1: LineSegment StartX=-4 StartY=-54.5 StartZ=0 EndX=-2.5 EndY=-54.5 EndZ=0
    g2: LineSegment StartX=-2.5 StartY=-54.5 StartZ=0 EndX=-2.5 EndY=54.5 EndZ=0
    g3: LineSegment StartX=-2.5 StartY=54.5 StartZ=0 EndX=-4 EndY=54.5 EndZ=0
    g4: LineSegment StartX=4 StartY=54.5 StartZ=0 EndX=4 EndY=-54.5 EndZ=0
    g5: LineSegment StartX=4 StartY=-54.5 StartZ=0 EndX=2.5 EndY=-54.5 EndZ=0
    g6: LineSegment StartX=2.5 StartY=-54.5 StartZ=0 EndX=2.5 EndY=54.5 EndZ=0
    g7: LineSegment StartX=2.5 StartY=54.5 StartZ=0 EndX=4 EndY=54.5 EndZ=0
    g8: LineSegment StartX=0.75 StartY=-54.5 StartZ=0 EndX=0.75 EndY=54.5 EndZ=0
    g9: LineSegment StartX=0.75 StartY=54.5 StartZ=0 EndX=-0.75 EndY=54.5 EndZ=0
    g10: LineSegment StartX=-0.75 StartY=54.5 StartZ=0 EndX=-0.75 EndY=-54.5 EndZ=0
    g11: LineSegment StartX=-0.75 StartY=-54.5 StartZ=0 EndX=0.75 EndY=-54.5 EndZ=0
    g12: GeomPoint [constr] X=0 Y=0 Z=0
  constraints (35):
    c: Coincident(g0,g1)
    c: Coincident(g1,g2)
    c: Coincident(g2,g3)
    c: Coincident(g3,g0)
    c: Vertical(g0)
    c: Vertical(g2)
    c: Horizontal(g1)
    c: Horizontal(g3)
    c: Coincident(g4,g5)
    c: Coincident(g5,g6)
    c: Coincident(g6,g7)
    c: Coincident(g7,g4)
    c: Vertical(g4)
    c: Horizontal(g5)
    c: Horizontal(g7)
    c: Equal(g4,g2)
    c: Equal(g7,g3)
    c: Horizontal(g2,g-3)
    c: Horizontal(g4,g-3)
    c: DistanceX(g3,g3) = 1.5
    c: DistanceX(g0,g-3) = 4
    c: DistanceX(g-3,g4) = 4
    c: Symmetric(g6,g5,g-1)
    c: Coincident(g8,g9)
    c: Coincident(g9,g10)
    c: Coincident(g10,g11)
    c: Coincident(g11,g8)
    c: Vertical(g8)
    c: Vertical(g10)
    c: Horizontal(g9)
    c: Horizontal(g11)
    c: Symmetric(g10,g8,g12)
    c: Coincident(g12,g-1)
    c: PointOnObject(g-3,g9)
    c: Equal(g9,g3)
FEATURE [PartDesign::Pad] Pad020
  BaseFeature = -> Cylinder003
  Direction = (0,0,1)
  Length = 1
  Length2 = 10
  Placement = pos=(0,54.5,0) rot=(0,0,1;0rad)
  Profile = -> Sketch037
  ReferenceAxis = -> Sketch037 [N_Axis]
  Refine = true
  Reversed = true
  Suppressed = false
  Type = 0
FEATURE [Sketcher::SketchObject] Sketch038
  ArcFitTolerance = 1e-06
  AttachmentSupport = -> [XY_Plane022]
  FullyConstrained = true
  MakeInternals = false
  MapMode = 5
  sketch-geometry (5):
    g0: LineSegment StartX=-4.85 StartY=-4.85 StartZ=0 EndX=4.85 EndY=-4.85 EndZ=0
    g1: LineSegment StartX=4.85 StartY=-4.85 StartZ=0 EndX=4.85 EndY=4.85 EndZ=0
    g2: LineSegment StartX=4.85 StartY=4.85 StartZ=0 EndX=-4.85 EndY=4.85 EndZ=0
    g3: LineSegment StartX=-4.85 StartY=4.85 StartZ=0 EndX=-4.85 EndY=-4.85 EndZ=0
    g4: GeomPoint [constr] X=0 Y=0 Z=0
  constraints (12):
    c: Coincident(g0,g1)
    c: Coincident(g1,g2)
    c: Coincident(g2,g3)
    c: Coincident(g3,g0)
    c: Horizontal(g0)
    c: Horizontal(g2)
    c: Vertical(g1)
    c: Vertical(g3)
    c: Symmetric(g2,g0,g4)
    c: Coincident(g4,g-1)
    c: Equal(g1,g2)
    c: DistanceX(g2,g2) = 9.7
FEATURE [PartDesign::Pad] Pad021
  Direction = (0,0,1)
  Length = 8
  Length2 = 10
  Midplane = true
  Profile = -> Sketch038
  ReferenceAxis = -> Sketch038 [N_Axis]
  Refine = true
  Suppressed = false
  Type = 0
FEATURE [PartDesign::Body] Body020  label="LED_Housing_Cube"
  AllowCompound = false
  Group = -> [Sketch038,Pad021]
  Origin = -> Origin022
  Tip = -> Pad021
FEATURE [Part::FeaturePython] Screw  label="#5x5/8in-Screw"  # WARN: FeaturePython — macro-defined, semantics opaque (R4)
  Diameter = 6
  Invert = false
  LeftHanded = false
  Length = 2
  LengthCustom = 15.875
  MatchOuter = false
  OffsetAngle = 0
  Thread = true
  Type = 15
FEATURE [Part::FeaturePython] Screw002  label="1/4inx1in-Screw"  # WARN: FeaturePython — macro-defined, semantics opaque (R4)
  Diameter = 11
  Invert = false
  LeftHanded = false
  Length = 4
  LengthCustom = 25.4
  MatchOuter = false
  OffsetAngle = 0
  Placement = pos=(0,0,119) rot=(0,0,1;0rad)
  Thread = true
  Type = 20
FEATURE [Part::FeaturePython] Nut  label="1/4in-Nut"  # WARN: FeaturePython — macro-defined, semantics opaque (R4)
  Diameter = 1
  Invert = false
  LeftHanded = false
  MatchOuter = false
  OffsetAngle = 0
  Thread = true
  Type = 6
FEATURE [Sketcher::SketchObject] Sketch039
  ArcFitTolerance = 1e-06
  AttachmentSupport = -> [XY_Plane023]
  FullyConstrained = true
  MakeInternals = false
  MapMode = 5
  sketch-geometry (2):
    g0: Circle CenterX=0 CenterY=0 CenterZ=0 NormalX=0 NormalY=0 NormalZ=1 AngleXU=0 Radius=8
    g1: Circle CenterX=0 CenterY=0 CenterZ=0 NormalX=0 NormalY=0 NormalZ=1 AngleXU=0 Radius=28
  constraints (4):
    c: Coincident(g0,g-1)
    c: Coincident(g1,g0)
    c: Diameter(g0) = 16
    c: Diameter(g1) = 56
FEATURE [PartDesign::Pad] Pad022
  Direction = (0,0,1)
  Length = 1.6
  Length2 = 10
  Profile = -> Sketch039
  ReferenceAxis = -> Sketch039 [N_Axis]
  Refine = true
  Suppressed = false
  Type = 0
FEATURE [PartDesign::Body] Body021  label="Joystick_hole_cover"
  AllowCompound = false
  Group = -> [Sketch039,Pad022]
  Origin = -> Origin023
  Tip = -> Pad022
FEATURE [Sketcher::SketchObject] Sketch040
  ArcFitTolerance = 1e-06
  AttachmentSupport = -> [XZ_Plane024]
  FullyConstrained = false
  MakeInternals = false
  MapMode = 5
  Placement = pos=(0,0,0) rot=(1,0,0;1.5708rad)
  sketch-geometry (10):
    g0: LineSegment StartX=5.8 StartY=1 StartZ=0 EndX=5.8 EndY=3.5 EndZ=0
    g1: LineSegment StartX=5.8 StartY=3.5 StartZ=0 EndX=2 EndY=3.5 EndZ=0
    g2: LineSegment StartX=2 StartY=3.5 StartZ=0 EndX=2 EndY=6 EndZ=0
    g3: LineSegment StartX=2 StartY=6 StartZ=0 EndX=12.5 EndY=6 EndZ=0
    g4: LineSegment StartX=7.60102 StartY=0 StartZ=0 EndX=6.8 EndY=0 EndZ=0
    g5: ArcOfCircle CenterX=7.60102 CenterY=6 CenterZ=0 NormalX=0 NormalY=0 NormalZ=1 AngleXU=0 Radius=6 StartAngle=4.71239 EndAngle=6.08183
    g6: GeomPoint [constr] X=10.879 Y=0 Z=0
    g7: ArcOfCircle CenterX=12.5 CenterY=5 CenterZ=0 NormalX=0 NormalY=0 NormalZ=1 AngleXU=0 Radius=1 StartAngle=6.08183 EndAngle=7.85398
    g8: ArcOfCircle CenterX=6.8 CenterY=1 CenterZ=0 NormalX=0 NormalY=0 NormalZ=1 AngleXU=0 Radius=1 StartAngle=3.14159 EndAngle=4.71239
    g9: GeomPoint [constr] X=5.8 Y=0 Z=0
  constraints (25):
    c: PointOnObject(g9,g-1)
    c: Vertical(g0)
    c: Coincident(g1,g0)
    c: Horizontal(g1)
    c: Coincident(g2,g1)
    c: Vertical(g2)
    c: Coincident(g3,g2)
    c: Horizontal(g3)
    c: Horizontal(g4)
    c: PointOnObject(g6,g4)
    c: Tangent(g4,g5) = 1.5708
    c: Tangent(g3,g7) = 1.5708
    c: Tangent(g7,g5) = -1.5708
    c: Horizontal(g5,g2)
    c: DistanceX(g-1,g2) = 2
    c: DistanceX(g-1,g3) = 12.5
    c: Radius(g7) = 1
    c: DistanceY(g-1,g2) = 6
    c: DistanceX(g1,g1) = 3.8
    c: PointOnObject(g9,g0)
    c: PointOnObject(g9,g4)
    c: Tangent(g0,g8) = 1.5708
    c: Tangent(g4,g8) = 1.5708
    c: Radius(g8) = 1
    c: DistanceY(g2,g2) = 2.5
FEATURE [PartDesign::Revolution] Revolution002
  Angle = 360
  Angle2 = 60
  Axis = (0,2e-16,1)
  Base = (0,0,0)
  Placement = pos=(0,0,0) rot=(1,0,0;1.5708rad)
  Profile = -> Sketch040
  ReferenceAxis = -> Sketch040 [V_Axis]
  Refine = true
  Reversed = true
  Suppressed = false
  Type = 0
FEATURE [PartDesign::Body] Body022  label="Foot"
  AllowCompound = false
  Group = -> [Sketch040,Revolution002]
  Origin = -> Origin024
  Tip = -> Revolution002
FEATURE [Part::FeaturePython] Screw003  label="#5x3/4in-Screw"  # WARN: FeaturePython — macro-defined, semantics opaque (R4)
  Diameter = 6
  Invert = false
  LeftHanded = false
  Length = 3
  LengthCustom = 19.05
  MatchOuter = false
  OffsetAngle = 0
  Placement = pos=(0,4e-16,3) rot=(-0.707107,-0.707107,0;3.14159rad)
  Thread = true
  Type = 17
FEATURE [Mesh::Feature] Arduino_Nano
  Placement = pos=(46,332,101) rot=(1,0,0;3.14159rad)
FEATURE [Sketcher::SketchObject] Sketch041
  ArcFitTolerance = 1e-06
  AttachmentSupport = -> [XZ_Plane025]
  FullyConstrained = true
  MakeInternals = false
  MapMode = 5
  Placement = pos=(0,0,0) rot=(1,0,0;1.5708rad)
  sketch-geometry (4):
    g0: LineSegment StartX=-25 StartY=0 StartZ=0 EndX=25 EndY=0 EndZ=0
    g1: LineSegment StartX=25 StartY=-2 StartZ=0 EndX=-25 EndY=-2 EndZ=0
    g2: LineSegment StartX=-25 StartY=0 StartZ=0 EndX=-25 EndY=-2 EndZ=0
    g3: LineSegment StartX=25 StartY=0 StartZ=0 EndX=25 EndY=-2 EndZ=0
  constraints (11):
    c: PointOnObject(g0,g-1)
    c: Horizontal(g1)
    c: Coincident(g2,g0)
    c: Coincident(g2,g1)
    c: Coincident(g3,g0)
    c: Coincident(g3,g1)
    c: Vertical(g3)
    c: Vertical(g2)
    c: Symmetric(g0,g0,g-1)
    c: DistanceY(g3,g3) = 2
    c: DistanceX(g1,g1) = 50
FEATURE [PartDesign::Pad] Pad023
  Direction = (0,-1,2e-16)
  Length = 47
  Length2 = 10
  Midplane = true
  Placement = pos=(0,0,0) rot=(1,0,0;1.5708rad)
  Profile = -> Sketch041
  ReferenceAxis = -> Sketch041 [N_Axis]
  Refine = true
  Suppressed = false
  Type = 0
FEATURE [Sketcher::SketchObject] Sketch042
  ArcFitTolerance = 1e-06
  AttachmentSupport = -> [Pad023]
  ExternalGeometry = -> [Pad023]
  FullyConstrained = true
  MakeInternals = false
  MapMode = 5
  Placement = pos=(0,0,-1e-16) rot=(0,0,1;3.14159rad)
  sketch-geometry (8):
    g0: LineSegment StartX=25 StartY=23.5 StartZ=0 EndX=17 EndY=23.5 EndZ=0
    g1: LineSegment StartX=17 StartY=23.5 StartZ=0 EndX=17 EndY=-20.09 EndZ=0
    g2: LineSegment StartX=17 StartY=-20.09 StartZ=0 EndX=25 EndY=-20.09 EndZ=0
    g3: LineSegment StartX=25 StartY=-20.09 StartZ=0 EndX=25 EndY=23.5 EndZ=0
    g4: LineSegment StartX=-25 StartY=-23.5 StartZ=0 EndX=-17 EndY=-23.5 EndZ=0
    g5: LineSegment StartX=-17 StartY=-23.5 StartZ=0 EndX=-17 EndY=-5.64 EndZ=0
    g6: LineSegment StartX=-17 StartY=-5.64 StartZ=0 EndX=-25 EndY=-5.64 EndZ=0
    g7: LineSegment StartX=-25 StartY=-5.64 StartZ=0 EndX=-25 EndY=-23.5 EndZ=0
  constraints (22):
    c: Coincident(g0,g-3)
    c: Horizontal(g0)
    c: Coincident(g1,g0)
    c: Vertical(g1)
    c: Coincident(g2,g1)
    c: Horizontal(g2)
    c: Coincident(g3,g2)
    c: Coincident(g3,g0)
    c: Vertical(g3)
    c: DistanceX(g2,g2) = 8
    c: DistanceY(g1,g1) = 43.59
    c: Coincident(g4,g5)
    c: Coincident(g5,g6)
    c: Coincident(g6,g7)
    c: Coincident(g7,g4)
    c: Horizontal(g4)
    c: Horizontal(g6)
    c: Vertical(g5)
    c: Vertical(g7)
    c: Coincident(g4,g-4)
    c: DistanceX(g6,g6) = 8
    c: DistanceY(g5,g5) = 17.86
FEATURE [PartDesign::Pad] Pad024
  BaseFeature = -> Pad023
  Direction = (0,0,1)
  Length = 8
  Length2 = 10
  Placement = pos=(0,0,0) rot=(1,0,0;1.5708rad)
  Profile = -> Sketch042
  ReferenceAxis = -> Sketch042 [N_Axis]
  Refine = true
  Suppressed = false
  Type = 0
FEATURE [PartDesign::Body] Body023  label="ProtoBoard"
  AllowCompound = false
  Group = -> [Sketch041,Pad023,Sketch042,Pad024]
  Origin = -> Origin025
  Tip = -> Pad024
FEATURE [Spreadsheet::Sheet] Spreadsheet002  label="HMRProperties"
  cells = A1='PropertyName; B1='Value; A2='Clearance; B2(Clearance)=0.2; A3='Handle_OD; B3(Handle_OD)=21.5; A4='shell_ID; B4(shell_ID)=51.4; A5='shell_length; B5(shell_length)=110; A6='head_diameter; B6(head_diameter)==shell_ID - Clearance; C6='calculated; A7='head_length; B7(head_length)=70; A8='wire_width; B8(wire_width)=10; A9='Sensor_Diameter; B9(Sensor_Diameter)=30; A10='Handle_ID; B10(Handle_ID)=20.5; A11='head_cutoff; B11(head_cutoff)=11; A12='top_sensor_pocket_depth; B12(top_sensor_pocket_depth)=13; A13='pusher_pocket_depth; B13(pusher_pocket_depth)=8; A14='pusher_notch_pocket_depth; B14(pusher_notch_pocket_depth)=3; A15='pusher_pocket_size; B15(pusher_pocket_size)=23.5; A16='top_sensor_pocket_size; B16(top_sensor_pocket_size)=34; A17='handle_hole_diameter; B17(handle_hole_diameter)==Handle_OD + Clearance * 2; C17='calculated; A18='plug_hole_diameter; B18(plug_hole_diameter)=5; A19='plug_height; B19(plug_height)=15; A20='plug_draft; B20(plug_draft)=4; A21='plug_start_diameter; B21(plug_start_diameter)==Handle_ID - Clearance; C21='calculated; A22='top_sensor_holder_size; B22(top_sensor_holder_size)==top_sensor_pocket_size - Clearance * 2; C22='calculated; A23='top_sensor_holder_height; B23(top_sensor_holder_height)==top_sensor_pocket_depth - Clearance * 2; C23='calculated
FEATURE [App::DocumentObjectGroup] Group001  label="Properties"
  Group = -> [Spreadsheet,Spreadsheet001,Spreadsheet002,Spreadsheet003]
FEATURE [PartDesign::AdditiveBox] Box001
  AttacherType = Attacher::AttachEngine3D
  AttachmentOffset = pos=(-2.5,52,1) rot=(0,0,1;0rad)
  AttachmentSupport = -> [XY_Plane021]
  BaseFeature = -> Pad020
  Height = 1.5
  Length = 5
  MapMode = 5
  Placement = pos=(-2.5,52,1) rot=(0,0,1;0rad)
  Refine = true
  Suppressed = false
  Width = 5
  expr: .AttachmentOffset.Base.y = -<<LHProperties>>.led_dim / 2 + <<LHProperties>>.led_housing_base_length / 2 - <<LHProperties>>.led_array_housing_spacing - 2.5
FEATURE [PartDesign::LinearPattern] LinearPattern002
  BaseFeature = -> Box001
  Direction = -> Y_Axis021
  Length = 109
  Mode = 1
  Occurrences = 11
  Offset = 10.9
  Originals = -> [Cylinder003,Box001]
  Placement = pos=(-2.5,52,1) rot=(0,0,1;0rad)
  Refine = true
  Reversed = true
  Suppressed = false
  TransformMode = 0
  expr: Length = <<LHProperties>>.led_array_spacing
  expr: Occurrences = <<LHProperties>>.led_amount
  expr: Offset = <<LHProperties>>.led_array_spacing + <<LHProperties>>.led_dim
FEATURE [PartDesign::Body] Body019  label="LED_Array"
  AllowCompound = false
  Group = -> [Cylinder003,Sketch037,Pad020,Box001,LinearPattern002]
  Origin = -> Origin021
  Placement = pos=(-62,-3e-16,0) rot=(0,0,1;0rad)
  Tip = -> Box001
FEATURE [App::DocumentObjectGroup] Group  label="BoxParts"
  Group = -> [Body,Body001,Body002,Body003,Body004,Body005,Body006,Body013,Body014,Body019,Body020,Screw,Screw002,Nut,Body021,Body022,Screw003,Body023]
FEATURE [TechDraw::DrawSVGTemplate] Template006
  EditableTexts = AuthorName=Alex Anastasakis,CheckDate=2024-11-29,CreationDate=2024-11-28,FC-Scale=1 : 3,FC-Title=Box,SheetNumber=2 / 2,+2 more (map truncated)
  Height = 297
  Orientation = 1
  Template = C:/Program Files/FreeCAD 1.0/data/Mod/TechDraw/Templates/A3_Landscape_TD.svg
  Width = 420
FEATURE [TechDraw::DrawSVGTemplate] Template007
  EditableTexts = AuthorName=Alex Anastasakis,CheckDate=2024-11-29,CreationDate=2024-11-28,FC-Scale=1 : 5,FC-Title=Box,SheetNumber=1 / 2,+2 more (map truncated)
  Height = 297
  Orientation = 1
  Template = C:/Program Files/FreeCAD 1.0/data/Mod/TechDraw/Templates/A3_Landscape_TD.svg
  Width = 420
FEATURE [Part::Feature] Body024  label="Bracket001"
  shape: bbox 30 x 30 x 30 mm, 43 faces (baked)
FEATURE [Part::Feature] Body025  label="LED_Housing001"
  Placement = pos=(-62,0,-10) rot=(0,0,1;0rad)
  shape: bbox 55 x 164 x 30 mm, 83 faces (baked)
FEATURE [Part::Feature] Body026  label="Latch001"
  Placement = pos=(8.6,-28.5,0) rot=(0,0,1;0rad)
  shape: bbox 2.632 x 8 x 21.8 mm, 12 faces (baked)
FEATURE [Part::Feature] Body027  label="Box_Cover001"
  shape: bbox 500 x 300 x 17 mm, 24 faces (baked)
FEATURE [Part::Feature] Body028  label="Wall_Long001"
  shape: bbox 500 x 17 x 60 mm, 6 faces (baked)
FEATURE [Part::Feature] Body029  label="Wall_Short001"
  shape: bbox 266 x 17 x 60 mm, 6 faces (baked)
FEATURE [Part::Feature] Body030  label="Foam_Pad001"
  Placement = pos=(115.2,0,79) rot=(0,0,1;0rad)
  shape: bbox 290 x 280 x 5 mm, 6 faces (baked)
FEATURE [Part::Feature] Body031  label="Cable_Management001"
  shape: bbox 30 x 30 x 5.9 mm, 29 faces (baked)
FEATURE [Part::Feature] Body032  label="Cable_Management_Cover001"
  shape: bbox 26.4 x 26.4 x 1.2 mm, 27 faces (baked)
FEATURE [Part::Feature] Body033  label="LED_Array001"
  Placement = pos=(-62,-3e-16,0) rot=(0,0,1;0rad)
  shape: bbox 9.7 x 113.9 x 3.5 mm, 26 faces (baked)
FEATURE [Part::Feature] Body034  label="LED_Housing_Cube001"
  shape: bbox 9.7 x 9.7 x 8 mm, 6 faces (baked)
FEATURE [Part::Feature] Screw004  label="#5x5/8in-Screw001"
  shape: bbox 5.994 x 5.994 x 15.88 mm, 54 faces (baked)
FEATURE [Part::Feature] Screw005  label="1/4inx1in-Screw001"
  Placement = pos=(0,0,119) rot=(0,0,1;0rad)
  shape: bbox 14.55 x 14.55 x 30.78 mm, 91 faces (baked)
FEATURE [Part::Feature] Nut001  label="1/4in-Nut001"
  shape: bbox 12.7 x 12.7 x 6.286 mm, 40 faces (baked)
FEATURE [Part::Feature] Body035  label="Joystick_hole_cover001"
  shape: bbox 56 x 56 x 1.6 mm, 4 faces (baked)
FEATURE [Part::Feature] Body036  label="Foot001"
  shape: bbox 29.44 x 29.44 x 6 mm, 8 faces (baked)
FEATURE [Part::Feature] Screw006  label="#5x3/4in-Screw001"
  Placement = pos=(0,4e-16,3) rot=(0.707107,0.707107,0;3.14159rad)
  shape: bbox 5.994 x 5.994 x 19.88 mm, 59 faces (baked)
FEATURE [Part::Feature] Body037  label="ProtoBoard001"
  shape: bbox 50 x 47 x 10 mm, 12 faces (baked)
FEATURE [App::DocumentObjectGroup] Group003  label="SimpleParts"
  Group = -> [Body024,Body025,Body026,Body027,Body028,Body029,Body030,Body031,Body032,Body033,Body034,Screw004,Screw005,Nut001,Body035,Body036,Screw006,Body037]
FEATURE [App::Link] Box_Cover001  label="Box_Cover002"
  LinkPlacement = pos=(191.91,249.021,479.61) rot=(0,0,1;0rad)
  LinkedObject = -> Body027
  Placement = pos=(191.91,249.021,479.61) rot=(0,0,1;0rad)
FEATURE [App::Link] Wall_Long001  label="Wall_Long002"
  LinkPlacement = pos=(191.91,107.521,69.6096) rot=(0,0,1;0rad)
  LinkedObject = -> Body028
  Placement = pos=(191.91,107.521,69.6096) rot=(0,0,1;0rad)
FEATURE [App::Link] Wall_Long002  label="Wall_Long003"
  LinkPlacement = pos=(191.91,350.521,69.6096) rot=(-1.00008,0,0;1e-06rad)
  LinkedObject = -> Body028
  Placement = pos=(191.91,350.521,69.6096) rot=(-1.00008,0,0;1e-06rad)
FEATURE [App::Link] Wall_Short001  label="Wall_Short002"
  LinkPlacement = pos=(433.41,249.021,69.6096) rot=(0,0,1;1.5708rad)
  LinkedObject = -> Body029
  Placement = pos=(433.41,249.021,69.6096) rot=(0,0,1;1.5708rad)
FEATURE [App::Link] Wall_Short002  label="Wall_Short003"
  LinkPlacement = pos=(-49.5904,249.021,69.6096) rot=(0,0,1;4.71239rad)
  LinkedObject = -> Body029
  Placement = pos=(-49.5904,249.021,69.6096) rot=(0,0,1;4.71239rad)
FEATURE [App::Link] Joystick
  LinkPlacement = pos=(11.9096,249.021,102.61) rot=(0,0,1;4.71239rad)
  LinkedObject = -> <external ../../V1/Projects/Box.FCStd>#Body002
  Placement = pos=(11.9096,249.021,102.61) rot=(0,0,1;4.71239rad)
FEATURE [App::Link] Joystick_hole_cover001  label="Joystick_hole_cover002"
  LinkPlacement = pos=(11.9096,249.021,116.61) rot=(0,0,1;0rad)
  LinkedObject = -> Body035
  Placement = pos=(11.9096,249.021,116.61) rot=(0,0,1;0rad)
FEATURE [App::Link] Bracket  label="Bracket002"
  LinkPlacement = pos=(425.91,383.021,99.6096) rot=(0,1,0;3.14159rad)
  LinkedObject = -> Body
  Placement = pos=(425.91,383.021,99.6096) rot=(0,1,0;3.14159rad)
FEATURE [App::Link] Bracket001  label="Bracket003"
  LinkPlacement = pos=(-42.0904,115.021,99.6096) rot=(1,0,0;3.14159rad)
  LinkedObject = -> Body
  Placement = pos=(-42.0904,115.021,99.6096) rot=(1,0,0;3.14159rad)
FEATURE [App::Link] Bracket002  label="Bracket004"
  LinkPlacement = pos=(425.91,115.021,99.6096) rot=(0.707107,0.707107,0;3.14159rad)
  LinkedObject = -> Body
  Placement = pos=(425.91,115.021,99.6096) rot=(0.707107,0.707107,0;3.14159rad)
FEATURE [App::Link] Bracket003  label="Bracket005"
  LinkPlacement = pos=(-42.0904,383.021,99.6096) rot=(-0.707107,0.707107,0;3.14159rad)
  LinkedObject = -> Body
  Placement = pos=(-42.0904,383.021,99.6096) rot=(-0.707107,0.707107,0;3.14159rad)
FEATURE [App::Link] LED_Housing001  label="LED_Housing002"
  LinkPlacement = pos=(96.4846,249.021,89.6096) rot=(0,0,1;0rad)
  LinkedObject = -> Body025
  Placement = pos=(96.4846,249.021,89.6096) rot=(0,0,1;0rad)
FEATURE [App::Link] Latch001  label="Latch002"
  LinkPlacement = pos=(87.8346,277.621,89.8096) rot=(0,0,1;3.14159rad)
  LinkedObject = -> Body026
  Placement = pos=(87.8346,277.621,89.8096) rot=(0,0,1;3.14159rad)
FEATURE [App::Link] Latch002  label="Latch003"
  LinkPlacement = pos=(87.8346,220.421,89.8096) rot=(0,0,1;3.14159rad)
  LinkedObject = -> Body026
  Placement = pos=(87.8346,220.421,89.8096) rot=(0,0,1;3.14159rad)
FEATURE [App::Link] Latch003  label="Latch004"
  LinkPlacement = pos=(105.135,277.621,89.8096) rot=(0,0,1;0rad)
  LinkedObject = -> Body026
  Placement = pos=(105.135,277.621,89.8096) rot=(0,0,1;0rad)
FEATURE [App::Link] Latch004  label="Latch005"
  LinkPlacement = pos=(105.135,220.421,89.8096) rot=(0,0,1;0rad)
  LinkedObject = -> Body026
  Placement = pos=(105.135,220.421,89.8096) rot=(0,0,1;0rad)
FEATURE [App::Link] LED_Housing_Cube001  label="LED_Housing_Cube002"
  LinkPlacement = pos=(96.4846,194.521,115.61) rot=(0,0,1;0rad)
  LinkedObject = -> Body034
  Placement = pos=(96.4846,194.521,115.61) rot=(0,0,1;0rad)
FEATURE [App::Link] LED_Housing_Cube002  label="LED_Housing_Cube003"
  LinkPlacement = pos=(96.4846,205.421,115.61) rot=(0,0,1;0rad)
  LinkedObject = -> Body034
  Placement = pos=(96.4846,205.421,115.61) rot=(0,0,1;0rad)
FEATURE [App::Link] LED_Housing_Cube003  label="LED_Housing_Cube004"
  LinkPlacement = pos=(96.4846,216.321,115.61) rot=(0,0,1;0rad)
  LinkedObject = -> Body034
  Placement = pos=(96.4846,216.321,115.61) rot=(0,0,1;0rad)
FEATURE [App::Link] LED_Housing_Cube004  label="LED_Housing_Cube005"
  LinkPlacement = pos=(96.4846,227.221,115.61) rot=(0,0,1;0rad)
  LinkedObject = -> Body034
  Placement = pos=(96.4846,227.221,115.61) rot=(0,0,1;0rad)
FEATURE [App::Link] LED_Housing_Cube005  label="LED_Housing_Cube006"
  LinkPlacement = pos=(96.4846,238.121,115.61) rot=(0,0,1;0rad)
  LinkedObject = -> Body034
  Placement = pos=(96.4846,238.121,115.61) rot=(0,0,1;0rad)
FEATURE [App::Link] LED_Housing_Cube006  label="LED_Housing_Cube007"
  LinkPlacement = pos=(96.4846,249.021,115.61) rot=(0,0,1;0rad)
  LinkedObject = -> Body034
  Placement = pos=(96.4846,249.021,115.61) rot=(0,0,1;0rad)
FEATURE [App::Link] LED_Housing_Cube007  label="LED_Housing_Cube008"
  LinkPlacement = pos=(96.4846,259.921,115.61) rot=(0,0,1;0rad)
  LinkedObject = -> Body034
  Placement = pos=(96.4846,259.921,115.61) rot=(0,0,1;0rad)
FEATURE [App::Link] LED_Housing_Cube008  label="LED_Housing_Cube009"
  LinkPlacement = pos=(96.4846,270.821,115.61) rot=(0,0,1;0rad)
  LinkedObject = -> Body034
  Placement = pos=(96.4846,270.821,115.61) rot=(0,0,1;0rad)
FEATURE [App::Link] LED_Housing_Cube009  label="LED_Housing_Cube010"
  LinkPlacement = pos=(96.4846,281.721,115.61) rot=(0,0,1;0rad)
  LinkedObject = -> Body034
  Placement = pos=(96.4846,281.721,115.61) rot=(0,0,1;0rad)
FEATURE [App::Link] LED_Housing_Cube010  label="LED_Housing_Cube011"
  LinkPlacement = pos=(96.4846,292.621,115.61) rot=(0,0,1;0rad)
  LinkedObject = -> Body034
  Placement = pos=(96.4846,292.621,115.61) rot=(0,0,1;0rad)
FEATURE [App::Link] LED_Housing_Cube011  label="LED_Housing_Cube012"
  LinkPlacement = pos=(96.4846,303.521,115.61) rot=(0,0,1;0rad)
  LinkedObject = -> Body034
  Placement = pos=(96.4846,303.521,115.61) rot=(0,0,1;0rad)
FEATURE [App::Link] LED_Array  label="LED_Array002"
  LinkPlacement = pos=(96.4846,249.021,89.6096) rot=(0,0,1;0rad)
  LinkedObject = -> Body019
  Placement = pos=(96.4846,249.021,89.6096) rot=(0,0,1;0rad)
FEATURE [App::Link] Foam_Pad001  label="Foam_Pad002"
  LinkPlacement = pos=(286.91,249.021,116.61) rot=(0,0,1;0rad)
  LinkedObject = -> Body030
  Placement = pos=(286.91,249.021,116.61) rot=(0,0,1;0rad)
FEATURE [App::Link] Foot001  label="Foot002"
  LinkPlacement = pos=(-45.0904,386.021,33.6096) rot=(0,0,1;4.71239rad)
  LinkedObject = -> Body036
  Placement = pos=(-45.0904,386.021,33.6096) rot=(0,0,1;4.71239rad)
FEATURE [App::Link] Foot002  label="Foot003"
  LinkPlacement = pos=(-45.0904,112.021,33.6096) rot=(0,0,1;4.71239rad)
  LinkedObject = -> Body036
  Placement = pos=(-45.0904,112.021,33.6096) rot=(0,0,1;4.71239rad)
FEATURE [App::Link] Foot003  label="Foot004"
  LinkPlacement = pos=(428.91,112.021,33.6096) rot=(0,0,1;1.5708rad)
  LinkedObject = -> Body036
  Placement = pos=(428.91,112.021,33.6096) rot=(0,0,1;1.5708rad)
FEATURE [App::Link] Foot004  label="Foot005"
  LinkPlacement = pos=(428.91,386.021,33.6096) rot=(0,0,1;1.5708rad)
  LinkedObject = -> Body036
  Placement = pos=(428.91,386.021,33.6096) rot=(0,0,1;1.5708rad)
FEATURE [App::Link] _5x5_8in_Screw001  label="#5x5/8in-Screw002"
  LinkPlacement = pos=(428.91,386.021,36.1096) rot=(0.707107,0.707107,0;3.14159rad)
  LinkedObject = -> Screw004
  Placement = pos=(428.91,386.021,36.1096) rot=(0.707107,0.707107,0;3.14159rad)
FEATURE [App::Link] _5x5_8in_Screw002  label="#5x5/8in-Screw003"
  LinkPlacement = pos=(428.91,112.021,36.1096) rot=(0.707107,0.707107,0;3.14159rad)
  LinkedObject = -> Screw004
  Placement = pos=(428.91,112.021,36.1096) rot=(0.707107,0.707107,0;3.14159rad)
FEATURE [App::Link] _5x5_8in_Screw003  label="#5x5/8in-Screw004"
  LinkPlacement = pos=(-45.0904,386.021,36.1096) rot=(-0.707107,0.707107,0;3.14159rad)
  LinkedObject = -> Screw004
  Placement = pos=(-45.0904,386.021,36.1096) rot=(-0.707107,0.707107,0;3.14159rad)
FEATURE [App::Link] _5x5_8in_Screw004  label="#5x5/8in-Screw005"
  LinkPlacement = pos=(-45.0904,112.021,36.1096) rot=(-0.707107,0.707107,0;3.14159rad)
  LinkedObject = -> Screw004
  Placement = pos=(-45.0904,112.021,36.1096) rot=(-0.707107,0.707107,0;3.14159rad)
FEATURE [App::Link] _5x5_8in_Screw005  label="#5x5/8in-Screw006"
  LinkPlacement = pos=(405.91,363.021,94.6096) rot=(0,1,0;3.14159rad)
  LinkedObject = -> Screw004
  Placement = pos=(405.91,363.021,94.6096) rot=(0,1,0;3.14159rad)
FEATURE [App::Link] _5x5_8in_Screw006  label="#5x5/8in-Screw007"
  LinkPlacement = pos=(-22.0904,363.021,94.6096) rot=(-0.707107,0.707107,0;3.14159rad)
  LinkedObject = -> Screw004
  Placement = pos=(-22.0904,363.021,94.6096) rot=(-0.707107,0.707107,0;3.14159rad)
FEATURE [App::Link] _5x5_8in_Screw007  label="#5x5/8in-Screw008"
  LinkPlacement = pos=(405.91,135.021,94.6096) rot=(0.707107,0.707107,0;3.14159rad)
  LinkedObject = -> Screw004
  Placement = pos=(405.91,135.021,94.6096) rot=(0.707107,0.707107,0;3.14159rad)
FEATURE [App::Link] _5x5_8in_Screw008  label="#5x5/8in-Screw009"
  LinkPlacement = pos=(-22.0904,135.021,94.6096) rot=(1,0,0;3.14159rad)
  LinkedObject = -> Screw004
  Placement = pos=(-22.0904,135.021,94.6096) rot=(1,0,0;3.14159rad)
FEATURE [App::Link] _5x5_8in_Screw009  label="#5x5/8in-Screw010"
  LinkPlacement = pos=(405.91,378.021,88.6096) rot=(1,0,0;1.5708rad)
  LinkedObject = -> Screw004
  Placement = pos=(405.91,378.021,88.6096) rot=(1,0,0;1.5708rad)
FEATURE [App::Link] _5x5_8in_Screw010  label="#5x5/8in-Screw011"
  LinkPlacement = pos=(405.91,378.021,76.6096) rot=(1,0,0;1.5708rad)
  LinkedObject = -> Screw004
  Placement = pos=(405.91,378.021,76.6096) rot=(1,0,0;1.5708rad)
FEATURE [App::Link] _5x5_8in_Screw011  label="#5x5/8in-Screw012"
  LinkPlacement = pos=(-22.0904,378.021,88.6096) rot=(0,-0.707107,0.707107;3.14159rad)
  LinkedObject = -> Screw004
  Placement = pos=(-22.0904,378.021,88.6096) rot=(0,-0.707107,0.707107;3.14159rad)
FEATURE [App::Link] _5x5_8in_Screw012  label="#5x5/8in-Screw013"
  LinkPlacement = pos=(-22.0904,378.021,76.6096) rot=(0,-0.707107,0.707107;3.14159rad)
  LinkedObject = -> Screw004
  Placement = pos=(-22.0904,378.021,76.6096) rot=(0,-0.707107,0.707107;3.14159rad)
FEATURE [App::Link] _5x5_8in_Screw013  label="#5x5/8in-Screw014"
  LinkPlacement = pos=(-22.0904,120.021,76.6096) rot=(0,0.707107,0.707107;3.14159rad)
  LinkedObject = -> Screw004
  Placement = pos=(-22.0904,120.021,76.6096) rot=(0,0.707107,0.707107;3.14159rad)
FEATURE [App::Link] _5x5_8in_Screw014  label="#5x5/8in-Screw015"
  LinkPlacement = pos=(-22.0904,120.021,88.6096) rot=(0,0.707107,0.707107;3.14159rad)
  LinkedObject = -> Screw004
  Placement = pos=(-22.0904,120.021,88.6096) rot=(0,0.707107,0.707107;3.14159rad)
FEATURE [App::Link] _5x5_8in_Screw015  label="#5x5/8in-Screw016"
  LinkPlacement = pos=(405.91,120.021,76.6096) rot=(-1,0,0;1.5708rad)
  LinkedObject = -> Screw004
  Placement = pos=(405.91,120.021,76.6096) rot=(-1,0,0;1.5708rad)
FEATURE [App::Link] _5x5_8in_Screw016  label="#5x5/8in-Screw017"
  LinkPlacement = pos=(405.91,120.021,88.6096) rot=(-1,0,0;1.5708rad)
  LinkedObject = -> Screw004
  Placement = pos=(405.91,120.021,88.6096) rot=(-1,0,0;1.5708rad)
FEATURE [App::Link] _5x5_8in_Screw017  label="#5x5/8in-Screw018"
  LinkPlacement = pos=(420.91,363.021,76.6096) rot=(0.57735,0.57735,-0.57735;4.18879rad)
  LinkedObject = -> Screw004
  Placement = pos=(420.91,363.021,76.6096) rot=(0.57735,0.57735,-0.57735;4.18879rad)
FEATURE [App::Link] _5x5_8in_Screw018  label="#5x5/8in-Screw019"
  LinkPlacement = pos=(420.91,363.021,88.6096) rot=(0.57735,0.57735,-0.57735;4.18879rad)
  LinkedObject = -> Screw004
  Placement = pos=(420.91,363.021,88.6096) rot=(0.57735,0.57735,-0.57735;4.18879rad)
FEATURE [App::Link] _5x5_8in_Screw019  label="#5x5/8in-Screw020"
  LinkPlacement = pos=(420.91,135.021,76.6096) rot=(0.57735,-0.57735,-0.57735;2.0944rad)
  LinkedObject = -> Screw004
  Placement = pos=(420.91,135.021,76.6096) rot=(0.57735,-0.57735,-0.57735;2.0944rad)
FEATURE [App::Link] _5x5_8in_Screw020  label="#5x5/8in-Screw021"
  LinkPlacement = pos=(420.91,135.021,88.6096) rot=(0.57735,-0.57735,-0.57735;2.0944rad)
  LinkedObject = -> Screw004
  Placement = pos=(420.91,135.021,88.6096) rot=(0.57735,-0.57735,-0.57735;2.0944rad)
FEATURE [App::Link] _5x5_8in_Screw021  label="#5x5/8in-Screw022"
  LinkPlacement = pos=(-37.0904,135.021,76.6096) rot=(0.57735,-0.57735,0.57735;4.18879rad)
  LinkedObject = -> Screw004
  Placement = pos=(-37.0904,135.021,76.6096) rot=(0.57735,-0.57735,0.57735;4.18879rad)
FEATURE [App::Link] _5x5_8in_Screw022  label="#5x5/8in-Screw023"
  LinkPlacement = pos=(-37.0904,135.021,88.6096) rot=(0.57735,-0.57735,0.57735;4.18879rad)
  LinkedObject = -> Screw004
  Placement = pos=(-37.0904,135.021,88.6096) rot=(0.57735,-0.57735,0.57735;4.18879rad)
FEATURE [App::Link] _5x5_8in_Screw023  label="#5x5/8in-Screw024"
  LinkPlacement = pos=(-37.0904,363.021,76.6096) rot=(0.57735,0.57735,0.57735;2.0944rad)
  LinkedObject = -> Screw004
  Placement = pos=(-37.0904,363.021,76.6096) rot=(0.57735,0.57735,0.57735;2.0944rad)
FEATURE [App::Link] _5x5_8in_Screw024  label="#5x5/8in-Screw025"
  LinkPlacement = pos=(-37.0904,363.021,88.6096) rot=(0.57735,0.57735,0.57735;2.0944rad)
  LinkedObject = -> Screw004
  Placement = pos=(-37.0904,363.021,88.6096) rot=(0.57735,0.57735,0.57735;2.0944rad)
FEATURE [App::Link] __4inx1in_Screw001  label="1/4inx1in-Screw002"
  LinkPlacement = pos=(44.1596,211.521,116.61) rot=(0,0,1;0rad)
  LinkedObject = -> Screw005
  Placement = pos=(44.1596,211.521,116.61) rot=(0,0,1;0rad)
FEATURE [App::Link] __4inx1in_Screw002  label="1/4inx1in-Screw003"
  LinkPlacement = pos=(-20.3404,211.521,116.61) rot=(0,0,1;0rad)
  LinkedObject = -> Screw005
  Placement = pos=(-20.3404,211.521,116.61) rot=(0,0,1;0rad)
FEATURE [App::Link] __4inx1in_Screw003  label="1/4inx1in-Screw004"
  LinkPlacement = pos=(44.1596,286.521,116.61) rot=(0,0,1;0rad)
  LinkedObject = -> Screw005
  Placement = pos=(44.1596,286.521,116.61) rot=(0,0,1;0rad)
FEATURE [App::Link] __4inx1in_Screw004  label="1/4inx1in-Screw005"
  LinkPlacement = pos=(-20.3404,286.521,116.61) rot=(0,0,1;0rad)
  LinkedObject = -> Screw005
  Placement = pos=(-20.3404,286.521,116.61) rot=(0,0,1;0rad)
FEATURE [App::Link] __4in_Nut001  label="1/4in-Nut002"
  LinkPlacement = pos=(44.1596,211.521,98.2096) rot=(0,0,1;0rad)
  LinkedObject = -> Nut001
  Placement = pos=(44.1596,211.521,98.2096) rot=(0,0,1;0rad)
FEATURE [App::Link] __4in_Nut002  label="1/4in-Nut003"
  LinkPlacement = pos=(-20.4547,211.899,98.2096) rot=(0,0,1;0rad)
  LinkedObject = -> Nut001
  Placement = pos=(-20.4547,211.899,98.2096) rot=(0,0,1;0rad)
FEATURE [App::Link] __4in_Nut003  label="1/4in-Nut004"
  LinkPlacement = pos=(-20.3404,286.521,98.2096) rot=(0,0,1;0rad)
  LinkedObject = -> Nut001
  Placement = pos=(-20.3404,286.521,98.2096) rot=(0,0,1;0rad)
FEATURE [App::Link] __4in_Nut004  label="1/4in-Nut005"
  LinkPlacement = pos=(44.1596,286.521,98.2096) rot=(0,0,1;0rad)
  LinkedObject = -> Nut001
  Placement = pos=(44.1596,286.521,98.2096) rot=(0,0,1;0rad)
FEATURE [App::Link] ProtoBoard001  label="ProtoBoard002"
  LinkPlacement = pos=(46.4346,333.071,97.6096) rot=(0,1,0;3.14159rad)
  LinkedObject = -> Body037
  Placement = pos=(46.4346,333.071,97.6096) rot=(0,1,0;3.14159rad)
FEATURE [TechDraw::DrawViewImage] ActiveView
  Height = 102.4
  ImageFile = <userpath>/AppData/Local/cache/FreeCAD/Cache/FreeCAD_Doc_03bf06b6-d966-4a27-abdd-09443d106f88_0033b3_71970/Pag87D6.tmp.png
  LockPosition = false
  Rotation = 0
  Scale = 1.3
  ScaleType = 2
  Width = 128
  X = 100.892
  Y = 82.9706
FEATURE [TechDraw::DrawViewImage] ActiveView001
  Height = 102.4
  ImageFile = <userpath>/AppData/Local/cache/FreeCAD/Cache/FreeCAD_Doc_03bf06b6-d966-4a27-abdd-09443d106f88_0033b3_45171/PagE95B.tmp.png
  LockPosition = false
  Rotation = 0
  Scale = 1.2
  ScaleType = 2
  Width = 128
  X = 142.298
  Y = 145.024
FEATURE [Spreadsheet::Sheet] Spreadsheet004  label="BOM"
  cells = A1='PARTS LIST; A2='ITEM NO.; B2='QTY; C2='NAME; D2='PART DESCRIPTION; E2='MATERIAL; F2='COST; A3=1; B3=2; C3='Long Wall; D3='500x60x17mm; E3='Wood; A4=2; B4=2; C4='Short Wall; D4='266x60x17mm; E4='Wood; A5=3; B5=1; C5='Cover; D5='Top face of box; E5='Wood; A6=4; B6=4; C6='Bolt; D6='1/4in x 1in; E6='Steel; F6='approx. $1ea (home depot); A7=5; B7=4; C7='Latch; D7='Attaches to the LED Cover; E7='PLA; F7='$22.99 (1kg of filament); A8=6; B8=11; C8='Acrylic Cube; D8='9.7x9.7x10mm; F8='$18.99 (pair of sheets); A9=7; B9=1; C9='LED Cover; D9='LED strip container; E9='PLA; F9='Shares cost of item NO.5; A10=8; B10=11; C10='LED; D10='Neopixel RGB LED; E10='FR4/Plastic/Metal; F10='$23.99 (pack of 100); A11=9; B11=1; C11='Strike Pad; D11='290x280x10mm; E11='Polyethylene Foam; F11='$26.99 (pack of foam); A12=10; B12=1; C12='Joystick; D12='Arcade joystick; E12='Plastic/Metal; F12='$18.88; A13=11; B13=1; C13='Circuit Board; D13='Perforated prototyping board; F13='$17.99 (pack of 10); A14=12; B14=4; C14='Nut; D14='1/4in; E14='Steel; F14='approx. $0.34ea (home depot); A15=13; B15=2; C15='Cable Lock; D15='Anti tug for wires; E15='PLA; F15='Shares cost of item NO.5; A16=14; B16=2; C16='Cable Lock Cover; E16='PLA; F16='Shares cost of item NO.5; A17=15; B17=26; C17='Screw; D17='#5x5/8in; E17='Steel; F17='$0.17ea; A18=16; B18=4; C18='Bracket; E18='PLA; F18='Shares cost of item NO.5; A19=17; B19=4; C19='Foot; D19='Anti slip furniture feet; E19='Rubber; F19='$0.39ea; A20=18; B20=1; C20='Arduino Nano; E20='FR4/Metal; F20='$16.99
FEATURE [App::Link] Cable_Management  label="Cable_Management002"
  LinkPlacement = pos=(140.91,162.021,84.6096) rot=(1,0,0;1.5708rad)
  LinkedObject = -> Body013
  Placement = pos=(140.91,162.021,84.6096) rot=(1,0,0;1.5708rad)
FEATURE [App::Link] Cable_Management001  label="Cable_Management003"
  LinkPlacement = pos=(191.91,162.021,84.6096) rot=(1,0,0;1.5708rad)
  LinkedObject = -> Body013
  Placement = pos=(191.91,162.021,84.6096) rot=(1,0,0;1.5708rad)
FEATURE [App::Link] Cable_Management_Cover  label="Cable_Management_Cover002"
  LinkPlacement = pos=(140.91,336.121,84.6096) rot=(0.57735,0.57735,0.57735;4.18879rad)
  LinkedObject = -> Body014
  Placement = pos=(140.91,336.121,84.6096) rot=(0.57735,0.57735,0.57735;4.18879rad)
FEATURE [App::Link] Cable_Management_Cover001  label="Cable_Management_Cover003"
  LinkPlacement = pos=(191.91,336.121,84.6096) rot=(-0.57735,-0.57735,-0.57735;2.0944rad)
  LinkedObject = -> Body014
  Placement = pos=(191.91,336.121,84.6096) rot=(-0.57735,-0.57735,-0.57735;2.0944rad)
FEATURE [App::FeaturePython] GroundedJoint  # Assembly grounded joint (typed FeaturePython)
  ObjectToGround = -> Box_Cover001
  Placement = pos=(191.91,249.021,479.61) rot=(0,0,1;0rad)
FEATURE [App::FeaturePython] Joint  label="Fixed"  # Assembly joint (typed FeaturePython)
  Activated = true
  AngleMax = 0
  AngleMin = 0
  Detach1 = false
  Detach2 = false
  Distance = 0
  Distance2 = 0
  EnableAngleMax = false
  EnableAngleMin = false
  EnableLengthMax = false
  EnableLengthMin = false
  JointType = 0 (Fixed)
  LengthMax = 0
  LengthMin = 0
  Offset2 = pos=(0,0,-51) rot=(0,0,1;1.5708rad)
  Placement1 = pos=(0,-8.5,30) rot=(-0.707107,0,0.707107;3.14159rad)
  Placement2 = pos=(51,15.0002,-180) rot=(-0.57735,0.57735,0.57735;4.18879rad)
  Reference1 = -> Assembly [Wall_Long002.Edge10,Wall_Long002.Edge10]
  Reference2 = -> Assembly [Cable_Management.Edge4,Cable_Management.Edge4]
FEATURE [App::FeaturePython] Joint001  label="Fixed001"  # Assembly joint (typed FeaturePython)
  Activated = true
  AngleMax = 0
  AngleMin = 0
  Detach1 = false
  Detach2 = false
  Distance = 0
  Distance2 = 0
  EnableAngleMax = false
  EnableAngleMin = false
  EnableLengthMax = false
  EnableLengthMin = false
  JointType = 0 (Fixed)
  LengthMax = 0
  LengthMin = 0
  Offset2 = pos=(0,0,0) rot=(0,0,1;1.5708rad)
  Placement1 = pos=(0,-8.5,30) rot=(-0.707107,0,0.707107;3.14159rad)
  Placement2 = pos=(-1.99e-13,15.0001,-180.001) rot=(-0.57735,0.57735,0.57735;4.18879rad)
  Reference1 = -> Assembly [Wall_Long002.Edge10,Wall_Long002.Edge10]
  Reference2 = -> Assembly [Cable_Management001.Edge4,Cable_Management001.Edge4]
FEATURE [App::FeaturePython] Joint002  label="Fixed002"  # Assembly joint (typed FeaturePython)
  Activated = true
  AngleMax = 0
  AngleMin = 0
  Detach1 = false
  Detach2 = false
  Distance = 0
  Distance2 = 0
  EnableAngleMax = false
  EnableAngleMin = false
  EnableLengthMax = false
  EnableLengthMin = false
  JointType = 0 (Fixed)
  LengthMax = 0
  LengthMin = 0
  Offset2 = pos=(0,0,1.2) rot=(0,0,1;1.5708rad)
  Placement1 = pos=(-8,-7.99979,-175.3) rot=(-1,0,0;3.14159rad)
  Placement2 = pos=(-8,-8,1.2) rot=(0,0,1;1.5708rad)
  Reference1 = -> Assembly [Cable_Management.Edge25,Cable_Management.Edge25]
  Reference2 = -> Assembly [Cable_Management_Cover.Edge74,Cable_Management_Cover.Edge74]
FEATURE [App::FeaturePython] Joint003  label="Fixed003"  # Assembly joint (typed FeaturePython)
  Activated = true
  AngleMax = 0
  AngleMin = 0
  Detach1 = false
  Detach2 = false
  Distance = 0
  Distance2 = 0
  EnableAngleMax = false
  EnableAngleMin = false
  EnableLengthMax = false
  EnableLengthMin = false
  JointType = 0 (Fixed)
  LengthMax = 0
  LengthMin = 0
  Offset2 = pos=(0,0,1.2) rot=(0,0,1;1.5708rad)
  Placement1 = pos=(-8,-7.99987,-175.301) rot=(-1,0,0;3.14159rad)
  Placement2 = pos=(-8,-8,1.2) rot=(0,0,1;1.5708rad)
  Reference1 = -> Assembly [Cable_Management001.Edge25,Cable_Management001.Edge25]
  Reference2 = -> Assembly [Cable_Management_Cover001.Edge74,Cable_Management_Cover001.Edge74]
FEATURE [App::Link] _5x5_8in_Screw  label="#5x5/8in-Screw026"
  LinkPlacement = pos=(132.91,335.888,76.6096) rot=(0.57735,-0.57735,0.57735;2.0944rad)
  LinkedObject = -> Screw
  Placement = pos=(132.91,335.888,76.6096) rot=(0.57735,-0.57735,0.57735;2.0944rad)
FEATURE [App::Link] _5x5_8in_Screw025  label="#5x5/8in-Screw027"
  LinkPlacement = pos=(183.91,335.888,76.6096) rot=(0.57735,-0.57735,0.57735;2.0944rad)
  LinkedObject = -> Screw
  Placement = pos=(183.91,335.888,76.6096) rot=(0.57735,-0.57735,0.57735;2.0944rad)
FEATURE [App::FeaturePython] GroundedJoint001  # Assembly grounded joint (typed FeaturePython)
  ObjectToGround = -> Cable_Management_Cover
  Placement = pos=(140.91,336.121,84.6096) rot=(0.57735,0.57735,0.57735;4.18879rad)
FEATURE [App::FeaturePython] Joint004  label="Fixed004"  # Assembly joint (typed FeaturePython)
  Activated = true
  AngleMax = 0
  AngleMin = 0
  Detach1 = false
  Detach2 = false
  Distance = 0
  Distance2 = 0
  EnableAngleMax = false
  EnableAngleMin = false
  EnableLengthMax = false
  EnableLengthMin = false
  JointType = 0 (Fixed)
  LengthMax = 0
  LengthMin = 0
  Placement1 = pos=(-8,-8,0) rot=(0,0,1;0rad)
  Placement2 = pos=(0,0,-0.233755) rot=(0,0,1;0rad)
  Reference1 = -> Assembly [Cable_Management_Cover.Edge74,Cable_Management_Cover.Edge74]
  Reference2 = -> Assembly [_5x5_8in_Screw.Edge80,_5x5_8in_Screw.Edge80]
FEATURE [App::FeaturePython] GroundedJoint002  # Assembly grounded joint (typed FeaturePython)
  ObjectToGround = -> Cable_Management_Cover001
  Placement = pos=(191.91,336.121,84.6096) rot=(0.57735,0.57735,0.57735;4.18879rad)
FEATURE [App::FeaturePython] Joint005  label="Fixed005"  # Assembly joint (typed FeaturePython)
  Activated = true
  AngleMax = 0
  AngleMin = 0
  Detach1 = false
  Detach2 = false
  Distance = 0
  Distance2 = 0
  EnableAngleMax = false
  EnableAngleMin = false
  EnableLengthMax = false
  EnableLengthMin = false
  JointType = 0 (Fixed)
  LengthMax = 0
  LengthMin = 0
  Placement1 = pos=(-8,-8,0) rot=(0,0,1;0rad)
  Placement2 = pos=(0,0,-0.233755) rot=(0,0,1;0rad)
  Reference1 = -> Assembly [Cable_Management_Cover001.Edge74,Cable_Management_Cover001.Edge74]
  Reference2 = -> Assembly [_5x5_8in_Screw025.Edge80,_5x5_8in_Screw025.Edge80]
FEATURE [Assembly::JointGroup] Joints
  Group = -> [GroundedJoint,Joint,Joint001,Joint002,Joint003,GroundedJoint001,Joint004,GroundedJoint002,Joint005]
FEATURE [Assembly::AssemblyObject] Assembly  label="BoxAssembly"
  Group = -> [Joints,Box_Cover001,Wall_Long001,Wall_Long002,Wall_Short001,Wall_Short002,Joystick,Joystick_hole_cover001,Bracket,Bracket001,Bracket002,Bracket003,LED_Housing001,Latch001,Latch002,Latch003,Latch004,LED_Housing_Cube001,LED_Housing_Cube002,LED_Housing_Cube003,LED_Housing_Cube004,LED_Housing_Cube005,LED_Housing_Cube006,LED_Housing_Cube007,LED_Housing_Cube008,LED_Housing_Cube009,LED_Housing_Cube010,+55 more]
  Origin = -> Origin007
  Type = Assembly
FEATURE [TechDraw::DrawProjGroupItem] View007  label="Front006"
  CoarseView = false
  Direction = (0,-1,0)
  Focus = 100
  HardHidden = false
  IsoCount = 0
  IsoHidden = false
  IsoVisible = false
  LockPosition = true
  Perspective = false
  Rotation = 0
  RotationVector = (1,0,0)
  Scale = 0.33
  ScaleType = 2
  ScrubCount = 1
  SeamHidden = false
  SeamVisible = false
  SmoothHidden = false
  SmoothVisible = true
  Source = -> [Assembly]
  Type = 0
  X = 0
  XDirection = (1,0,0)
  Y = 0
FEATURE [TechDraw::DrawProjGroupItem] ProjItem017  label="FrontTopRight006"
  CoarseView = false
  Direction = (0.57735,-0.57735,0.57735)
  Focus = 100
  HardHidden = false
  IsoCount = 0
  IsoHidden = false
  IsoVisible = false
  LockPosition = false
  Perspective = false
  Rotation = 0
  RotationVector = (1,0,0)
  Scale = 0.33
  ScaleType = 0
  ScrubCount = 1
  SeamHidden = false
  SeamVisible = false
  SmoothHidden = false
  SmoothVisible = true
  Source = -> [Assembly]
  Type = 7
  X = 193.852
  XDirection = (0.707107,0.707107,0)
  Y = -22.9289
FEATURE [TechDraw::DrawProjGroupItem] ProjItem018  label="Bottom002"
  CoarseView = false
  Direction = (0,0,-1)
  Focus = 100
  HardHidden = false
  IsoCount = 0
  IsoHidden = false
  IsoVisible = false
  LockPosition = false
  Perspective = false
  Rotation = 0
  RotationVector = (1,0,0)
  ScaleType = 2
  ScrubCount = 1
  SeamHidden = false
  SeamVisible = false
  SmoothHidden = false
  SmoothVisible = true
  Source = -> [Assembly]
  Type = 5
  X = 0
  XDirection = (1,0,0)
  Y = -121.303
FEATURE [TechDraw::DrawProjGroup] ProjGroup006
  Anchor = -> View007
  AutoDistribute = false
  LockPosition = false
  ProjectionType = 1
  Rotation = 0
  Scale = 0.33
  ScaleType = 0
  Source = -> [Assembly]
  Views = -> [View007,ProjItem017,ProjItem018]
  X = 111.138
  Y = 211.654
  spacingX = 15
  spacingY = 15
FEATURE [TechDraw::DrawPage] Page006  label="Assembly_Drawing"
  KeepUpdated = true
  NextBalloonIndex = 1
  ProjectionType = 1
  Scale = 0.33
  Template = -> Template006
  Views = -> [ProjGroup006,ActiveView]
FEATURE [TechDraw::DrawProjGroupItem] View008
  CoarseView = false
  Direction = (0.57735,-0.57735,0.57735)
  Focus = 100
  HardHidden = false
  IsoCount = 0
  IsoHidden = false
  IsoVisible = false
  LockPosition = false
  Perspective = false
  Rotation = 0
  RotationVector = (1,0,0)
  Scale = 0.2
  ScaleType = 0
  ScrubCount = 1
  SeamHidden = false
  SeamVisible = false
  SmoothHidden = false
  SmoothVisible = true
  Source = -> [Assembly]
  Type = 0
  X = 113.597
  XDirection = (0.707107,0.707107,0)
  Y = 145.024
FEATURE [Part::Feature] trajectory_line
  shape: bbox 428 x 228 x 350 mm, 0 faces, 0 solids (baked)
FEATURE [App::DocumentObjectGroupPython] BoltGroup  # scripted group (container) (typed FeaturePython)
  AnimationStepTime = 0
  AnimationSteps = 20
  Distance = -330
  Group = -> [trajectory_line]
  Revolutions = 0
  dir_vectors = (4) [(0,0,1),(0,0,1),(0,0,1),(0,0,1)]
  rot_centers = (4) [(405.91,135.021,94.6096),(-22.0904,135.021,94.6096),(-22.0904,363.021,94.6096),(405.91,363.021,94.6096)]
  rot_vectors = (4) [(0,0,1),(0,0,1),(0,0,1),(0,0,1)]
FEATURE [Part::Feature] trajectory_line001
  shape: bbox 2e-07 x 2e-07 x 380 mm, 0 faces, 0 solids (baked)
FEATURE [App::DocumentObjectGroupPython] SimpleGroup001  # scripted group (container) (typed FeaturePython)
  AnimationStepTime = 0
  AnimationSteps = 20
  Distance = -380
  Group = -> [trajectory_line001]
  Revolutions = 0
  dir_vectors = (31) [(0,-4.4e-16,-1),(0,-4.4e-16,-1),(0,-4.4e-16,-1),(0,-4.4e-16,-1),(0,-4.4e-16,-1),(0,-4.4e-16,-1),(0,-4.4e-16,-1),(0,-4.4e-16,-1),(0,-4.4e-16,-1),+22 more]
  rot_centers = (31) [(191.91,107.521,39.6096),(191.91,107.521,39.6096),(191.91,107.521,39.6096),(191.91,107.521,39.6096),(191.91,107.521,39.6096),(191.91,107.521,39.6096),+25 more]
  rot_vectors = (31) [(0,-4.4e-16,-1),(0,-4.4e-16,-1),(0,-4.4e-16,-1),(0,-4.4e-16,-1),(0,-4.4e-16,-1),(0,-4.4e-16,-1),(0,-4.4e-16,-1),(0,-4.4e-16,-1),(0,-4.4e-16,-1),+22 more]
FEATURE [Part::Feature] trajectory_line002
  shape: bbox 60 x 2e-07 x 2e-07 mm, 0 faces, 0 solids (baked)
FEATURE [App::DocumentObjectGroupPython] SimpleGroup002  # scripted group (container) (typed FeaturePython)
  AnimationStepTime = 0
  AnimationSteps = 20
  Distance = 60
  Group = -> [trajectory_line002]
  Revolutions = 0
  dir_vectors = (4) [(1,-2.22045e-16,0),(1,-2.22045e-16,0),(1,-2.22045e-16,0),(1,-2.22045e-16,0)]
  rot_centers = (4) [(-41.0904,249.021,69.6096),(-41.0904,249.021,69.6096),(-41.0904,249.021,69.6096),(-41.0904,249.021,69.6096)]
  rot_vectors = (4) [(1,-2.22045e-16,0),(1,-2.22045e-16,0),(1,-2.22045e-16,0),(1,-2.22045e-16,0)]
FEATURE [Part::Feature] trajectory_line003
  shape: bbox 428 x 60 x 12 mm, 0 faces, 0 solids (baked)
FEATURE [App::DocumentObjectGroupPython] BoltGroup001  # scripted group (container) (typed FeaturePython)
  AnimationStepTime = 0
  AnimationSteps = 20
  Distance = 60
  Group = -> [trajectory_line003]
  Revolutions = 0
  dir_vectors = (4) [(0,1,0),(0,1,0),(0,1,0),(0,1,0)]
  rot_centers = (4) [(405.91,120.021,88.6096),(405.91,120.021,76.6096),(-22.0904,120.021,88.6096),(-22.0904,120.021,76.6096)]
  rot_vectors = (4) [(0,1,0),(0,1,0),(0,1,0),(0,1,0)]
FEATURE [Part::Feature] trajectory_line004
  shape: bbox 428 x 60 x 12 mm, 0 faces, 0 solids (baked)
FEATURE [App::DocumentObjectGroupPython] BoltGroup002  # scripted group (container) (typed FeaturePython)
  AnimationStepTime = 0
  AnimationSteps = 20
  Distance = 60
  Group = -> [trajectory_line004]
  Revolutions = 0
  dir_vectors = (4) [(0,-1,0),(0,-1,0),(0,-1,0),(0,-1,0)]
  rot_centers = (4) [(-22.0904,378.021,88.6096),(-22.0904,378.021,76.6096),(405.91,378.021,88.6096),(405.91,378.021,76.6096)]
  rot_vectors = (4) [(0,-1,0),(0,-1,0),(0,-1,0),(0,-1,0)]
FEATURE [Part::Feature] trajectory_line005
  shape: bbox 60 x 228 x 12 mm, 0 faces, 0 solids (baked)
FEATURE [App::DocumentObjectGroupPython] BoltGroup003  # scripted group (container) (typed FeaturePython)
  AnimationStepTime = 0
  AnimationSteps = 20
  Distance = 60
  Group = -> [trajectory_line005]
  Revolutions = 0
  dir_vectors = (4) [(-1,-2.22045e-16,0),(-1,-2.22045e-16,0),(-1,-2.22045e-16,0),(-1,-2.22045e-16,0)]
  rot_centers = (4) [(420.91,135.021,88.6096),(420.91,135.021,76.6096),(420.91,363.021,76.6096),(420.91,363.021,88.6096)]
  rot_vectors = (4) [(-1,-2.22045e-16,0),(-1,-2.22045e-16,0),(-1,-2.22045e-16,0),(-1,-2.22045e-16,0)]
FEATURE [Part::Feature] trajectory_line006
  shape: bbox 474 x 274 x 200 mm, 0 faces, 0 solids (baked)
FEATURE [App::DocumentObjectGroupPython] BoltGroup004  # scripted group (container) (typed FeaturePython)
  AnimationStepTime = 0
  AnimationSteps = 20
  Distance = -160
  Group = -> [trajectory_line006]
  Revolutions = 0
  dir_vectors = (4) [(0,0,1),(0,0,1),(0,0,1),(0,0,1)]
  rot_centers = (4) [(428.91,112.021,36.1096),(428.91,386.021,36.1096),(-45.0904,386.021,36.1096),(-45.0904,112.021,36.1096)]
  rot_vectors = (4) [(0,0,1),(0,0,1),(0,0,1),(0,0,1)]
FEATURE [Part::Feature] trajectory_line007
  shape: bbox 474 x 274 x 100 mm, 0 faces, 0 solids (baked)
FEATURE [App::DocumentObjectGroupPython] BoltGroup005  # scripted group (container) (typed FeaturePython)
  AnimationStepTime = 0
  AnimationSteps = 20
  Distance = -100
  Group = -> [trajectory_line007]
  Revolutions = 0
  dir_vectors = (4) [(0,0,1),(0,0,1),(0,0,1),(0,0,1)]
  rot_centers = (4) [(428.91,112.021,33.6096),(428.91,386.021,33.6096),(-45.0904,112.021,33.6096),(-45.0904,386.021,33.6096)]
  rot_vectors = (4) [(0,0,1),(0,0,1),(0,0,1),(0,0,1)]
FEATURE [Part::Feature] trajectory_line008
  shape: bbox 2e-07 x 400 x 2e-07 mm, 0 faces, 0 solids (baked)
FEATURE [App::DocumentObjectGroupPython] SimpleGroup003  # scripted group (container) (typed FeaturePython)
  AnimationStepTime = 0
  AnimationSteps = 20
  Distance = 350
  Group = -> [trajectory_line008]
  Revolutions = 0
  dir_vectors = (1) [(0,-1,0)]
  rot_centers = (1) [(191.91,99.0214,69.6096)]
  rot_vectors = (1) [(0,-1,0)]
FEATURE [Part::Feature] trajectory_line009
  shape: bbox 200 x 2e-07 x 2e-07 mm, 0 faces, 0 solids (baked)
FEATURE [App::DocumentObjectGroupPython] SimpleGroup004  # scripted group (container) (typed FeaturePython)
  AnimationStepTime = 0
  AnimationSteps = 20
  Distance = 300
  Group = -> [trajectory_line009]
  Revolutions = 0
  dir_vectors = (1) [(1,2.22045e-16,0)]
  rot_centers = (1) [(441.91,249.021,69.6096)]
  rot_vectors = (1) [(1,2.22045e-16,0)]
FEATURE [Part::Feature] trajectory_line010
  shape: bbox 2e-07 x 200 x 2e-07 mm, 0 faces, 0 solids (baked)
FEATURE [App::DocumentObjectGroupPython] SimpleGroup005  # scripted group (container) (typed FeaturePython)
  AnimationStepTime = 0
  AnimationSteps = 20
  Distance = 150
  Group = -> [trajectory_line010]
  Revolutions = 0
  dir_vectors = (1) [(0,1,0)]
  rot_centers = (1) [(191.91,399.021,69.6096)]
  rot_vectors = (1) [(0,1,0)]
FEATURE [Part::Feature] trajectory_line011
  shape: bbox 200 x 2e-07 x 2e-07 mm, 0 faces, 0 solids (baked)
FEATURE [App::DocumentObjectGroupPython] SimpleGroup006  # scripted group (container) (typed FeaturePython)
  AnimationStepTime = 0
  AnimationSteps = 20
  Distance = 150
  Group = -> [trajectory_line011]
  Revolutions = 0
  dir_vectors = (1) [(-1,2.22045e-16,0)]
  rot_centers = (1) [(-58.0904,249.021,69.6096)]
  rot_vectors = (1) [(-1,2.22045e-16,0)]
FEATURE [Part::Feature] trajectory_line012
  shape: bbox 2e-07 x 2e-07 x 300 mm, 0 faces, 0 solids (baked)
FEATURE [App::DocumentObjectGroupPython] SimpleGroup007  # scripted group (container) (typed FeaturePython)
  AnimationStepTime = 0
  AnimationSteps = 20
  Distance = 300
  Group = -> [trajectory_line012]
  Revolutions = 0
  dir_vectors = (1) [(0,0,1)]
  rot_centers = (1) [(286.91,249.021,471.61)]
  rot_vectors = (1) [(0,0,1)]
FEATURE [Part::Feature] trajectory_line013
  shape: bbox 2e-07 x 2e-07 x 350 mm, 0 faces, 0 solids (baked)
FEATURE [App::DocumentObjectGroupPython] SimpleGroup009  # scripted group (container) (typed FeaturePython)
  AnimationStepTime = 0
  AnimationSteps = 20
  Distance = 350
  Group = -> [trajectory_line013]
  Revolutions = 0
  dir_vectors = (1) [(0,0,-1)]
  rot_centers = (1) [(-20.3404,286.521,448.21)]
  rot_vectors = (1) [(0,0,-1)]
FEATURE [Part::Feature] trajectory_line014
  shape: bbox 2e-07 x 2e-07 x 350 mm, 0 faces, 0 solids (baked)
FEATURE [App::DocumentObjectGroupPython] SimpleGroup010  # scripted group (container) (typed FeaturePython)
  AnimationStepTime = 0
  AnimationSteps = 20
  Distance = 350
  Group = -> [trajectory_line014]
  Revolutions = 0
  dir_vectors = (1) [(0,0,-1)]
  rot_centers = (1) [(-20.4547,211.899,448.21)]
  rot_vectors = (1) [(0,0,-1)]
FEATURE [Part::Feature] trajectory_line015
  shape: bbox 2e-07 x 2e-07 x 350 mm, 0 faces, 0 solids (baked)
FEATURE [App::DocumentObjectGroupPython] SimpleGroup011  # scripted group (container) (typed FeaturePython)
  AnimationStepTime = 0
  AnimationSteps = 20
  Distance = 350
  Group = -> [trajectory_line015]
  Revolutions = 0
  dir_vectors = (1) [(0,0,-1)]
  rot_centers = (1) [(44.1596,211.521,448.21)]
  rot_vectors = (1) [(0,0,-1)]
FEATURE [Part::Feature] trajectory_line016
  shape: bbox 2e-07 x 2e-07 x 350 mm, 0 faces, 0 solids (baked)
FEATURE [App::DocumentObjectGroupPython] SimpleGroup012  # scripted group (container) (typed FeaturePython)
  AnimationStepTime = 0
  AnimationSteps = 20
  Distance = 350
  Group = -> [trajectory_line016]
  Revolutions = 0
  dir_vectors = (1) [(0,0,-1)]
  rot_centers = (1) [(44.1596,286.521,448.21)]
  rot_vectors = (1) [(0,0,-1)]
FEATURE [Part::Feature] trajectory_line017
  shape: bbox 2e-07 x 2e-07 x 60 mm, 0 faces, 0 solids (baked)
FEATURE [App::DocumentObjectGroupPython] SimpleGroup015  # scripted group (container) (typed FeaturePython)
  AnimationStepTime = 0
  AnimationSteps = 20
  Distance = 60
  Group = -> [trajectory_line017]
  Revolutions = 0
  dir_vectors = (4) [(0,0,1),(0,0,1),(0,0,1),(0,0,1)]
  rot_centers = (4) [(194.407,249.021,466.61),(194.407,249.021,466.61),(194.407,249.021,466.61),(194.407,249.021,466.61)]
  rot_vectors = (4) [(0,0,1),(0,0,1),(0,0,1),(0,0,1)]
FEATURE [Part::Feature] trajectory_line018
  shape: bbox 2e-07 x 2e-07 x 250 mm, 0 faces, 0 solids (baked)
FEATURE [App::DocumentObjectGroupPython] SimpleGroup016  # scripted group (container) (typed FeaturePython)
  AnimationStepTime = 0
  AnimationSteps = 20
  Distance = 250
  Group = -> [trajectory_line018]
  Revolutions = 0
  dir_vectors = (2) [(0,0,-1),(0,0,-1)]
  rot_centers = (2) [(202.686,249.021,599.61),(202.686,249.021,599.61)]
  rot_vectors = (2) [(0,0,-1),(0,0,-1)]
FEATURE [Part::Feature] trajectory_line019
  shape: bbox 2e-07 x 2e-07 x 380 mm, 0 faces, 0 solids (baked)
FEATURE [App::DocumentObjectGroupPython] SimpleGroup017  # scripted group (container) (typed FeaturePython)
  AnimationStepTime = 0
  AnimationSteps = 20
  Distance = 380
  Group = -> [trajectory_line019]
  Revolutions = 0
  dir_vectors = (17) [(0,0,1),(0,0,1),(0,0,1),(0,0,1),(0,0,1),(0,0,1),(0,0,1),(0,0,1),(0,0,1),(0,0,1),(0,0,1),(0,0,1),(0,0,1),(0,0,1),(0,0,1),(0,0,1),(0,0,1)]
  rot_centers = (17) [(194.407,249.021,616.61),(194.407,249.021,616.61),(194.407,249.021,616.61),(194.407,249.021,616.61),(194.407,249.021,616.61),(194.407,249.021,616.61),+11 more]
  rot_vectors = (17) [(0,0,1),(0,0,1),(0,0,1),(0,0,1),(0,0,1),(0,0,1),(0,0,1),(0,0,1),(0,0,1),(0,0,1),(0,0,1),(0,0,1),(0,0,1),(0,0,1),(0,0,1),(0,0,1),(0,0,1)]
FEATURE [Part::Feature] trajectory_line020
  shape: bbox 2e-07 x 2e-07 x 30 mm, 0 faces, 0 solids (baked)
FEATURE [App::DocumentObjectGroupPython] SimpleGroup018  # scripted group (container) (typed FeaturePython)
  AnimationStepTime = 0
  AnimationSteps = 20
  Distance = 30
  Group = -> [trajectory_line020]
  Revolutions = 0
  dir_vectors = (11) [(0,0,1),(0,0,1),(0,0,1),(0,0,1),(0,0,1),(0,0,1),(0,0,1),(0,0,1),(0,0,1),(0,0,1),(0,0,1)]
  rot_centers = (11) [(96.4846,249.021,819.61),(96.4846,249.021,819.61),(96.4846,249.021,819.61),(96.4846,249.021,819.61),(96.4846,249.021,819.61),(96.4846,249.021,819.61),+5 more]
  rot_vectors = (11) [(0,0,1),(0,0,1),(0,0,1),(0,0,1),(0,0,1),(0,0,1),(0,0,1),(0,0,1),(0,0,1),(0,0,1),(0,0,1)]
FEATURE [Part::Feature] trajectory_line021
  shape: bbox 20 x 2e-07 x 2e-07 mm, 0 faces, 0 solids (baked)
FEATURE [App::DocumentObjectGroupPython] SimpleGroup019  # scripted group (container) (typed FeaturePython)
  AnimationStepTime = 0
  AnimationSteps = 20
  Distance = 20
  Group = -> [trajectory_line021]
  Revolutions = 0
  dir_vectors = (2) [(1,0,0),(1,0,0)]
  rot_centers = (2) [(106.335,249.021,803.472),(106.335,249.021,803.472)]
  rot_vectors = (2) [(1,0,0),(1,0,0)]
FEATURE [Part::Feature] trajectory_line022
  shape: bbox 60 x 2e-07 x 2e-07 mm, 0 faces, 0 solids (baked)
FEATURE [App::DocumentObjectGroupPython] SimpleGroup020  # scripted group (container) (typed FeaturePython)
  AnimationStepTime = 0
  AnimationSteps = 20
  Distance = 60
  Group = -> [trajectory_line022]
  Revolutions = 0
  dir_vectors = (2) [(-1,0,0),(-1,0,0)]
  rot_centers = (2) [(86.6346,249.021,803.472),(86.6346,249.021,803.472)]
  rot_vectors = (2) [(-1,0,0),(-1,0,0)]
FEATURE [Part::Feature] trajectory_line023
  shape: bbox 2e-07 x 2e-07 x 40 mm, 0 faces, 0 solids (baked)
FEATURE [App::DocumentObjectGroupPython] SimpleGroup021  # scripted group (container) (typed FeaturePython)
  AnimationStepTime = 0
  AnimationSteps = 20
  Distance = 40
  Group = -> [trajectory_line023]
  Revolutions = 0
  dir_vectors = (1) [(0,0,-1)]
  rot_centers = (1) [(2.68312e-13,3.25547e-12,-1)]
  rot_vectors = (1) [(0,0,-1)]
FEATURE [Part::Feature] trajectory_line024
  shape: bbox 2e-07 x 2e-07 x 300 mm, 0 faces, 0 solids (baked)
FEATURE [App::DocumentObjectGroupPython] SimpleGroup022  # scripted group (container) (typed FeaturePython)
  AnimationStepTime = 0
  AnimationSteps = 20
  Distance = 300
  Group = -> [trajectory_line024]
  Revolutions = 0
  dir_vectors = (2) [(0,0,-1),(0,0,-1)]
  rot_centers = (2) [(202.686,249.021,599.61),(202.686,249.021,599.61)]
  rot_vectors = (2) [(0,0,-1),(0,0,-1)]
FEATURE [Part::Feature] trajectory_line025
  shape: bbox 2e-07 x 2e-07 x 40 mm, 0 faces, 0 solids (baked)
FEATURE [App::DocumentObjectGroupPython] SimpleGroup023  # scripted group (container) (typed FeaturePython)
  AnimationStepTime = 0
  AnimationSteps = 20
  Distance = 40
  Group = -> [trajectory_line025]
  Revolutions = 0
  dir_vectors = (1) [(0,2.2e-16,-1)]
  rot_centers = (1) [(44.1086,332.271,297.61)]
  rot_vectors = (1) [(0,2.2e-16,-1)]
FEATURE [Part::Feature] trajectory_line026
  shape: bbox 60 x 2e-07 x 2e-07 mm, 0 faces, 0 solids (baked)
FEATURE [App::DocumentObjectGroupPython] SimpleGroup  # scripted group (container) (typed FeaturePython)
  AnimationStepTime = 0
  AnimationSteps = 20
  Distance = 60
  Group = -> [trajectory_line026]
  Revolutions = 0
  dir_vectors = (2) [(1,0,0),(1,0,0)]
  rot_centers = (2) [(441.91,249.021,488.11),(441.91,249.021,488.11)]
  rot_vectors = (2) [(1,0,0),(1,0,0)]
FEATURE [Part::Feature] trajectory_line027
  shape: bbox 51 x 60 x 2e-07 mm, 0 faces, 0 solids (baked)
FEATURE [App::DocumentObjectGroupPython] BoltGroup006  # scripted group (container) (typed FeaturePython)
  AnimationStepTime = 0
  AnimationSteps = 20
  Distance = 80
  Group = -> [trajectory_line027]
  Revolutions = 0
  dir_vectors = (2) [(0,-1,0),(0,-1,0)]
  rot_centers = (2) [(183.91,375.888,76.6096),(132.91,375.888,76.6096)]
  rot_vectors = (2) [(0,-1,0),(0,-1,0)]
FEATURE [Part::Feature] trajectory_line028
  shape: bbox 2e-07 x 20 x 2e-07 mm, 0 faces, 0 solids (baked)
FEATURE [App::DocumentObjectGroupPython] SimpleGroup024  # scripted group (container) (typed FeaturePython)
  AnimationStepTime = 0
  AnimationSteps = 20
  Distance = 40
  Group = -> [trajectory_line028]
  Revolutions = 0
  dir_vectors = (2) [(0,-1,0),(0,-1,0)]
  rot_centers = (2) [(191.91,582.021,69.6096),(191.91,582.021,69.6096)]
  rot_vectors = (2) [(0,-1,0),(0,-1,0)]
FEATURE [App::DocumentObjectGroupPython] ExplodedAssembly  # scripted group (container) (typed FeaturePython)
  AnimationStep = 0
  CurrentTrajectory = 0
  Group = -> [BoltGroup,SimpleGroup001,SimpleGroup002,BoltGroup001,BoltGroup002,BoltGroup003,BoltGroup004,BoltGroup005,SimpleGroup003,SimpleGroup004,SimpleGroup005,SimpleGroup006,SimpleGroup007,SimpleGroup009,SimpleGroup010,SimpleGroup011,SimpleGroup012,SimpleGroup015,SimpleGroup016,SimpleGroup017,SimpleGroup018,SimpleGroup019,SimpleGroup020,SimpleGroup021,SimpleGroup022,SimpleGroup023,SimpleGroup,BoltGroup006,+1 more]
  InAnimation = false
  RemoveAllTrajectories = false
  ResetAnimation = false
FEATURE [TechDraw::DrawViewSpreadsheet] Sheet
  CellEnd = f20
  CellStart = A1
  Font = osifont
  LineWidth = 0.35
  LockPosition = false
  Rotation = 0
  ScaleType = 2
  Source = -> Spreadsheet004
  Symbol = <blob: 24259 chars omitted>
  TextSize = 12
  X = 318.812
  Y = 206.527
FEATURE [TechDraw::DrawViewBalloon] Balloon
  BubbleShape = 0
  EndType = 0
  EndTypeScale = 1
  KinkLength = 5
  LockPosition = false
  OriginX = -481.407
  OriginY = -259.703
  Rotation = 0
  Scale = 0.2
  ScaleType = 0
  ShapeScale = 1
  SourceView = -> View008
  Text = 1
  TextWrapLen = -1
  X = -443.29
  Y = 649.943
FEATURE [TechDraw::DrawViewBalloon] Balloon001
  BubbleShape = 0
  EndType = 0
  EndTypeScale = 1
  KinkLength = 5
  LockPosition = false
  OriginX = -313.805
  OriginY = -26.3497
  Rotation = 0
  Scale = 0.2
  ScaleType = 0
  ShapeScale = 1
  SourceView = -> View008
  Text = 2
  TextWrapLen = -1
  X = -364.888
  Y = 646.648
FEATURE [TechDraw::DrawViewBalloon] Balloon002
  BubbleShape = 0
  EndType = 0
  EndTypeScale = 1
  KinkLength = 5
  LockPosition = false
  OriginX = -220.513
  OriginY = 230.622
  Rotation = 0
  Scale = 0.2
  ScaleType = 0
  ShapeScale = 1
  SourceView = -> Balloon001
  Text = 3
  TextWrapLen = -1
  X = -263.763
  Y = 647.338
FEATURE [TechDraw::DrawViewBalloon] Balloon003
  BubbleShape = 0
  EndType = 0
  EndTypeScale = 1
  KinkLength = 5
  LockPosition = false
  OriginX = -156.723
  OriginY = 292.175
  Rotation = 0
  Scale = 0.2
  ScaleType = 0
  ShapeScale = 1
  SourceView = -> Balloon002
  Text = 4
  TextWrapLen = -1
  X = -139.539
  Y = 645.099
FEATURE [TechDraw::DrawViewBalloon] Balloon004
  BubbleShape = 0
  EndType = 0
  EndTypeScale = 1
  KinkLength = 5
  LockPosition = false
  OriginX = -72.7873
  OriginY = 552.56
  Rotation = 0
  Scale = 0.2
  ScaleType = 0
  ShapeScale = 1
  SourceView = -> Balloon003
  Text = 5
  TextWrapLen = -1
  X = -36.2051
  Y = 645.099
FEATURE [TechDraw::DrawViewBalloon] Balloon005
  BubbleShape = 0
  EndType = 0
  EndTypeScale = 1
  KinkLength = 5
  LockPosition = false
  OriginX = -4.70651
  OriginY = 568.415
  Rotation = 0
  Scale = 0.2
  ScaleType = 0
  ShapeScale = 1
  SourceView = -> Balloon004
  Text = 6
  TextWrapLen = -1
  X = 67.3151
  Y = 646.032
FEATURE [TechDraw::DrawViewBalloon] Balloon006
  BubbleShape = 0
  EndType = 0
  EndTypeScale = 1
  KinkLength = 5
  LockPosition = false
  OriginX = 25.1371
  OriginY = 543.234
  Rotation = 0
  Scale = 0.2
  ScaleType = 0
  ShapeScale = 1
  SourceView = -> Balloon005
  Text = 7
  TextWrapLen = -1
  X = 152.183
  Y = 643.234
FEATURE [TechDraw::DrawViewBalloon] Balloon007
  BubbleShape = 0
  EndType = 0
  EndTypeScale = 1
  KinkLength = 5
  LockPosition = false
  OriginX = 36.3285
  OriginY = 505.93
  Rotation = 0
  Scale = 0.2
  ScaleType = 0
  ShapeScale = 1
  SourceView = -> Balloon006
  Text = 8
  TextWrapLen = -1
  X = 257.568
  Y = 646.032
FEATURE [TechDraw::DrawViewBalloon] Balloon008
  BubbleShape = 0
  EndType = 0
  EndTypeScale = 1
  KinkLength = 5
  LockPosition = false
  OriginX = 179.018
  OriginY = 441.579
  Rotation = 0
  Scale = 0.2
  ScaleType = 0
  ShapeScale = 1
  SourceView = -> Balloon007
  Text = 9
  TextWrapLen = -1
  X = 362.021
  Y = 645.099
FEATURE [TechDraw::DrawViewBalloon] Balloon009
  BubbleShape = 0
  EndType = 0
  EndTypeScale = 1
  KinkLength = 5
  LockPosition = false
  OriginX = -64.3938
  OriginY = 45.2183
  Rotation = 0
  Scale = 0.2
  ScaleType = 0
  ShapeScale = 1
  SourceView = -> Balloon008
  Text = 10
  TextWrapLen = -1
  X = 462.04
  Y = 325.301
FEATURE [TechDraw::DrawViewBalloon] Balloon012
  BubbleShape = 0
  EndType = 0
  EndTypeScale = 1
  KinkLength = 5
  LockPosition = false
  OriginX = 24.2045
  OriginY = -5.14282
  Rotation = 0
  Scale = 0.2
  ScaleType = 0
  ShapeScale = 1
  SourceView = -> Balloon009
  Text = 11
  TextWrapLen = -1
  X = 465.735
  Y = 220.478
FEATURE [TechDraw::DrawViewBalloon] Balloon013
  BubbleShape = 0
  EndType = 0
  EndTypeScale = 1
  KinkLength = 5
  LockPosition = false
  OriginX = -47.6068
  OriginY = -57.3692
  Rotation = 0
  Scale = 0.2
  ScaleType = 0
  ShapeScale = 1
  SourceView = -> Balloon012
  Text = 12
  TextWrapLen = -1
  X = 469.466
  Y = 117.275
FEATURE [TechDraw::DrawViewBalloon] Balloon014
  BubbleShape = 0
  EndType = 0
  EndTypeScale = 1
  KinkLength = 5
  LockPosition = false
  OriginX = 85.7571
  OriginY = -88.1455
  Rotation = 0
  Scale = 0.2
  ScaleType = 0
  ShapeScale = 1
  SourceView = -> Balloon013
  Text = 13
  TextWrapLen = -1
  X = 471.296
  Y = 54.6317
FEATURE [TechDraw::DrawViewBalloon] Balloon015
  BubbleShape = 0
  EndType = 0
  EndTypeScale = 1
  KinkLength = 5
  LockPosition = false
  OriginX = 96.0158
  OriginY = -128.248
  Rotation = 0
  Scale = 0.2
  ScaleType = 0
  ShapeScale = 1
  SourceView = -> Balloon014
  Text = 14
  TextWrapLen = -1
  X = 474.548
  Y = -4.6948
FEATURE [TechDraw::DrawViewBalloon] Balloon016
  BubbleShape = 0
  EndType = 0
  EndTypeScale = 1
  KinkLength = 5
  LockPosition = false
  OriginX = 229.768
  OriginY = -190.473
  Rotation = 0
  Scale = 0.2
  ScaleType = 0
  ShapeScale = 1
  SourceView = -> Balloon015
  Text = 15
  TextWrapLen = -1
  X = 475.441
  Y = -70.0909
FEATURE [TechDraw::DrawViewBalloon] Balloon017
  BubbleShape = 0
  EndType = 0
  EndTypeScale = 1
  KinkLength = 5
  LockPosition = false
  OriginX = 283.738
  OriginY = -198.906
  Rotation = 0
  Scale = 0.2
  ScaleType = 0
  ShapeScale = 1
  SourceView = -> Balloon016
  Text = 16
  TextWrapLen = -1
  X = 475.423
  Y = -132.925
FEATURE [TechDraw::DrawViewBalloon] Balloon018
  BubbleShape = 0
  EndType = 0
  EndTypeScale = 1
  KinkLength = 5
  LockPosition = false
  OriginX = 299.462
  OriginY = -326.167
  Rotation = 0
  Scale = 0.2
  ScaleType = 0
  ShapeScale = 1
  SourceView = -> Balloon017
  Text = 17
  TextWrapLen = -1
  X = 472.665
  Y = -212.442
FEATURE [TechDraw::DrawViewBalloon] Balloon019
  BubbleShape = 0
  EndType = 0
  EndTypeScale = 1
  KinkLength = 5
  LockPosition = false
  OriginX = -22.0748
  OriginY = -13.4247
  Rotation = 0
  Scale = 0.2
  ScaleType = 0
  ShapeScale = 1
  SourceView = -> ActiveView001
  Text = 18
  TextWrapLen = -1
  X = -13.7483
  Y = -103.194
FEATURE [TechDraw::DrawPage] Page007  label="ExplodedBOM"
  KeepUpdated = false
  NextBalloonIndex = 19
  ProjectionType = 1
  Scale = 0.2
  Template = -> Template007
  Views = -> [View008,ActiveView001,Sheet,Balloon,Balloon001,Balloon002,Balloon003,Balloon004,Balloon005,Balloon006,Balloon007,Balloon008,Balloon009,Balloon012,Balloon013,Balloon014,Balloon015,Balloon016,Balloon017,Balloon018,Balloon019]
FEATURE [App::DocumentObjectGroup] Group002  label="Drawings"
  Group = -> [Page,Page001,Page002,Page003,Page004,Page005,Page006,Page007,Group003]
